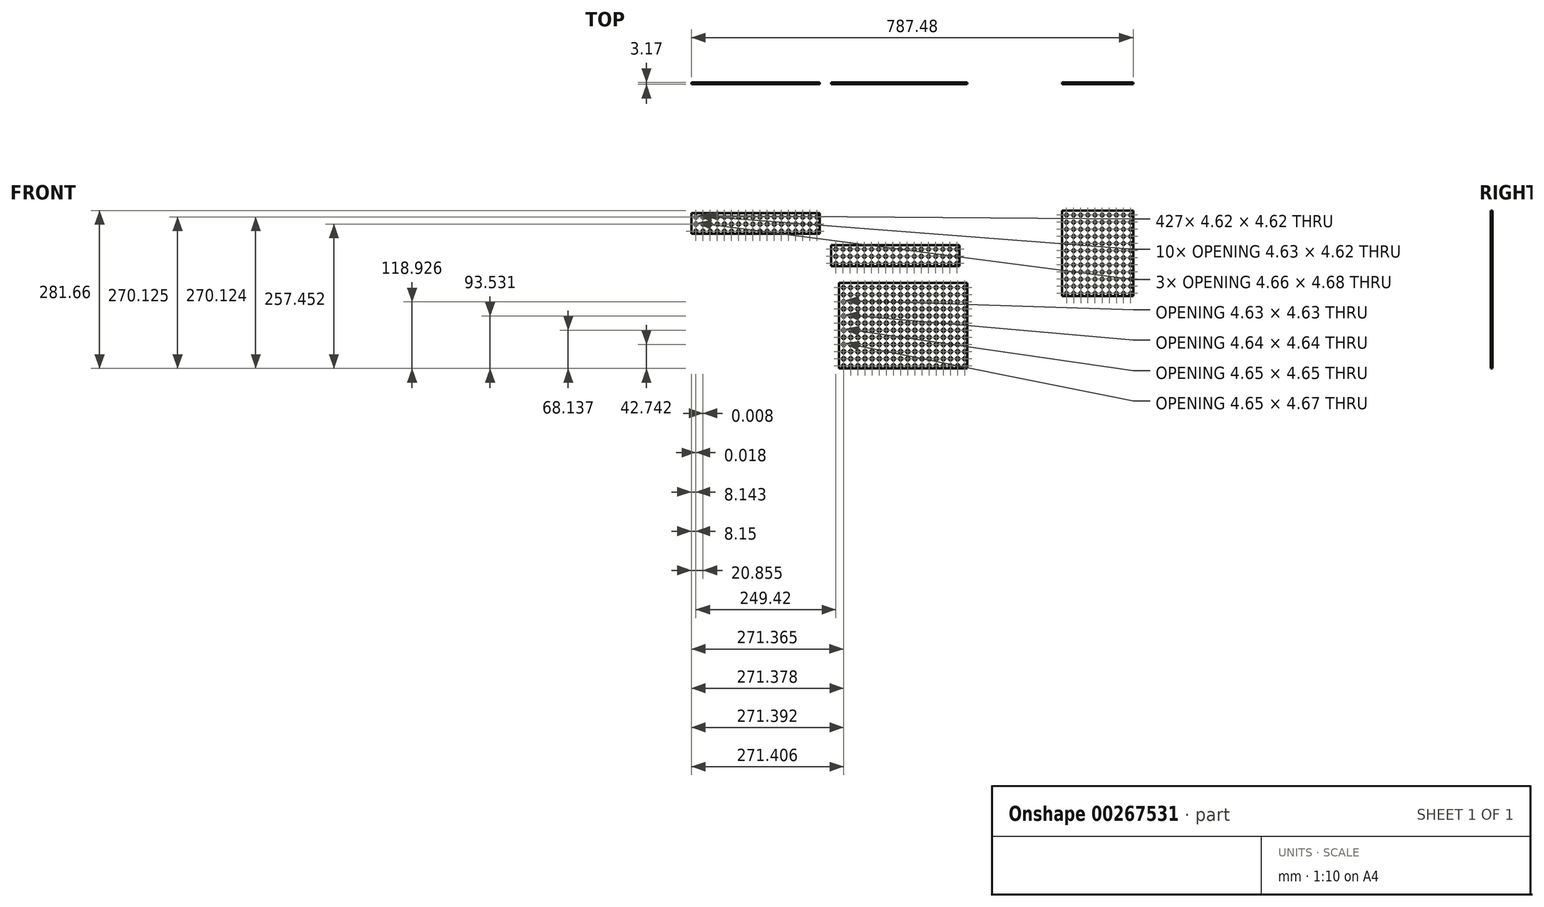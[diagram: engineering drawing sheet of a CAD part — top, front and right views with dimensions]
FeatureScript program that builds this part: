
annotation { "Feature Type Name" : "Feature", "Feature Type Description" : "" }
export const myFeature = defineFeature(function(context is Context, id is Id, definition is map)
    precondition{}
    {
        {
            var Q0;
            Q0=qCreatedBy(makeId("Front.planeOp"),FACE);
            var sketch = newSketch(context, id + "F0", { "sketchPlane" : qUnion([Q0])});
            skLineSegment(sketch, "E0", {"start": v(-0.59, 75.15) * mm, "end": v(113.71, 75.15) * mm});
            skLineSegment(sketch, "E1", {"start": v(-0.59, -77.25) * mm, "end": v(113.71, -77.25) * mm});
            skLineSegment(sketch, "E2", {"start": v(-0.59, -77.25) * mm, "end": v(-114.89, -77.25) * mm});
            skLineSegment(sketch, "E3", {"start": v(-114.89, 75.15) * mm, "end": v(-114.89, -77.25) * mm});
            skLineSegment(sketch, "E4", {"start": v(113.71, 75.15) * mm, "end": v(113.71, -77.25) * mm});
            skLineSegment(sketch, "E5", {"start": v(-114.89, -77.25) * mm, "end": v(-114.89, -73.21) * mm});
            skLineSegment(sketch, "E6", {"start": v(-114.89, -77.25) * mm, "end": v(-110.85, -77.25) * mm});
            skLineSegment(sketch, "E7", {"start": v(-114.89, 75.15) * mm, "end": v(-114.89, 71.1) * mm});
            skLineSegment(sketch, "E8", {"start": v(113.71, 75.15) * mm, "end": v(109.67, 75.15) * mm});
            skLineSegment(sketch, "E9", {"start": v(-97.56, 75.15) * mm, "end": v(113.71, 75.15) * mm});
            skLineSegment(sketch, "E10", {"start": v(-114.89, 75.15) * mm, "end": v(-97.56, 75.15) * mm});
            skLineSegment(sketch, "E11", {"start": v(-114.89, 75.15) * mm, "end": v(-106.8, 75.15) * mm});
            skLineSegment(sketch, "E12.bottom", {"start": v(-109.12, 69.38) * mm, "end": v(-104.5, 69.38) * mm});
            skLineSegment(sketch, "E12.top", {"start": v(-109.12, 64.76) * mm, "end": v(-104.5, 64.76) * mm});
            skLineSegment(sketch, "E12.left", {"start": v(-109.12, 69.38) * mm, "end": v(-109.12, 64.76) * mm});
            skLineSegment(sketch, "E12.right", {"start": v(-104.5, 69.38) * mm, "end": v(-104.5, 64.76) * mm});
            skPoint(sketch, "E12.middle", {"position": v(-106.8, 67.07) * mm});
            skLineSegment(sketch, "E13.bottom", {"start": v(-109.12, 56.68) * mm, "end": v(-104.5, 56.68) * mm});
            skLineSegment(sketch, "E13.top", {"start": v(-109.12, 52.06) * mm, "end": v(-104.5, 52.06) * mm});
            skLineSegment(sketch, "E13.left", {"start": v(-109.12, 56.68) * mm, "end": v(-109.12, 52.06) * mm});
            skLineSegment(sketch, "E13.right", {"start": v(-104.5, 56.68) * mm, "end": v(-104.5, 52.06) * mm});
            skPoint(sketch, "E13.middle", {"position": v(-106.8, 54.37) * mm});
            skLineSegment(sketch, "E14.bottom", {"start": v(-96.42, 69.38) * mm, "end": v(-91.8, 69.38) * mm});
            skLineSegment(sketch, "E14.top", {"start": v(-96.42, 64.76) * mm, "end": v(-91.8, 64.76) * mm});
            skLineSegment(sketch, "E14.left", {"start": v(-96.42, 69.38) * mm, "end": v(-96.42, 64.76) * mm});
            skLineSegment(sketch, "E14.right", {"start": v(-91.8, 69.38) * mm, "end": v(-91.8, 64.76) * mm});
            skPoint(sketch, "E14.middle", {"position": v(-94.1, 67.07) * mm});
            skLineSegment(sketch, "E15.1.0.0", {"start": v(-83.72, 69.38) * mm, "end": v(-79.1, 69.38) * mm});
            skLineSegment(sketch, "E15.1.0.1", {"start": v(-79.1, 69.38) * mm, "end": v(-79.1, 64.76) * mm});
            skLineSegment(sketch, "E15.1.0.2", {"start": v(-83.72, 64.76) * mm, "end": v(-79.1, 64.76) * mm});
            skLineSegment(sketch, "E15.1.0.3", {"start": v(-83.72, 69.38) * mm, "end": v(-83.72, 64.76) * mm});
            skLineSegment(sketch, "E15.1.0.4", {"start": v(-71.02, 69.38) * mm, "end": v(-66.4, 69.38) * mm});
            skLineSegment(sketch, "E15.1.0.5", {"start": v(-66.4, 69.38) * mm, "end": v(-66.4, 64.76) * mm});
            skLineSegment(sketch, "E15.1.0.6", {"start": v(-71.02, 64.76) * mm, "end": v(-66.4, 64.76) * mm});
            skLineSegment(sketch, "E15.1.0.7", {"start": v(-71.02, 69.38) * mm, "end": v(-71.02, 64.76) * mm});
            skLineSegment(sketch, "E15.2.0.0", {"start": v(-58.32, 69.38) * mm, "end": v(-53.7, 69.38) * mm});
            skLineSegment(sketch, "E15.2.0.1", {"start": v(-53.7, 69.38) * mm, "end": v(-53.7, 64.76) * mm});
            skLineSegment(sketch, "E15.2.0.2", {"start": v(-58.32, 64.76) * mm, "end": v(-53.7, 64.76) * mm});
            skLineSegment(sketch, "E15.2.0.3", {"start": v(-58.32, 69.38) * mm, "end": v(-58.32, 64.76) * mm});
            skLineSegment(sketch, "E15.2.0.4", {"start": v(-45.62, 69.38) * mm, "end": v(-41, 69.38) * mm});
            skLineSegment(sketch, "E15.2.0.5", {"start": v(-41, 69.38) * mm, "end": v(-41, 64.76) * mm});
            skLineSegment(sketch, "E15.2.0.6", {"start": v(-45.62, 64.76) * mm, "end": v(-41, 64.76) * mm});
            skLineSegment(sketch, "E15.2.0.7", {"start": v(-45.62, 69.38) * mm, "end": v(-45.62, 64.76) * mm});
            skLineSegment(sketch, "E15.3.0.0", {"start": v(-32.92, 69.38) * mm, "end": v(-28.3, 69.38) * mm});
            skLineSegment(sketch, "E15.3.0.1", {"start": v(-28.3, 69.38) * mm, "end": v(-28.3, 64.76) * mm});
            skLineSegment(sketch, "E15.3.0.2", {"start": v(-32.92, 64.76) * mm, "end": v(-28.3, 64.76) * mm});
            skLineSegment(sketch, "E15.3.0.3", {"start": v(-32.92, 69.38) * mm, "end": v(-32.92, 64.76) * mm});
            skLineSegment(sketch, "E15.3.0.4", {"start": v(-20.22, 69.38) * mm, "end": v(-15.6, 69.38) * mm});
            skLineSegment(sketch, "E15.3.0.5", {"start": v(-15.6, 69.38) * mm, "end": v(-15.6, 64.76) * mm});
            skLineSegment(sketch, "E15.3.0.6", {"start": v(-20.22, 64.76) * mm, "end": v(-15.6, 64.76) * mm});
            skLineSegment(sketch, "E15.3.0.7", {"start": v(-20.22, 69.38) * mm, "end": v(-20.22, 64.76) * mm});
            skLineSegment(sketch, "E15.4.0.0", {"start": v(-7.52, 69.38) * mm, "end": v(-2.9, 69.38) * mm});
            skLineSegment(sketch, "E15.4.0.1", {"start": v(-2.9, 69.38) * mm, "end": v(-2.9, 64.76) * mm});
            skLineSegment(sketch, "E15.4.0.2", {"start": v(-7.52, 64.76) * mm, "end": v(-2.9, 64.76) * mm});
            skLineSegment(sketch, "E15.4.0.3", {"start": v(-7.52, 69.38) * mm, "end": v(-7.52, 64.76) * mm});
            skLineSegment(sketch, "E15.4.0.4", {"start": v(5.18, 69.38) * mm, "end": v(9.8, 69.38) * mm});
            skLineSegment(sketch, "E15.4.0.5", {"start": v(9.8, 69.38) * mm, "end": v(9.8, 64.76) * mm});
            skLineSegment(sketch, "E15.4.0.6", {"start": v(5.18, 64.76) * mm, "end": v(9.8, 64.76) * mm});
            skLineSegment(sketch, "E15.4.0.7", {"start": v(5.18, 69.38) * mm, "end": v(5.18, 64.76) * mm});
            skLineSegment(sketch, "E15.5.0.0", {"start": v(17.88, 69.38) * mm, "end": v(22.5, 69.38) * mm});
            skLineSegment(sketch, "E15.5.0.1", {"start": v(22.5, 69.38) * mm, "end": v(22.5, 64.76) * mm});
            skLineSegment(sketch, "E15.5.0.2", {"start": v(17.88, 64.76) * mm, "end": v(22.5, 64.76) * mm});
            skLineSegment(sketch, "E15.5.0.3", {"start": v(17.88, 69.38) * mm, "end": v(17.88, 64.76) * mm});
            skLineSegment(sketch, "E15.5.0.4", {"start": v(30.58, 69.38) * mm, "end": v(35.2, 69.38) * mm});
            skLineSegment(sketch, "E15.5.0.5", {"start": v(35.2, 69.38) * mm, "end": v(35.2, 64.76) * mm});
            skLineSegment(sketch, "E15.5.0.6", {"start": v(30.58, 64.76) * mm, "end": v(35.2, 64.76) * mm});
            skLineSegment(sketch, "E15.5.0.7", {"start": v(30.58, 69.38) * mm, "end": v(30.58, 64.76) * mm});
            skLineSegment(sketch, "E15.6.0.0", {"start": v(43.28, 69.38) * mm, "end": v(47.9, 69.38) * mm});
            skLineSegment(sketch, "E15.6.0.1", {"start": v(47.9, 69.38) * mm, "end": v(47.9, 64.76) * mm});
            skLineSegment(sketch, "E15.6.0.2", {"start": v(43.28, 64.76) * mm, "end": v(47.9, 64.76) * mm});
            skLineSegment(sketch, "E15.6.0.3", {"start": v(43.28, 69.38) * mm, "end": v(43.28, 64.76) * mm});
            skLineSegment(sketch, "E15.6.0.4", {"start": v(55.98, 69.38) * mm, "end": v(60.6, 69.38) * mm});
            skLineSegment(sketch, "E15.6.0.5", {"start": v(60.6, 69.38) * mm, "end": v(60.6, 64.76) * mm});
            skLineSegment(sketch, "E15.6.0.6", {"start": v(55.98, 64.76) * mm, "end": v(60.6, 64.76) * mm});
            skLineSegment(sketch, "E15.6.0.7", {"start": v(55.98, 69.38) * mm, "end": v(55.98, 64.76) * mm});
            skLineSegment(sketch, "E15.7.0.0", {"start": v(68.68, 69.38) * mm, "end": v(73.3, 69.38) * mm});
            skLineSegment(sketch, "E15.7.0.1", {"start": v(73.3, 69.38) * mm, "end": v(73.3, 64.76) * mm});
            skLineSegment(sketch, "E15.7.0.2", {"start": v(68.68, 64.76) * mm, "end": v(73.3, 64.76) * mm});
            skLineSegment(sketch, "E15.7.0.3", {"start": v(68.68, 69.38) * mm, "end": v(68.68, 64.76) * mm});
            skLineSegment(sketch, "E15.7.0.4", {"start": v(81.38, 69.38) * mm, "end": v(86, 69.38) * mm});
            skLineSegment(sketch, "E15.7.0.5", {"start": v(86, 69.38) * mm, "end": v(86, 64.76) * mm});
            skLineSegment(sketch, "E15.7.0.6", {"start": v(81.38, 64.76) * mm, "end": v(86, 64.76) * mm});
            skLineSegment(sketch, "E15.7.0.7", {"start": v(81.38, 69.38) * mm, "end": v(81.38, 64.76) * mm});
            skLineSegment(sketch, "E15.8.0.0", {"start": v(94.08, 69.38) * mm, "end": v(98.7, 69.38) * mm});
            skLineSegment(sketch, "E15.8.0.1", {"start": v(98.7, 69.38) * mm, "end": v(98.7, 64.76) * mm});
            skLineSegment(sketch, "E15.8.0.2", {"start": v(94.08, 64.76) * mm, "end": v(98.7, 64.76) * mm});
            skLineSegment(sketch, "E15.8.0.3", {"start": v(94.08, 69.38) * mm, "end": v(94.08, 64.76) * mm});
            skLineSegment(sketch, "E15.8.0.4", {"start": v(106.78, 69.38) * mm, "end": v(111.4, 69.38) * mm});
            skLineSegment(sketch, "E15.8.0.5", {"start": v(111.4, 69.38) * mm, "end": v(111.4, 64.76) * mm});
            skLineSegment(sketch, "E15.8.0.6", {"start": v(106.78, 64.76) * mm, "end": v(111.4, 64.76) * mm});
            skLineSegment(sketch, "E15.8.0.7", {"start": v(106.78, 69.38) * mm, "end": v(106.78, 64.76) * mm});
            skPoint(sketch, "E16.0.1.0", {"position": v(-94.1, 54.37) * mm});
            skLineSegment(sketch, "E16.0.1.2", {"start": v(-71.01, 52.06) * mm, "end": v(-66.39, 52.06) * mm});
            skLineSegment(sketch, "E16.0.1.3", {"start": v(-109.11, 52.06) * mm, "end": v(-104.49, 52.06) * mm});
            skLineSegment(sketch, "E16.0.1.4", {"start": v(68.69, 56.68) * mm, "end": v(73.31, 56.68) * mm});
            skLineSegment(sketch, "E16.0.1.5", {"start": v(-96.41, 56.68) * mm, "end": v(-91.79, 56.68) * mm});
            skLineSegment(sketch, "E16.0.1.6", {"start": v(17.89, 56.68) * mm, "end": v(22.51, 56.68) * mm});
            skLineSegment(sketch, "E16.0.1.7", {"start": v(-32.91, 56.68) * mm, "end": v(-28.29, 56.68) * mm});
            skLineSegment(sketch, "E16.0.1.8", {"start": v(-83.71, 56.68) * mm, "end": v(-79.09, 56.68) * mm});
            skLineSegment(sketch, "E16.0.1.9", {"start": v(-7.51, 56.68) * mm, "end": v(-2.89, 56.68) * mm});
            skLineSegment(sketch, "E16.0.1.10", {"start": v(-58.31, 52.06) * mm, "end": v(-53.69, 52.06) * mm});
            skLineSegment(sketch, "E16.0.1.11", {"start": v(17.89, 56.68) * mm, "end": v(17.89, 52.06) * mm});
            skLineSegment(sketch, "E16.0.1.12", {"start": v(35.21, 56.68) * mm, "end": v(35.21, 52.06) * mm});
            skLineSegment(sketch, "E16.0.1.13", {"start": v(-15.59, 56.68) * mm, "end": v(-15.59, 52.06) * mm});
            skLineSegment(sketch, "E16.0.1.14", {"start": v(-66.39, 56.68) * mm, "end": v(-66.39, 52.06) * mm});
            skLineSegment(sketch, "E16.0.1.15", {"start": v(106.79, 56.68) * mm, "end": v(111.41, 56.68) * mm});
            skLineSegment(sketch, "E16.0.1.16", {"start": v(73.31, 56.68) * mm, "end": v(73.31, 52.06) * mm});
            skLineSegment(sketch, "E16.0.1.17", {"start": v(22.51, 56.68) * mm, "end": v(22.51, 52.06) * mm});
            skLineSegment(sketch, "E16.0.1.18", {"start": v(30.59, 56.68) * mm, "end": v(30.59, 52.06) * mm});
            skLineSegment(sketch, "E16.0.1.19", {"start": v(-28.29, 56.68) * mm, "end": v(-28.29, 52.06) * mm});
            skLineSegment(sketch, "E16.0.1.20", {"start": v(-2.89, 56.68) * mm, "end": v(-2.89, 52.06) * mm});
            skLineSegment(sketch, "E16.0.1.21", {"start": v(-53.69, 56.68) * mm, "end": v(-53.69, 52.06) * mm});
            skLineSegment(sketch, "E16.0.1.22", {"start": v(-7.51, 52.06) * mm, "end": v(-2.89, 52.06) * mm});
            skLineSegment(sketch, "E16.0.1.23", {"start": v(68.69, 56.68) * mm, "end": v(68.69, 52.06) * mm});
            skLineSegment(sketch, "E16.0.1.24", {"start": v(-79.09, 56.68) * mm, "end": v(-79.09, 52.06) * mm});
            skLineSegment(sketch, "E16.0.1.25", {"start": v(-20.21, 56.68) * mm, "end": v(-20.21, 52.06) * mm});
            skLineSegment(sketch, "E16.0.1.26", {"start": v(-32.91, 56.68) * mm, "end": v(-32.91, 52.06) * mm});
            skLineSegment(sketch, "E16.0.1.27", {"start": v(-83.71, 56.68) * mm, "end": v(-83.71, 52.06) * mm});
            skLineSegment(sketch, "E16.0.1.28", {"start": v(81.39, 56.68) * mm, "end": v(81.39, 52.06) * mm});
            skLineSegment(sketch, "E16.0.1.29", {"start": v(-104.49, 56.68) * mm, "end": v(-104.49, 52.06) * mm});
            skLineSegment(sketch, "E16.0.1.30", {"start": v(86.01, 56.68) * mm, "end": v(86.01, 52.06) * mm});
            skLineSegment(sketch, "E16.0.1.31", {"start": v(-71.01, 56.68) * mm, "end": v(-71.01, 52.06) * mm});
            skLineSegment(sketch, "E16.0.1.32", {"start": v(-7.51, 56.68) * mm, "end": v(-7.51, 52.06) * mm});
            skLineSegment(sketch, "E16.0.1.33", {"start": v(94.09, 52.06) * mm, "end": v(98.71, 52.06) * mm});
            skLineSegment(sketch, "E16.0.1.34", {"start": v(43.29, 52.06) * mm, "end": v(47.91, 52.06) * mm});
            skLineSegment(sketch, "E16.0.1.35", {"start": v(-109.11, 56.68) * mm, "end": v(-104.49, 56.68) * mm});
            skLineSegment(sketch, "E16.0.1.36", {"start": v(81.39, 52.06) * mm, "end": v(86.01, 52.06) * mm});
            skLineSegment(sketch, "E16.0.1.37", {"start": v(68.69, 52.06) * mm, "end": v(73.31, 52.06) * mm});
            skLineSegment(sketch, "E16.0.1.38", {"start": v(-58.31, 56.68) * mm, "end": v(-58.31, 52.06) * mm});
            skLineSegment(sketch, "E16.0.1.39", {"start": v(30.59, 52.06) * mm, "end": v(35.21, 52.06) * mm});
            skLineSegment(sketch, "E16.0.1.40", {"start": v(17.89, 52.06) * mm, "end": v(22.51, 52.06) * mm});
            skLineSegment(sketch, "E16.0.1.41", {"start": v(-20.21, 52.06) * mm, "end": v(-15.59, 52.06) * mm});
            skLineSegment(sketch, "E16.0.1.42", {"start": v(-32.91, 52.06) * mm, "end": v(-28.29, 52.06) * mm});
            skLineSegment(sketch, "E16.0.1.43", {"start": v(-83.71, 52.06) * mm, "end": v(-79.09, 52.06) * mm});
            skLineSegment(sketch, "E16.0.1.44", {"start": v(94.09, 56.68) * mm, "end": v(94.09, 52.06) * mm});
            skLineSegment(sketch, "E16.0.1.45", {"start": v(43.29, 56.68) * mm, "end": v(43.29, 52.06) * mm});
            skLineSegment(sketch, "E16.0.1.46", {"start": v(-58.31, 56.68) * mm, "end": v(-53.69, 56.68) * mm});
            skLineSegment(sketch, "E16.0.1.47", {"start": v(5.19, 56.68) * mm, "end": v(9.81, 56.68) * mm});
            skLineSegment(sketch, "E16.0.1.48", {"start": v(-45.61, 56.68) * mm, "end": v(-40.99, 56.68) * mm});
            skLineSegment(sketch, "E16.0.1.49", {"start": v(94.09, 56.68) * mm, "end": v(98.71, 56.68) * mm});
            skLineSegment(sketch, "E16.0.1.50", {"start": v(43.29, 56.68) * mm, "end": v(47.91, 56.68) * mm});
            skLineSegment(sketch, "E16.0.1.51", {"start": v(55.99, 56.68) * mm, "end": v(60.61, 56.68) * mm});
            skLineSegment(sketch, "E16.0.1.52", {"start": v(5.19, 52.06) * mm, "end": v(9.81, 52.06) * mm});
            skLineSegment(sketch, "E16.0.1.53", {"start": v(55.99, 52.06) * mm, "end": v(60.61, 52.06) * mm});
            skLineSegment(sketch, "E16.0.1.54", {"start": v(-45.61, 52.06) * mm, "end": v(-40.99, 52.06) * mm});
            skLineSegment(sketch, "E16.0.1.55", {"start": v(-96.41, 56.68) * mm, "end": v(-96.41, 52.06) * mm});
            skLineSegment(sketch, "E16.0.1.56", {"start": v(98.71, 56.68) * mm, "end": v(98.71, 52.06) * mm});
            skLineSegment(sketch, "E16.0.1.57", {"start": v(47.91, 56.68) * mm, "end": v(47.91, 52.06) * mm});
            skLineSegment(sketch, "E16.0.1.58", {"start": v(106.79, 52.06) * mm, "end": v(111.41, 52.06) * mm});
            skLineSegment(sketch, "E16.0.1.59", {"start": v(-71.01, 56.68) * mm, "end": v(-66.39, 56.68) * mm});
            skLineSegment(sketch, "E16.0.1.60", {"start": v(106.79, 56.68) * mm, "end": v(106.79, 52.06) * mm});
            skLineSegment(sketch, "E16.0.1.61", {"start": v(-20.21, 56.68) * mm, "end": v(-15.59, 56.68) * mm});
            skLineSegment(sketch, "E16.0.1.62", {"start": v(-91.79, 56.68) * mm, "end": v(-91.79, 52.06) * mm});
            skLineSegment(sketch, "E16.0.1.63", {"start": v(30.59, 56.68) * mm, "end": v(35.21, 56.68) * mm});
            skLineSegment(sketch, "E16.0.1.64", {"start": v(81.39, 56.68) * mm, "end": v(86.01, 56.68) * mm});
            skLineSegment(sketch, "E16.0.1.65", {"start": v(-45.61, 56.68) * mm, "end": v(-45.61, 52.06) * mm});
            skLineSegment(sketch, "E16.0.1.66", {"start": v(5.19, 56.68) * mm, "end": v(5.19, 52.06) * mm});
            skLineSegment(sketch, "E16.0.1.67", {"start": v(55.99, 56.68) * mm, "end": v(55.99, 52.06) * mm});
            skLineSegment(sketch, "E16.0.1.68", {"start": v(60.61, 56.68) * mm, "end": v(60.61, 52.06) * mm});
            skLineSegment(sketch, "E16.0.1.69", {"start": v(111.41, 56.68) * mm, "end": v(111.41, 52.06) * mm});
            skLineSegment(sketch, "E16.0.1.70", {"start": v(-96.41, 52.06) * mm, "end": v(-91.79, 52.06) * mm});
            skLineSegment(sketch, "E16.0.1.71", {"start": v(-40.99, 56.68) * mm, "end": v(-40.99, 52.06) * mm});
            skLineSegment(sketch, "E16.0.1.72", {"start": v(-109.11, 56.68) * mm, "end": v(-109.11, 52.06) * mm});
            skLineSegment(sketch, "E16.0.1.73", {"start": v(9.81, 56.68) * mm, "end": v(9.81, 52.06) * mm});
            skLineSegment(sketch, "E17.1.0.0", {"start": v(-109.11, 44) * mm, "end": v(-104.49, 44) * mm});
            skLineSegment(sketch, "E17.1.0.1", {"start": v(-109.11, 44) * mm, "end": v(-109.11, 39.37) * mm});
            skLineSegment(sketch, "E17.1.0.2", {"start": v(-109.11, 39.37) * mm, "end": v(-104.49, 39.37) * mm});
            skLineSegment(sketch, "E17.1.0.3", {"start": v(-104.49, 44) * mm, "end": v(-104.49, 39.37) * mm});
            skLineSegment(sketch, "E17.1.0.4", {"start": v(-109.1, 31.3) * mm, "end": v(-104.48, 31.3) * mm});
            skLineSegment(sketch, "E17.1.0.5", {"start": v(-104.49, 31.3) * mm, "end": v(-104.49, 26.67) * mm});
            skLineSegment(sketch, "E17.1.0.6", {"start": v(-109.1, 26.67) * mm, "end": v(-104.48, 26.67) * mm});
            skLineSegment(sketch, "E17.1.0.7", {"start": v(-109.11, 31.3) * mm, "end": v(-109.11, 26.67) * mm});
            skLineSegment(sketch, "E17.2.0.0", {"start": v(-109.1, 18.6) * mm, "end": v(-104.48, 18.6) * mm});
            skLineSegment(sketch, "E17.2.0.1", {"start": v(-109.1, 18.6) * mm, "end": v(-109.1, 13.98) * mm});
            skLineSegment(sketch, "E17.2.0.2", {"start": v(-109.1, 13.98) * mm, "end": v(-104.48, 13.98) * mm});
            skLineSegment(sketch, "E17.2.0.3", {"start": v(-104.48, 18.6) * mm, "end": v(-104.48, 13.98) * mm});
            skLineSegment(sketch, "E17.2.0.4", {"start": v(-109.1, 5.9) * mm, "end": v(-104.47, 5.9) * mm});
            skLineSegment(sketch, "E17.2.0.5", {"start": v(-104.48, 5.9) * mm, "end": v(-104.48, 1.28) * mm});
            skLineSegment(sketch, "E17.2.0.6", {"start": v(-109.1, 1.28) * mm, "end": v(-104.47, 1.28) * mm});
            skLineSegment(sketch, "E17.2.0.7", {"start": v(-109.1, 5.9) * mm, "end": v(-109.1, 1.28) * mm});
            skLineSegment(sketch, "E17.3.0.0", {"start": v(-109.1, -6.79) * mm, "end": v(-104.47, -6.79) * mm});
            skLineSegment(sketch, "E17.3.0.1", {"start": v(-109.1, -6.79) * mm, "end": v(-109.1, -11.4) * mm});
            skLineSegment(sketch, "E17.3.0.2", {"start": v(-109.1, -11.4) * mm, "end": v(-104.47, -11.4) * mm});
            skLineSegment(sketch, "E17.3.0.3", {"start": v(-104.47, -6.79) * mm, "end": v(-104.47, -11.4) * mm});
            skLineSegment(sketch, "E17.3.0.4", {"start": v(-109.08, -19.49) * mm, "end": v(-104.46, -19.49) * mm});
            skLineSegment(sketch, "E17.3.0.5", {"start": v(-104.47, -19.49) * mm, "end": v(-104.47, -24.1) * mm});
            skLineSegment(sketch, "E17.3.0.6", {"start": v(-109.08, -24.11) * mm, "end": v(-104.46, -24.11) * mm});
            skLineSegment(sketch, "E17.3.0.7", {"start": v(-109.1, -19.49) * mm, "end": v(-109.1, -24.1) * mm});
            skLineSegment(sketch, "E17.4.0.0", {"start": v(-109.08, -32.18) * mm, "end": v(-104.46, -32.18) * mm});
            skLineSegment(sketch, "E17.4.0.1", {"start": v(-109.08, -32.18) * mm, "end": v(-109.08, -36.8) * mm});
            skLineSegment(sketch, "E17.4.0.2", {"start": v(-109.08, -36.8) * mm, "end": v(-104.46, -36.8) * mm});
            skLineSegment(sketch, "E17.4.0.3", {"start": v(-104.46, -32.18) * mm, "end": v(-104.46, -36.8) * mm});
            skLineSegment(sketch, "E17.4.0.4", {"start": v(-109.07, -44.88) * mm, "end": v(-104.45, -44.88) * mm});
            skLineSegment(sketch, "E17.4.0.5", {"start": v(-104.46, -44.88) * mm, "end": v(-104.46, -49.5) * mm});
            skLineSegment(sketch, "E17.4.0.6", {"start": v(-109.07, -49.5) * mm, "end": v(-104.45, -49.5) * mm});
            skLineSegment(sketch, "E17.4.0.7", {"start": v(-109.08, -44.88) * mm, "end": v(-109.08, -49.5) * mm});
            skLineSegment(sketch, "E17.5.0.0", {"start": v(-109.07, -57.56) * mm, "end": v(-104.45, -57.56) * mm});
            skLineSegment(sketch, "E17.5.0.1", {"start": v(-109.07, -57.56) * mm, "end": v(-109.07, -62.19) * mm});
            skLineSegment(sketch, "E17.5.0.2", {"start": v(-109.07, -62.19) * mm, "end": v(-104.45, -62.19) * mm});
            skLineSegment(sketch, "E17.5.0.3", {"start": v(-104.45, -57.56) * mm, "end": v(-104.45, -62.19) * mm});
            skLineSegment(sketch, "E17.5.0.4", {"start": v(-109.06, -70.27) * mm, "end": v(-104.44, -70.27) * mm});
            skLineSegment(sketch, "E17.5.0.5", {"start": v(-104.45, -70.26) * mm, "end": v(-104.45, -74.89) * mm});
            skLineSegment(sketch, "E17.5.0.6", {"start": v(-109.06, -74.89) * mm, "end": v(-104.44, -74.89) * mm});
            skLineSegment(sketch, "E17.5.0.7", {"start": v(-109.07, -70.26) * mm, "end": v(-109.07, -74.89) * mm});
            skPoint(sketch, "E18.1.0.0", {"position": v(-106.8, 41.67) * mm});
            skPoint(sketch, "E18.1.0.1", {"position": v(-106.78, 28.97) * mm});
            skPoint(sketch, "E18.1.0.2", {"position": v(-94.08, 28.97) * mm});
            skPoint(sketch, "E18.1.0.3", {"position": v(-94.1, 41.67) * mm});
            skPoint(sketch, "E18.1.0.6", {"position": v(-106.8, 28.97) * mm});
            skLineSegment(sketch, "E18.1.0.8", {"start": v(68.7, 31.28) * mm, "end": v(73.33, 31.28) * mm});
            skLineSegment(sketch, "E18.1.0.9", {"start": v(-2.87, 31.28) * mm, "end": v(-2.87, 26.66) * mm});
            skLineSegment(sketch, "E18.1.0.14", {"start": v(-58.3, 43.98) * mm, "end": v(-58.3, 39.36) * mm});
            skLineSegment(sketch, "E18.1.0.15", {"start": v(-7.5, 43.98) * mm, "end": v(-7.5, 39.36) * mm});
            skLineSegment(sketch, "E18.1.0.16", {"start": v(47.93, 31.28) * mm, "end": v(47.93, 26.66) * mm});
            skLineSegment(sketch, "E18.1.0.17", {"start": v(9.83, 31.28) * mm, "end": v(9.83, 26.66) * mm});
            skLineSegment(sketch, "E18.1.0.18", {"start": v(-7.5, 31.28) * mm, "end": v(-2.87, 31.28) * mm});
            skLineSegment(sketch, "E18.1.0.19", {"start": v(-20.2, 31.28) * mm, "end": v(-20.2, 26.66) * mm});
            skLineSegment(sketch, "E18.1.0.20", {"start": v(-20.2, 26.66) * mm, "end": v(-15.57, 26.66) * mm});
            skLineSegment(sketch, "E18.1.0.21", {"start": v(-83.7, 43.98) * mm, "end": v(-79.08, 43.98) * mm});
            skLineSegment(sketch, "E18.1.0.22", {"start": v(-32.9, 43.98) * mm, "end": v(-28.28, 43.98) * mm});
            skLineSegment(sketch, "E18.1.0.23", {"start": v(17.9, 43.98) * mm, "end": v(22.52, 43.98) * mm});
            skLineSegment(sketch, "E18.1.0.24", {"start": v(68.7, 43.98) * mm, "end": v(73.32, 43.98) * mm});
            skLineSegment(sketch, "E18.1.0.25", {"start": v(35.23, 31.28) * mm, "end": v(35.23, 26.66) * mm});
            skLineSegment(sketch, "E18.1.0.26", {"start": v(56, 31.28) * mm, "end": v(60.63, 31.28) * mm});
            skLineSegment(sketch, "E18.1.0.27", {"start": v(56, 31.28) * mm, "end": v(56, 26.66) * mm});
            skLineSegment(sketch, "E18.1.0.28", {"start": v(43.3, 39.36) * mm, "end": v(47.92, 39.36) * mm});
            skLineSegment(sketch, "E18.1.0.29", {"start": v(94.1, 39.36) * mm, "end": v(98.72, 39.36) * mm});
            skLineSegment(sketch, "E18.1.0.30", {"start": v(-28.27, 31.28) * mm, "end": v(-28.27, 26.66) * mm});
            skLineSegment(sketch, "E18.1.0.31", {"start": v(-58.3, 39.36) * mm, "end": v(-53.68, 39.36) * mm});
            skLineSegment(sketch, "E18.1.0.32", {"start": v(-7.5, 39.36) * mm, "end": v(-2.88, 39.36) * mm});
            skLineSegment(sketch, "E18.1.0.33", {"start": v(81.4, 31.28) * mm, "end": v(81.4, 26.66) * mm});
            skLineSegment(sketch, "E18.1.0.34", {"start": v(43.3, 31.28) * mm, "end": v(47.93, 31.28) * mm});
            skLineSegment(sketch, "E18.1.0.35", {"start": v(43.3, 26.66) * mm, "end": v(47.93, 26.66) * mm});
            skLineSegment(sketch, "E18.1.0.36", {"start": v(5.2, 31.28) * mm, "end": v(5.2, 26.66) * mm});
            skLineSegment(sketch, "E18.1.0.37", {"start": v(94.1, 31.28) * mm, "end": v(94.1, 26.66) * mm});
            skLineSegment(sketch, "E18.1.0.38", {"start": v(47.92, 43.98) * mm, "end": v(47.92, 39.36) * mm});
            skLineSegment(sketch, "E18.1.0.39", {"start": v(98.72, 43.98) * mm, "end": v(98.72, 39.36) * mm});
            skLineSegment(sketch, "E18.1.0.40", {"start": v(30.6, 31.28) * mm, "end": v(30.6, 26.66) * mm});
            skLineSegment(sketch, "E18.1.0.41", {"start": v(-71, 26.66) * mm, "end": v(-66.37, 26.66) * mm});
            skLineSegment(sketch, "E18.1.0.42", {"start": v(98.73, 31.28) * mm, "end": v(98.73, 26.66) * mm});
            skLineSegment(sketch, "E18.1.0.43", {"start": v(-53.68, 43.98) * mm, "end": v(-53.68, 39.36) * mm});
            skLineSegment(sketch, "E18.1.0.44", {"start": v(-2.88, 43.98) * mm, "end": v(-2.88, 39.36) * mm});
            skLineSegment(sketch, "E18.1.0.45", {"start": v(106.8, 43.98) * mm, "end": v(106.8, 39.36) * mm});
            skLineSegment(sketch, "E18.1.0.46", {"start": v(94.1, 26.66) * mm, "end": v(98.73, 26.66) * mm});
            skLineSegment(sketch, "E18.1.0.47", {"start": v(94.1, 31.28) * mm, "end": v(98.73, 31.28) * mm});
            skLineSegment(sketch, "E18.1.0.48", {"start": v(-83.7, 31.28) * mm, "end": v(-79.07, 31.28) * mm});
            skLineSegment(sketch, "E18.1.0.49", {"start": v(-45.6, 31.28) * mm, "end": v(-45.6, 26.66) * mm});
            skLineSegment(sketch, "E18.1.0.50", {"start": v(-79.07, 31.28) * mm, "end": v(-79.07, 26.66) * mm});
            skLineSegment(sketch, "E18.1.0.51", {"start": v(17.9, 26.66) * mm, "end": v(22.53, 26.66) * mm});
            skLineSegment(sketch, "E18.1.0.52", {"start": v(-45.6, 43.98) * mm, "end": v(-45.6, 39.36) * mm});
            skLineSegment(sketch, "E18.1.0.53", {"start": v(5.2, 43.98) * mm, "end": v(5.2, 39.36) * mm});
            skLineSegment(sketch, "E18.1.0.54", {"start": v(43.3, 43.98) * mm, "end": v(47.92, 43.98) * mm});
            skLineSegment(sketch, "E18.1.0.55", {"start": v(94.1, 43.98) * mm, "end": v(98.72, 43.98) * mm});
            skLineSegment(sketch, "E18.1.0.56", {"start": v(56, 43.98) * mm, "end": v(56, 39.36) * mm});
            skLineSegment(sketch, "E18.1.0.57", {"start": v(22.53, 31.28) * mm, "end": v(22.53, 26.66) * mm});
            skLineSegment(sketch, "E18.1.0.58", {"start": v(-58.3, 43.98) * mm, "end": v(-53.68, 43.98) * mm});
            skLineSegment(sketch, "E18.1.0.59", {"start": v(-7.5, 43.98) * mm, "end": v(-2.88, 43.98) * mm});
            skLineSegment(sketch, "E18.1.0.60", {"start": v(-83.7, 43.98) * mm, "end": v(-83.7, 39.36) * mm});
            skLineSegment(sketch, "E18.1.0.61", {"start": v(-58.3, 31.28) * mm, "end": v(-58.3, 26.66) * mm});
            skLineSegment(sketch, "E18.1.0.62", {"start": v(-45.6, 26.66) * mm, "end": v(-40.97, 26.66) * mm});
            skLineSegment(sketch, "E18.1.0.63", {"start": v(-96.4, 26.66) * mm, "end": v(-91.77, 26.66) * mm});
            skLineSegment(sketch, "E18.1.0.64", {"start": v(60.62, 43.98) * mm, "end": v(60.62, 39.36) * mm});
            skLineSegment(sketch, "E18.1.0.65", {"start": v(111.42, 43.98) * mm, "end": v(111.42, 39.36) * mm});
            skLineSegment(sketch, "E18.1.0.66", {"start": v(-7.5, 26.66) * mm, "end": v(-2.87, 26.66) * mm});
            skLineSegment(sketch, "E18.1.0.67", {"start": v(17.9, 31.28) * mm, "end": v(22.53, 31.28) * mm});
            skLineSegment(sketch, "E18.1.0.68", {"start": v(81.4, 31.28) * mm, "end": v(86.03, 31.28) * mm});
            skLineSegment(sketch, "E18.1.0.69", {"start": v(-7.5, 31.28) * mm, "end": v(-7.5, 26.66) * mm});
            skLineSegment(sketch, "E18.1.0.70", {"start": v(73.33, 31.28) * mm, "end": v(73.33, 26.66) * mm});
            skLineSegment(sketch, "E18.1.0.71", {"start": v(-45.6, 31.28) * mm, "end": v(-40.97, 31.28) * mm});
            skLineSegment(sketch, "E18.1.0.72", {"start": v(-71, 43.98) * mm, "end": v(-71, 39.36) * mm});
            skLineSegment(sketch, "E18.1.0.73", {"start": v(-20.2, 43.98) * mm, "end": v(-20.2, 39.36) * mm});
            skLineSegment(sketch, "E18.1.0.74", {"start": v(30.6, 43.98) * mm, "end": v(30.6, 39.36) * mm});
            skLineSegment(sketch, "E18.1.0.75", {"start": v(81.4, 43.98) * mm, "end": v(81.4, 39.36) * mm});
            skLineSegment(sketch, "E18.1.0.76", {"start": v(-40.98, 43.98) * mm, "end": v(-40.98, 39.36) * mm});
            skLineSegment(sketch, "E18.1.0.77", {"start": v(9.82, 43.98) * mm, "end": v(9.82, 39.36) * mm});
            skLineSegment(sketch, "E18.1.0.78", {"start": v(-32.9, 43.98) * mm, "end": v(-32.9, 39.36) * mm});
            skLineSegment(sketch, "E18.1.0.79", {"start": v(30.6, 31.28) * mm, "end": v(35.23, 31.28) * mm});
            skLineSegment(sketch, "E18.1.0.80", {"start": v(106.8, 31.28) * mm, "end": v(111.43, 31.28) * mm});
            skLineSegment(sketch, "E18.1.0.81", {"start": v(-71, 31.28) * mm, "end": v(-71, 26.66) * mm});
            skLineSegment(sketch, "E18.1.0.82", {"start": v(5.2, 31.28) * mm, "end": v(9.83, 31.28) * mm});
            skLineSegment(sketch, "E18.1.0.83", {"start": v(-71, 39.36) * mm, "end": v(-66.38, 39.36) * mm});
            skLineSegment(sketch, "E18.1.0.84", {"start": v(-20.2, 39.36) * mm, "end": v(-15.58, 39.36) * mm});
            skLineSegment(sketch, "E18.1.0.85", {"start": v(30.6, 39.36) * mm, "end": v(35.22, 39.36) * mm});
            skLineSegment(sketch, "E18.1.0.86", {"start": v(81.4, 39.36) * mm, "end": v(86.02, 39.36) * mm});
            skLineSegment(sketch, "E18.1.0.87", {"start": v(17.9, 43.98) * mm, "end": v(17.9, 39.36) * mm});
            skLineSegment(sketch, "E18.1.0.88", {"start": v(-96.4, 31.28) * mm, "end": v(-96.4, 26.66) * mm});
            skLineSegment(sketch, "E18.1.0.89", {"start": v(-66.37, 31.28) * mm, "end": v(-66.37, 26.66) * mm});
            skLineSegment(sketch, "E18.1.0.90", {"start": v(-40.97, 31.28) * mm, "end": v(-40.97, 26.66) * mm});
            skLineSegment(sketch, "E18.1.0.91", {"start": v(86.03, 31.28) * mm, "end": v(86.03, 26.66) * mm});
            skLineSegment(sketch, "E18.1.0.92", {"start": v(-58.3, 31.28) * mm, "end": v(-53.67, 31.28) * mm});
            skLineSegment(sketch, "E18.1.0.93", {"start": v(106.8, 31.28) * mm, "end": v(106.8, 26.66) * mm});
            skLineSegment(sketch, "E18.1.0.94", {"start": v(-66.38, 43.98) * mm, "end": v(-66.38, 39.36) * mm});
            skLineSegment(sketch, "E18.1.0.95", {"start": v(106.8, 39.36) * mm, "end": v(111.42, 39.36) * mm});
            skLineSegment(sketch, "E18.1.0.96", {"start": v(-15.58, 43.98) * mm, "end": v(-15.58, 39.36) * mm});
            skLineSegment(sketch, "E18.1.0.97", {"start": v(-32.9, 31.28) * mm, "end": v(-28.27, 31.28) * mm});
            skLineSegment(sketch, "E18.1.0.98", {"start": v(35.22, 43.98) * mm, "end": v(35.22, 39.36) * mm});
            skLineSegment(sketch, "E18.1.0.99", {"start": v(86.02, 43.98) * mm, "end": v(86.02, 39.36) * mm});
            skLineSegment(sketch, "E18.1.0.100", {"start": v(68.7, 31.28) * mm, "end": v(68.7, 26.66) * mm});
            skLineSegment(sketch, "E18.1.0.101", {"start": v(30.6, 26.66) * mm, "end": v(35.23, 26.66) * mm});
            skLineSegment(sketch, "E18.1.0.102", {"start": v(68.7, 43.98) * mm, "end": v(68.7, 39.36) * mm});
            skLineSegment(sketch, "E18.1.0.103", {"start": v(-45.6, 39.36) * mm, "end": v(-40.98, 39.36) * mm});
            skLineSegment(sketch, "E18.1.0.104", {"start": v(5.2, 39.36) * mm, "end": v(9.82, 39.36) * mm});
            skLineSegment(sketch, "E18.1.0.105", {"start": v(56, 39.36) * mm, "end": v(60.62, 39.36) * mm});
            skLineSegment(sketch, "E18.1.0.106", {"start": v(-20.2, 31.28) * mm, "end": v(-15.57, 31.28) * mm});
            skLineSegment(sketch, "E18.1.0.107", {"start": v(68.7, 26.66) * mm, "end": v(73.33, 26.66) * mm});
            skLineSegment(sketch, "E18.1.0.108", {"start": v(56, 26.66) * mm, "end": v(60.63, 26.66) * mm});
            skLineSegment(sketch, "E18.1.0.109", {"start": v(111.43, 31.28) * mm, "end": v(111.43, 26.66) * mm});
            skLineSegment(sketch, "E18.1.0.110", {"start": v(56, 43.98) * mm, "end": v(60.62, 43.98) * mm});
            skLineSegment(sketch, "E18.1.0.111", {"start": v(106.8, 43.98) * mm, "end": v(111.42, 43.98) * mm});
            skLineSegment(sketch, "E18.1.0.112", {"start": v(-53.67, 31.28) * mm, "end": v(-53.67, 26.66) * mm});
            skLineSegment(sketch, "E18.1.0.113", {"start": v(-45.6, 43.98) * mm, "end": v(-40.98, 43.98) * mm});
            skLineSegment(sketch, "E18.1.0.114", {"start": v(5.2, 43.98) * mm, "end": v(9.82, 43.98) * mm});
            skLineSegment(sketch, "E18.1.0.115", {"start": v(-15.57, 31.28) * mm, "end": v(-15.57, 26.66) * mm});
            skLineSegment(sketch, "E18.1.0.116", {"start": v(43.3, 31.28) * mm, "end": v(43.3, 26.66) * mm});
            skLineSegment(sketch, "E18.1.0.117", {"start": v(-71, 43.98) * mm, "end": v(-66.38, 43.98) * mm});
            skLineSegment(sketch, "E18.1.0.118", {"start": v(-20.2, 43.98) * mm, "end": v(-15.58, 43.98) * mm});
            skLineSegment(sketch, "E18.1.0.119", {"start": v(30.6, 43.98) * mm, "end": v(35.22, 43.98) * mm});
            skLineSegment(sketch, "E18.1.0.120", {"start": v(81.4, 43.98) * mm, "end": v(86.02, 43.98) * mm});
            skLineSegment(sketch, "E18.1.0.121", {"start": v(81.4, 26.66) * mm, "end": v(86.03, 26.66) * mm});
            skLineSegment(sketch, "E18.1.0.122", {"start": v(5.2, 26.66) * mm, "end": v(9.83, 26.66) * mm});
            skLineSegment(sketch, "E18.1.0.123", {"start": v(60.63, 31.28) * mm, "end": v(60.63, 26.66) * mm});
            skLineSegment(sketch, "E18.1.0.124", {"start": v(43.3, 43.98) * mm, "end": v(43.3, 39.36) * mm});
            skLineSegment(sketch, "E18.1.0.125", {"start": v(94.1, 43.98) * mm, "end": v(94.1, 39.36) * mm});
            skLineSegment(sketch, "E18.1.0.126", {"start": v(-32.9, 26.66) * mm, "end": v(-28.27, 26.66) * mm});
            skLineSegment(sketch, "E18.1.0.127", {"start": v(-32.9, 31.28) * mm, "end": v(-32.9, 26.66) * mm});
            skLineSegment(sketch, "E18.1.0.128", {"start": v(-58.3, 26.66) * mm, "end": v(-53.67, 26.66) * mm});
            skLineSegment(sketch, "E18.1.0.129", {"start": v(-109.1, 18.6) * mm, "end": v(-104.47, 18.6) * mm});
            skLineSegment(sketch, "E18.1.0.130", {"start": v(106.8, 26.66) * mm, "end": v(111.43, 26.66) * mm});
            skLineSegment(sketch, "E18.1.0.132", {"start": v(73.32, 43.98) * mm, "end": v(73.32, 39.36) * mm});
            skLineSegment(sketch, "E18.1.0.133", {"start": v(22.52, 43.98) * mm, "end": v(22.52, 39.36) * mm});
            skLineSegment(sketch, "E18.1.0.134", {"start": v(-28.28, 43.98) * mm, "end": v(-28.28, 39.36) * mm});
            skLineSegment(sketch, "E18.1.0.135", {"start": v(-79.08, 43.98) * mm, "end": v(-79.08, 39.36) * mm});
            skLineSegment(sketch, "E18.1.0.136", {"start": v(-71, 31.28) * mm, "end": v(-66.37, 31.28) * mm});
            skLineSegment(sketch, "E18.1.0.137", {"start": v(68.7, 39.36) * mm, "end": v(73.32, 39.36) * mm});
            skLineSegment(sketch, "E18.1.0.138", {"start": v(17.9, 39.36) * mm, "end": v(22.52, 39.36) * mm});
            skLineSegment(sketch, "E18.1.0.139", {"start": v(-32.9, 39.36) * mm, "end": v(-28.28, 39.36) * mm});
            skLineSegment(sketch, "E18.1.0.140", {"start": v(-83.7, 39.36) * mm, "end": v(-79.08, 39.36) * mm});
            skLineSegment(sketch, "E18.1.0.141", {"start": v(-83.7, 26.66) * mm, "end": v(-79.07, 26.66) * mm});
            skLineSegment(sketch, "E18.1.0.142", {"start": v(-83.7, 31.28) * mm, "end": v(-83.7, 26.66) * mm});
            skLineSegment(sketch, "E18.1.0.143", {"start": v(17.9, 31.28) * mm, "end": v(17.9, 26.66) * mm});
            skLineSegment(sketch, "E18.1.0.144", {"start": v(-91.78, 43.98) * mm, "end": v(-91.78, 39.36) * mm});
            skLineSegment(sketch, "E18.1.0.145", {"start": v(-96.4, 39.36) * mm, "end": v(-91.78, 39.36) * mm});
            skLineSegment(sketch, "E18.1.0.147", {"start": v(-91.77, 31.28) * mm, "end": v(-91.77, 26.66) * mm});
            skLineSegment(sketch, "E18.1.0.148", {"start": v(-96.4, 43.98) * mm, "end": v(-96.4, 39.36) * mm});
            skLineSegment(sketch, "E18.1.0.149", {"start": v(-96.4, 31.28) * mm, "end": v(-91.77, 31.28) * mm});
            skLineSegment(sketch, "E18.1.0.150", {"start": v(-96.4, 43.98) * mm, "end": v(-91.78, 43.98) * mm});
            skLineSegment(sketch, "E18.1.0.151", {"start": v(-109.1, 31.28) * mm, "end": v(-104.47, 31.28) * mm});
            skLineSegment(sketch, "E18.1.0.153", {"start": v(-109.1, 31.28) * mm, "end": v(-109.1, 26.66) * mm});
            skLineSegment(sketch, "E18.1.0.154", {"start": v(-109.1, 31.28) * mm, "end": v(-104.48, 31.28) * mm});
            skLineSegment(sketch, "E18.1.0.155", {"start": v(-104.48, 43.98) * mm, "end": v(-104.48, 39.36) * mm});
            skLineSegment(sketch, "E18.1.0.156", {"start": v(-109.1, 43.98) * mm, "end": v(-109.1, 39.36) * mm});
            skLineSegment(sketch, "E18.1.0.157", {"start": v(-109.1, 43.98) * mm, "end": v(-104.48, 43.98) * mm});
            skLineSegment(sketch, "E18.1.0.158", {"start": v(-109.1, 39.36) * mm, "end": v(-104.48, 39.36) * mm});
            skLineSegment(sketch, "E18.1.0.159", {"start": v(-109.1, 26.66) * mm, "end": v(-104.47, 26.66) * mm});
            skLineSegment(sketch, "E18.1.0.160", {"start": v(-104.48, 31.28) * mm, "end": v(-104.48, 26.66) * mm});
            skLineSegment(sketch, "E18.1.0.161", {"start": v(-109.1, 31.28) * mm, "end": v(-109.1, 26.66) * mm});
            skLineSegment(sketch, "E18.1.0.162", {"start": v(-109.1, 26.66) * mm, "end": v(-104.48, 26.66) * mm});
            skLineSegment(sketch, "E18.1.0.163", {"start": v(-104.47, 31.28) * mm, "end": v(-104.47, 26.66) * mm});
            skPoint(sketch, "E18.2.0.0", {"position": v(-106.77, 16.27) * mm});
            skPoint(sketch, "E18.2.0.1", {"position": v(-106.76, 3.57) * mm});
            skPoint(sketch, "E18.2.0.2", {"position": v(-94.06, 3.57) * mm});
            skPoint(sketch, "E18.2.0.3", {"position": v(-94.07, 16.27) * mm});
            skPoint(sketch, "E18.2.0.6", {"position": v(-106.77, 3.57) * mm});
            skLineSegment(sketch, "E18.2.0.7", {"start": v(-114.85, 24.35) * mm, "end": v(-114.85, 20.3) * mm});
            skLineSegment(sketch, "E18.2.0.8", {"start": v(68.72, 5.88) * mm, "end": v(73.35, 5.88) * mm});
            skLineSegment(sketch, "E18.2.0.9", {"start": v(-2.85, 5.88) * mm, "end": v(-2.85, 1.26) * mm});
            skLineSegment(sketch, "E18.2.0.14", {"start": v(-58.29, 18.58) * mm, "end": v(-58.29, 13.96) * mm});
            skLineSegment(sketch, "E18.2.0.15", {"start": v(-7.49, 18.58) * mm, "end": v(-7.49, 13.96) * mm});
            skLineSegment(sketch, "E18.2.0.16", {"start": v(47.95, 5.88) * mm, "end": v(47.95, 1.26) * mm});
            skLineSegment(sketch, "E18.2.0.17", {"start": v(9.85, 5.88) * mm, "end": v(9.85, 1.26) * mm});
            skLineSegment(sketch, "E18.2.0.18", {"start": v(-7.48, 5.88) * mm, "end": v(-2.85, 5.88) * mm});
            skLineSegment(sketch, "E18.2.0.19", {"start": v(-20.18, 5.88) * mm, "end": v(-20.18, 1.26) * mm});
            skLineSegment(sketch, "E18.2.0.20", {"start": v(-20.18, 1.26) * mm, "end": v(-15.55, 1.26) * mm});
            skLineSegment(sketch, "E18.2.0.21", {"start": v(-83.69, 18.58) * mm, "end": v(-79.06, 18.58) * mm});
            skLineSegment(sketch, "E18.2.0.22", {"start": v(-32.89, 18.58) * mm, "end": v(-28.26, 18.58) * mm});
            skLineSegment(sketch, "E18.2.0.23", {"start": v(17.91, 18.58) * mm, "end": v(22.54, 18.58) * mm});
            skLineSegment(sketch, "E18.2.0.24", {"start": v(68.71, 18.58) * mm, "end": v(73.34, 18.58) * mm});
            skLineSegment(sketch, "E18.2.0.25", {"start": v(35.25, 5.88) * mm, "end": v(35.25, 1.26) * mm});
            skLineSegment(sketch, "E18.2.0.26", {"start": v(56.02, 5.88) * mm, "end": v(60.65, 5.88) * mm});
            skLineSegment(sketch, "E18.2.0.27", {"start": v(56.02, 5.88) * mm, "end": v(56.02, 1.26) * mm});
            skLineSegment(sketch, "E18.2.0.28", {"start": v(43.31, 13.96) * mm, "end": v(47.94, 13.96) * mm});
            skLineSegment(sketch, "E18.2.0.29", {"start": v(94.11, 13.96) * mm, "end": v(98.74, 13.96) * mm});
            skLineSegment(sketch, "E18.2.0.30", {"start": v(-28.25, 5.88) * mm, "end": v(-28.25, 1.26) * mm});
            skLineSegment(sketch, "E18.2.0.31", {"start": v(-58.29, 13.96) * mm, "end": v(-53.66, 13.96) * mm});
            skLineSegment(sketch, "E18.2.0.32", {"start": v(-7.49, 13.96) * mm, "end": v(-2.86, 13.96) * mm});
            skLineSegment(sketch, "E18.2.0.33", {"start": v(81.42, 5.88) * mm, "end": v(81.42, 1.26) * mm});
            skLineSegment(sketch, "E18.2.0.34", {"start": v(43.32, 5.88) * mm, "end": v(47.95, 5.88) * mm});
            skLineSegment(sketch, "E18.2.0.35", {"start": v(43.32, 1.26) * mm, "end": v(47.95, 1.26) * mm});
            skLineSegment(sketch, "E18.2.0.36", {"start": v(5.22, 5.88) * mm, "end": v(5.22, 1.26) * mm});
            skLineSegment(sketch, "E18.2.0.37", {"start": v(94.12, 5.88) * mm, "end": v(94.12, 1.26) * mm});
            skLineSegment(sketch, "E18.2.0.38", {"start": v(47.94, 18.58) * mm, "end": v(47.94, 13.96) * mm});
            skLineSegment(sketch, "E18.2.0.39", {"start": v(98.74, 18.58) * mm, "end": v(98.74, 13.96) * mm});
            skLineSegment(sketch, "E18.2.0.40", {"start": v(30.62, 5.88) * mm, "end": v(30.62, 1.26) * mm});
            skLineSegment(sketch, "E18.2.0.41", {"start": v(-70.98, 1.26) * mm, "end": v(-66.35, 1.26) * mm});
            skLineSegment(sketch, "E18.2.0.42", {"start": v(98.75, 5.88) * mm, "end": v(98.75, 1.26) * mm});
            skLineSegment(sketch, "E18.2.0.43", {"start": v(-53.66, 18.58) * mm, "end": v(-53.66, 13.96) * mm});
            skLineSegment(sketch, "E18.2.0.44", {"start": v(-2.86, 18.58) * mm, "end": v(-2.86, 13.96) * mm});
            skLineSegment(sketch, "E18.2.0.45", {"start": v(106.81, 18.58) * mm, "end": v(106.81, 13.96) * mm});
            skLineSegment(sketch, "E18.2.0.46", {"start": v(94.12, 1.26) * mm, "end": v(98.75, 1.26) * mm});
            skLineSegment(sketch, "E18.2.0.47", {"start": v(94.12, 5.88) * mm, "end": v(98.75, 5.88) * mm});
            skLineSegment(sketch, "E18.2.0.48", {"start": v(-83.68, 5.88) * mm, "end": v(-79.05, 5.88) * mm});
            skLineSegment(sketch, "E18.2.0.49", {"start": v(-45.58, 5.88) * mm, "end": v(-45.58, 1.26) * mm});
            skLineSegment(sketch, "E18.2.0.50", {"start": v(-79.05, 5.88) * mm, "end": v(-79.05, 1.26) * mm});
            skLineSegment(sketch, "E18.2.0.51", {"start": v(17.92, 1.26) * mm, "end": v(22.55, 1.26) * mm});
            skLineSegment(sketch, "E18.2.0.52", {"start": v(-45.59, 18.58) * mm, "end": v(-45.59, 13.96) * mm});
            skLineSegment(sketch, "E18.2.0.53", {"start": v(5.21, 18.58) * mm, "end": v(5.21, 13.96) * mm});
            skLineSegment(sketch, "E18.2.0.54", {"start": v(43.31, 18.58) * mm, "end": v(47.94, 18.58) * mm});
            skLineSegment(sketch, "E18.2.0.55", {"start": v(94.11, 18.58) * mm, "end": v(98.74, 18.58) * mm});
            skLineSegment(sketch, "E18.2.0.56", {"start": v(56.01, 18.58) * mm, "end": v(56.01, 13.96) * mm});
            skLineSegment(sketch, "E18.2.0.57", {"start": v(22.55, 5.88) * mm, "end": v(22.55, 1.26) * mm});
            skLineSegment(sketch, "E18.2.0.58", {"start": v(-58.29, 18.58) * mm, "end": v(-53.66, 18.58) * mm});
            skLineSegment(sketch, "E18.2.0.59", {"start": v(-7.49, 18.58) * mm, "end": v(-2.86, 18.58) * mm});
            skLineSegment(sketch, "E18.2.0.60", {"start": v(-83.69, 18.58) * mm, "end": v(-83.69, 13.96) * mm});
            skLineSegment(sketch, "E18.2.0.61", {"start": v(-58.28, 5.88) * mm, "end": v(-58.28, 1.26) * mm});
            skLineSegment(sketch, "E18.2.0.62", {"start": v(-45.58, 1.26) * mm, "end": v(-40.95, 1.26) * mm});
            skLineSegment(sketch, "E18.2.0.63", {"start": v(-96.38, 1.26) * mm, "end": v(-91.75, 1.26) * mm});
            skLineSegment(sketch, "E18.2.0.64", {"start": v(60.64, 18.58) * mm, "end": v(60.64, 13.96) * mm});
            skLineSegment(sketch, "E18.2.0.65", {"start": v(111.44, 18.58) * mm, "end": v(111.44, 13.96) * mm});
            skLineSegment(sketch, "E18.2.0.66", {"start": v(-7.48, 1.26) * mm, "end": v(-2.85, 1.26) * mm});
            skLineSegment(sketch, "E18.2.0.67", {"start": v(17.92, 5.88) * mm, "end": v(22.55, 5.88) * mm});
            skLineSegment(sketch, "E18.2.0.68", {"start": v(81.42, 5.88) * mm, "end": v(86.05, 5.88) * mm});
            skLineSegment(sketch, "E18.2.0.69", {"start": v(-7.48, 5.88) * mm, "end": v(-7.48, 1.26) * mm});
            skLineSegment(sketch, "E18.2.0.70", {"start": v(73.35, 5.88) * mm, "end": v(73.35, 1.26) * mm});
            skLineSegment(sketch, "E18.2.0.71", {"start": v(-45.58, 5.88) * mm, "end": v(-40.95, 5.88) * mm});
            skLineSegment(sketch, "E18.2.0.72", {"start": v(-70.99, 18.58) * mm, "end": v(-70.99, 13.96) * mm});
            skLineSegment(sketch, "E18.2.0.73", {"start": v(-20.19, 18.58) * mm, "end": v(-20.19, 13.96) * mm});
            skLineSegment(sketch, "E18.2.0.74", {"start": v(30.61, 18.58) * mm, "end": v(30.61, 13.96) * mm});
            skLineSegment(sketch, "E18.2.0.75", {"start": v(81.41, 18.58) * mm, "end": v(81.41, 13.96) * mm});
            skLineSegment(sketch, "E18.2.0.76", {"start": v(-40.96, 18.58) * mm, "end": v(-40.96, 13.96) * mm});
            skLineSegment(sketch, "E18.2.0.77", {"start": v(9.84, 18.58) * mm, "end": v(9.84, 13.96) * mm});
            skLineSegment(sketch, "E18.2.0.78", {"start": v(-32.89, 18.58) * mm, "end": v(-32.89, 13.96) * mm});
            skLineSegment(sketch, "E18.2.0.79", {"start": v(30.62, 5.88) * mm, "end": v(35.25, 5.88) * mm});
            skLineSegment(sketch, "E18.2.0.80", {"start": v(106.82, 5.88) * mm, "end": v(111.45, 5.88) * mm});
            skLineSegment(sketch, "E18.2.0.81", {"start": v(-70.98, 5.88) * mm, "end": v(-70.98, 1.26) * mm});
            skLineSegment(sketch, "E18.2.0.82", {"start": v(5.22, 5.88) * mm, "end": v(9.85, 5.88) * mm});
            skLineSegment(sketch, "E18.2.0.83", {"start": v(-70.99, 13.96) * mm, "end": v(-66.36, 13.96) * mm});
            skLineSegment(sketch, "E18.2.0.84", {"start": v(-20.19, 13.96) * mm, "end": v(-15.56, 13.96) * mm});
            skLineSegment(sketch, "E18.2.0.85", {"start": v(30.61, 13.96) * mm, "end": v(35.24, 13.96) * mm});
            skLineSegment(sketch, "E18.2.0.86", {"start": v(81.41, 13.96) * mm, "end": v(86.04, 13.96) * mm});
            skLineSegment(sketch, "E18.2.0.87", {"start": v(17.91, 18.58) * mm, "end": v(17.91, 13.96) * mm});
            skLineSegment(sketch, "E18.2.0.88", {"start": v(-96.38, 5.88) * mm, "end": v(-96.38, 1.26) * mm});
            skLineSegment(sketch, "E18.2.0.89", {"start": v(-66.35, 5.88) * mm, "end": v(-66.35, 1.26) * mm});
            skLineSegment(sketch, "E18.2.0.90", {"start": v(-40.95, 5.88) * mm, "end": v(-40.95, 1.26) * mm});
            skLineSegment(sketch, "E18.2.0.91", {"start": v(86.05, 5.88) * mm, "end": v(86.05, 1.26) * mm});
            skLineSegment(sketch, "E18.2.0.92", {"start": v(-58.28, 5.88) * mm, "end": v(-53.65, 5.88) * mm});
            skLineSegment(sketch, "E18.2.0.93", {"start": v(106.82, 5.88) * mm, "end": v(106.82, 1.26) * mm});
            skLineSegment(sketch, "E18.2.0.94", {"start": v(-66.36, 18.58) * mm, "end": v(-66.36, 13.96) * mm});
            skLineSegment(sketch, "E18.2.0.95", {"start": v(106.81, 13.96) * mm, "end": v(111.44, 13.96) * mm});
            skLineSegment(sketch, "E18.2.0.96", {"start": v(-15.56, 18.58) * mm, "end": v(-15.56, 13.96) * mm});
            skLineSegment(sketch, "E18.2.0.97", {"start": v(-32.88, 5.88) * mm, "end": v(-28.25, 5.88) * mm});
            skLineSegment(sketch, "E18.2.0.98", {"start": v(35.24, 18.58) * mm, "end": v(35.24, 13.96) * mm});
            skLineSegment(sketch, "E18.2.0.99", {"start": v(86.04, 18.58) * mm, "end": v(86.04, 13.96) * mm});
            skLineSegment(sketch, "E18.2.0.100", {"start": v(68.72, 5.88) * mm, "end": v(68.72, 1.26) * mm});
            skLineSegment(sketch, "E18.2.0.101", {"start": v(30.62, 1.26) * mm, "end": v(35.25, 1.26) * mm});
            skLineSegment(sketch, "E18.2.0.102", {"start": v(68.71, 18.58) * mm, "end": v(68.71, 13.96) * mm});
            skLineSegment(sketch, "E18.2.0.103", {"start": v(-45.59, 13.96) * mm, "end": v(-40.96, 13.96) * mm});
            skLineSegment(sketch, "E18.2.0.104", {"start": v(5.21, 13.96) * mm, "end": v(9.84, 13.96) * mm});
            skLineSegment(sketch, "E18.2.0.105", {"start": v(56.01, 13.96) * mm, "end": v(60.64, 13.96) * mm});
            skLineSegment(sketch, "E18.2.0.106", {"start": v(-20.18, 5.88) * mm, "end": v(-15.55, 5.88) * mm});
            skLineSegment(sketch, "E18.2.0.107", {"start": v(68.72, 1.26) * mm, "end": v(73.35, 1.26) * mm});
            skLineSegment(sketch, "E18.2.0.108", {"start": v(56.02, 1.26) * mm, "end": v(60.65, 1.26) * mm});
            skLineSegment(sketch, "E18.2.0.109", {"start": v(111.45, 5.88) * mm, "end": v(111.45, 1.26) * mm});
            skLineSegment(sketch, "E18.2.0.110", {"start": v(56.01, 18.58) * mm, "end": v(60.64, 18.58) * mm});
            skLineSegment(sketch, "E18.2.0.111", {"start": v(106.81, 18.58) * mm, "end": v(111.44, 18.58) * mm});
            skLineSegment(sketch, "E18.2.0.112", {"start": v(-53.65, 5.88) * mm, "end": v(-53.65, 1.26) * mm});
            skLineSegment(sketch, "E18.2.0.113", {"start": v(-45.59, 18.58) * mm, "end": v(-40.96, 18.58) * mm});
            skLineSegment(sketch, "E18.2.0.114", {"start": v(5.21, 18.58) * mm, "end": v(9.84, 18.58) * mm});
            skLineSegment(sketch, "E18.2.0.115", {"start": v(-15.55, 5.88) * mm, "end": v(-15.55, 1.26) * mm});
            skLineSegment(sketch, "E18.2.0.116", {"start": v(43.32, 5.88) * mm, "end": v(43.32, 1.26) * mm});
            skLineSegment(sketch, "E18.2.0.117", {"start": v(-70.99, 18.58) * mm, "end": v(-66.36, 18.58) * mm});
            skLineSegment(sketch, "E18.2.0.118", {"start": v(-20.19, 18.58) * mm, "end": v(-15.56, 18.58) * mm});
            skLineSegment(sketch, "E18.2.0.119", {"start": v(30.61, 18.58) * mm, "end": v(35.24, 18.58) * mm});
            skLineSegment(sketch, "E18.2.0.120", {"start": v(81.41, 18.58) * mm, "end": v(86.04, 18.58) * mm});
            skLineSegment(sketch, "E18.2.0.121", {"start": v(81.42, 1.26) * mm, "end": v(86.05, 1.26) * mm});
            skLineSegment(sketch, "E18.2.0.122", {"start": v(5.22, 1.26) * mm, "end": v(9.85, 1.26) * mm});
            skLineSegment(sketch, "E18.2.0.123", {"start": v(60.65, 5.88) * mm, "end": v(60.65, 1.26) * mm});
            skLineSegment(sketch, "E18.2.0.124", {"start": v(43.31, 18.58) * mm, "end": v(43.31, 13.96) * mm});
            skLineSegment(sketch, "E18.2.0.125", {"start": v(94.11, 18.58) * mm, "end": v(94.11, 13.96) * mm});
            skLineSegment(sketch, "E18.2.0.126", {"start": v(-32.88, 1.26) * mm, "end": v(-28.25, 1.26) * mm});
            skLineSegment(sketch, "E18.2.0.127", {"start": v(-32.88, 5.88) * mm, "end": v(-32.88, 1.26) * mm});
            skLineSegment(sketch, "E18.2.0.128", {"start": v(-58.28, 1.26) * mm, "end": v(-53.65, 1.26) * mm});
            skLineSegment(sketch, "E18.2.0.129", {"start": v(-109.08, -6.8) * mm, "end": v(-104.45, -6.8) * mm});
            skLineSegment(sketch, "E18.2.0.130", {"start": v(106.82, 1.26) * mm, "end": v(111.45, 1.26) * mm});
            skLineSegment(sketch, "E18.2.0.132", {"start": v(73.34, 18.58) * mm, "end": v(73.34, 13.96) * mm});
            skLineSegment(sketch, "E18.2.0.133", {"start": v(22.54, 18.58) * mm, "end": v(22.54, 13.96) * mm});
            skLineSegment(sketch, "E18.2.0.134", {"start": v(-28.26, 18.58) * mm, "end": v(-28.26, 13.96) * mm});
            skLineSegment(sketch, "E18.2.0.135", {"start": v(-79.06, 18.58) * mm, "end": v(-79.06, 13.96) * mm});
            skLineSegment(sketch, "E18.2.0.136", {"start": v(-70.98, 5.88) * mm, "end": v(-66.35, 5.88) * mm});
            skLineSegment(sketch, "E18.2.0.137", {"start": v(68.71, 13.96) * mm, "end": v(73.34, 13.96) * mm});
            skLineSegment(sketch, "E18.2.0.138", {"start": v(17.91, 13.96) * mm, "end": v(22.54, 13.96) * mm});
            skLineSegment(sketch, "E18.2.0.139", {"start": v(-32.89, 13.96) * mm, "end": v(-28.26, 13.96) * mm});
            skLineSegment(sketch, "E18.2.0.140", {"start": v(-83.69, 13.96) * mm, "end": v(-79.06, 13.96) * mm});
            skLineSegment(sketch, "E18.2.0.141", {"start": v(-83.68, 1.26) * mm, "end": v(-79.05, 1.26) * mm});
            skLineSegment(sketch, "E18.2.0.142", {"start": v(-83.68, 5.88) * mm, "end": v(-83.68, 1.26) * mm});
            skLineSegment(sketch, "E18.2.0.143", {"start": v(17.92, 5.88) * mm, "end": v(17.92, 1.26) * mm});
            skLineSegment(sketch, "E18.2.0.144", {"start": v(-91.76, 18.58) * mm, "end": v(-91.76, 13.96) * mm});
            skLineSegment(sketch, "E18.2.0.145", {"start": v(-96.39, 13.96) * mm, "end": v(-91.76, 13.96) * mm});
            skLineSegment(sketch, "E18.2.0.147", {"start": v(-91.75, 5.88) * mm, "end": v(-91.75, 1.26) * mm});
            skLineSegment(sketch, "E18.2.0.148", {"start": v(-96.39, 18.58) * mm, "end": v(-96.39, 13.96) * mm});
            skLineSegment(sketch, "E18.2.0.149", {"start": v(-96.38, 5.88) * mm, "end": v(-91.75, 5.88) * mm});
            skLineSegment(sketch, "E18.2.0.150", {"start": v(-96.39, 18.58) * mm, "end": v(-91.76, 18.58) * mm});
            skLineSegment(sketch, "E18.2.0.151", {"start": v(-109.08, 5.88) * mm, "end": v(-104.45, 5.88) * mm});
            skLineSegment(sketch, "E18.2.0.153", {"start": v(-109.08, 5.88) * mm, "end": v(-109.08, 1.26) * mm});
            skLineSegment(sketch, "E18.2.0.154", {"start": v(-109.09, 5.88) * mm, "end": v(-104.46, 5.88) * mm});
            skLineSegment(sketch, "E18.2.0.155", {"start": v(-104.46, 18.58) * mm, "end": v(-104.46, 13.96) * mm});
            skLineSegment(sketch, "E18.2.0.156", {"start": v(-109.09, 18.58) * mm, "end": v(-109.09, 13.96) * mm});
            skLineSegment(sketch, "E18.2.0.157", {"start": v(-109.09, 18.58) * mm, "end": v(-104.46, 18.58) * mm});
            skLineSegment(sketch, "E18.2.0.158", {"start": v(-109.09, 13.96) * mm, "end": v(-104.46, 13.96) * mm});
            skLineSegment(sketch, "E18.2.0.159", {"start": v(-109.08, 1.26) * mm, "end": v(-104.45, 1.26) * mm});
            skLineSegment(sketch, "E18.2.0.160", {"start": v(-104.46, 5.88) * mm, "end": v(-104.46, 1.26) * mm});
            skLineSegment(sketch, "E18.2.0.161", {"start": v(-109.09, 5.88) * mm, "end": v(-109.09, 1.26) * mm});
            skLineSegment(sketch, "E18.2.0.162", {"start": v(-109.09, 1.26) * mm, "end": v(-104.46, 1.26) * mm});
            skLineSegment(sketch, "E18.2.0.163", {"start": v(-104.45, 5.88) * mm, "end": v(-104.45, 1.26) * mm});
            skPoint(sketch, "E18.3.0.0", {"position": v(-106.76, -9.13) * mm});
            skPoint(sketch, "E18.3.0.1", {"position": v(-106.75, -21.83) * mm});
            skPoint(sketch, "E18.3.0.2", {"position": v(-94.05, -21.83) * mm});
            skPoint(sketch, "E18.3.0.3", {"position": v(-94.06, -9.13) * mm});
            skPoint(sketch, "E18.3.0.6", {"position": v(-106.76, -21.83) * mm});
            skLineSegment(sketch, "E18.3.0.8", {"start": v(68.74, -19.52) * mm, "end": v(73.37, -19.52) * mm});
            skLineSegment(sketch, "E18.3.0.9", {"start": v(-2.83, -19.52) * mm, "end": v(-2.83, -24.14) * mm});
            skLineSegment(sketch, "E18.3.0.14", {"start": v(-58.27, -6.82) * mm, "end": v(-58.27, -11.44) * mm});
            skLineSegment(sketch, "E18.3.0.15", {"start": v(-7.47, -6.82) * mm, "end": v(-7.47, -11.44) * mm});
            skLineSegment(sketch, "E18.3.0.16", {"start": v(47.97, -19.52) * mm, "end": v(47.97, -24.14) * mm});
            skLineSegment(sketch, "E18.3.0.17", {"start": v(9.87, -19.52) * mm, "end": v(9.87, -24.14) * mm});
            skLineSegment(sketch, "E18.3.0.18", {"start": v(-7.46, -19.52) * mm, "end": v(-2.83, -19.52) * mm});
            skLineSegment(sketch, "E18.3.0.19", {"start": v(-20.16, -19.52) * mm, "end": v(-20.16, -24.14) * mm});
            skLineSegment(sketch, "E18.3.0.20", {"start": v(-20.16, -24.14) * mm, "end": v(-15.53, -24.14) * mm});
            skLineSegment(sketch, "E18.3.0.21", {"start": v(-83.67, -6.82) * mm, "end": v(-79.04, -6.82) * mm});
            skLineSegment(sketch, "E18.3.0.22", {"start": v(-32.87, -6.82) * mm, "end": v(-28.24, -6.82) * mm});
            skLineSegment(sketch, "E18.3.0.23", {"start": v(17.93, -6.82) * mm, "end": v(22.56, -6.82) * mm});
            skLineSegment(sketch, "E18.3.0.24", {"start": v(68.73, -6.82) * mm, "end": v(73.36, -6.82) * mm});
            skLineSegment(sketch, "E18.3.0.25", {"start": v(35.27, -19.52) * mm, "end": v(35.27, -24.14) * mm});
            skLineSegment(sketch, "E18.3.0.26", {"start": v(56.04, -19.52) * mm, "end": v(60.67, -19.52) * mm});
            skLineSegment(sketch, "E18.3.0.27", {"start": v(56.04, -19.52) * mm, "end": v(56.04, -24.14) * mm});
            skLineSegment(sketch, "E18.3.0.28", {"start": v(43.33, -11.44) * mm, "end": v(47.96, -11.44) * mm});
            skLineSegment(sketch, "E18.3.0.29", {"start": v(94.13, -11.44) * mm, "end": v(98.76, -11.44) * mm});
            skLineSegment(sketch, "E18.3.0.30", {"start": v(-28.23, -19.52) * mm, "end": v(-28.23, -24.14) * mm});
            skLineSegment(sketch, "E18.3.0.31", {"start": v(-58.27, -11.44) * mm, "end": v(-53.64, -11.44) * mm});
            skLineSegment(sketch, "E18.3.0.32", {"start": v(-7.47, -11.44) * mm, "end": v(-2.84, -11.44) * mm});
            skLineSegment(sketch, "E18.3.0.33", {"start": v(81.44, -19.52) * mm, "end": v(81.44, -24.14) * mm});
            skLineSegment(sketch, "E18.3.0.34", {"start": v(43.34, -19.52) * mm, "end": v(47.97, -19.52) * mm});
            skLineSegment(sketch, "E18.3.0.35", {"start": v(43.34, -24.14) * mm, "end": v(47.97, -24.14) * mm});
            skLineSegment(sketch, "E18.3.0.36", {"start": v(5.24, -19.52) * mm, "end": v(5.24, -24.14) * mm});
            skLineSegment(sketch, "E18.3.0.37", {"start": v(94.14, -19.52) * mm, "end": v(94.14, -24.14) * mm});
            skLineSegment(sketch, "E18.3.0.38", {"start": v(47.96, -6.82) * mm, "end": v(47.96, -11.44) * mm});
            skLineSegment(sketch, "E18.3.0.39", {"start": v(98.76, -6.82) * mm, "end": v(98.76, -11.44) * mm});
            skLineSegment(sketch, "E18.3.0.40", {"start": v(30.64, -19.52) * mm, "end": v(30.64, -24.14) * mm});
            skLineSegment(sketch, "E18.3.0.41", {"start": v(-70.96, -24.14) * mm, "end": v(-66.33, -24.14) * mm});
            skLineSegment(sketch, "E18.3.0.42", {"start": v(98.77, -19.52) * mm, "end": v(98.77, -24.14) * mm});
            skLineSegment(sketch, "E18.3.0.43", {"start": v(-53.64, -6.82) * mm, "end": v(-53.64, -11.44) * mm});
            skLineSegment(sketch, "E18.3.0.44", {"start": v(-2.84, -6.82) * mm, "end": v(-2.84, -11.44) * mm});
            skLineSegment(sketch, "E18.3.0.45", {"start": v(106.83, -6.82) * mm, "end": v(106.83, -11.44) * mm});
            skLineSegment(sketch, "E18.3.0.46", {"start": v(94.14, -24.14) * mm, "end": v(98.77, -24.14) * mm});
            skLineSegment(sketch, "E18.3.0.47", {"start": v(94.14, -19.52) * mm, "end": v(98.77, -19.52) * mm});
            skLineSegment(sketch, "E18.3.0.48", {"start": v(-83.66, -19.52) * mm, "end": v(-79.03, -19.52) * mm});
            skLineSegment(sketch, "E18.3.0.49", {"start": v(-45.56, -19.52) * mm, "end": v(-45.56, -24.14) * mm});
            skLineSegment(sketch, "E18.3.0.50", {"start": v(-79.03, -19.52) * mm, "end": v(-79.03, -24.14) * mm});
            skLineSegment(sketch, "E18.3.0.51", {"start": v(17.94, -24.14) * mm, "end": v(22.57, -24.14) * mm});
            skLineSegment(sketch, "E18.3.0.52", {"start": v(-45.57, -6.82) * mm, "end": v(-45.57, -11.44) * mm});
            skLineSegment(sketch, "E18.3.0.53", {"start": v(5.23, -6.82) * mm, "end": v(5.23, -11.44) * mm});
            skLineSegment(sketch, "E18.3.0.54", {"start": v(43.33, -6.82) * mm, "end": v(47.96, -6.82) * mm});
            skLineSegment(sketch, "E18.3.0.55", {"start": v(94.13, -6.82) * mm, "end": v(98.76, -6.82) * mm});
            skLineSegment(sketch, "E18.3.0.56", {"start": v(56.03, -6.82) * mm, "end": v(56.03, -11.44) * mm});
            skLineSegment(sketch, "E18.3.0.57", {"start": v(22.57, -19.52) * mm, "end": v(22.57, -24.14) * mm});
            skLineSegment(sketch, "E18.3.0.58", {"start": v(-58.27, -6.82) * mm, "end": v(-53.64, -6.82) * mm});
            skLineSegment(sketch, "E18.3.0.59", {"start": v(-7.47, -6.82) * mm, "end": v(-2.84, -6.82) * mm});
            skLineSegment(sketch, "E18.3.0.60", {"start": v(-83.67, -6.82) * mm, "end": v(-83.67, -11.44) * mm});
            skLineSegment(sketch, "E18.3.0.61", {"start": v(-58.26, -19.52) * mm, "end": v(-58.26, -24.14) * mm});
            skLineSegment(sketch, "E18.3.0.62", {"start": v(-45.56, -24.14) * mm, "end": v(-40.93, -24.14) * mm});
            skLineSegment(sketch, "E18.3.0.63", {"start": v(-96.36, -24.14) * mm, "end": v(-91.73, -24.14) * mm});
            skLineSegment(sketch, "E18.3.0.64", {"start": v(60.66, -6.82) * mm, "end": v(60.66, -11.44) * mm});
            skLineSegment(sketch, "E18.3.0.65", {"start": v(111.46, -6.82) * mm, "end": v(111.46, -11.44) * mm});
            skLineSegment(sketch, "E18.3.0.66", {"start": v(-7.46, -24.14) * mm, "end": v(-2.83, -24.14) * mm});
            skLineSegment(sketch, "E18.3.0.67", {"start": v(17.94, -19.52) * mm, "end": v(22.57, -19.52) * mm});
            skLineSegment(sketch, "E18.3.0.68", {"start": v(81.44, -19.52) * mm, "end": v(86.07, -19.52) * mm});
            skLineSegment(sketch, "E18.3.0.69", {"start": v(-7.46, -19.52) * mm, "end": v(-7.46, -24.14) * mm});
            skLineSegment(sketch, "E18.3.0.70", {"start": v(73.37, -19.52) * mm, "end": v(73.37, -24.14) * mm});
            skLineSegment(sketch, "E18.3.0.71", {"start": v(-45.56, -19.52) * mm, "end": v(-40.93, -19.52) * mm});
            skLineSegment(sketch, "E18.3.0.72", {"start": v(-70.97, -6.82) * mm, "end": v(-70.97, -11.44) * mm});
            skLineSegment(sketch, "E18.3.0.73", {"start": v(-20.17, -6.82) * mm, "end": v(-20.17, -11.44) * mm});
            skLineSegment(sketch, "E18.3.0.74", {"start": v(30.63, -6.82) * mm, "end": v(30.63, -11.44) * mm});
            skLineSegment(sketch, "E18.3.0.75", {"start": v(81.43, -6.82) * mm, "end": v(81.43, -11.44) * mm});
            skLineSegment(sketch, "E18.3.0.76", {"start": v(-40.94, -6.82) * mm, "end": v(-40.94, -11.44) * mm});
            skLineSegment(sketch, "E18.3.0.77", {"start": v(9.86, -6.82) * mm, "end": v(9.86, -11.44) * mm});
            skLineSegment(sketch, "E18.3.0.78", {"start": v(-32.87, -6.82) * mm, "end": v(-32.87, -11.44) * mm});
            skLineSegment(sketch, "E18.3.0.79", {"start": v(30.64, -19.52) * mm, "end": v(35.27, -19.52) * mm});
            skLineSegment(sketch, "E18.3.0.80", {"start": v(106.84, -19.52) * mm, "end": v(111.47, -19.52) * mm});
            skLineSegment(sketch, "E18.3.0.81", {"start": v(-70.96, -19.52) * mm, "end": v(-70.96, -24.14) * mm});
            skLineSegment(sketch, "E18.3.0.82", {"start": v(5.24, -19.52) * mm, "end": v(9.87, -19.52) * mm});
            skLineSegment(sketch, "E18.3.0.83", {"start": v(-70.97, -11.44) * mm, "end": v(-66.34, -11.44) * mm});
            skLineSegment(sketch, "E18.3.0.84", {"start": v(-20.17, -11.44) * mm, "end": v(-15.54, -11.44) * mm});
            skLineSegment(sketch, "E18.3.0.85", {"start": v(30.63, -11.44) * mm, "end": v(35.26, -11.44) * mm});
            skLineSegment(sketch, "E18.3.0.86", {"start": v(81.43, -11.44) * mm, "end": v(86.06, -11.44) * mm});
            skLineSegment(sketch, "E18.3.0.87", {"start": v(17.93, -6.82) * mm, "end": v(17.93, -11.44) * mm});
            skLineSegment(sketch, "E18.3.0.88", {"start": v(-96.36, -19.52) * mm, "end": v(-96.36, -24.14) * mm});
            skLineSegment(sketch, "E18.3.0.89", {"start": v(-66.33, -19.52) * mm, "end": v(-66.33, -24.14) * mm});
            skLineSegment(sketch, "E18.3.0.90", {"start": v(-40.93, -19.52) * mm, "end": v(-40.93, -24.14) * mm});
            skLineSegment(sketch, "E18.3.0.91", {"start": v(86.07, -19.52) * mm, "end": v(86.07, -24.14) * mm});
            skLineSegment(sketch, "E18.3.0.92", {"start": v(-58.26, -19.52) * mm, "end": v(-53.63, -19.52) * mm});
            skLineSegment(sketch, "E18.3.0.93", {"start": v(106.84, -19.52) * mm, "end": v(106.84, -24.14) * mm});
            skLineSegment(sketch, "E18.3.0.94", {"start": v(-66.34, -6.82) * mm, "end": v(-66.34, -11.44) * mm});
            skLineSegment(sketch, "E18.3.0.95", {"start": v(106.83, -11.44) * mm, "end": v(111.46, -11.44) * mm});
            skLineSegment(sketch, "E18.3.0.96", {"start": v(-15.54, -6.82) * mm, "end": v(-15.54, -11.44) * mm});
            skLineSegment(sketch, "E18.3.0.97", {"start": v(-32.86, -19.52) * mm, "end": v(-28.23, -19.52) * mm});
            skLineSegment(sketch, "E18.3.0.98", {"start": v(35.26, -6.82) * mm, "end": v(35.26, -11.44) * mm});
            skLineSegment(sketch, "E18.3.0.99", {"start": v(86.06, -6.82) * mm, "end": v(86.06, -11.44) * mm});
            skLineSegment(sketch, "E18.3.0.100", {"start": v(68.74, -19.52) * mm, "end": v(68.74, -24.14) * mm});
            skLineSegment(sketch, "E18.3.0.101", {"start": v(30.64, -24.14) * mm, "end": v(35.27, -24.14) * mm});
            skLineSegment(sketch, "E18.3.0.102", {"start": v(68.73, -6.82) * mm, "end": v(68.73, -11.44) * mm});
            skLineSegment(sketch, "E18.3.0.103", {"start": v(-45.57, -11.44) * mm, "end": v(-40.94, -11.44) * mm});
            skLineSegment(sketch, "E18.3.0.104", {"start": v(5.23, -11.44) * mm, "end": v(9.86, -11.44) * mm});
            skLineSegment(sketch, "E18.3.0.105", {"start": v(56.03, -11.44) * mm, "end": v(60.66, -11.44) * mm});
            skLineSegment(sketch, "E18.3.0.106", {"start": v(-20.16, -19.52) * mm, "end": v(-15.53, -19.52) * mm});
            skLineSegment(sketch, "E18.3.0.107", {"start": v(68.74, -24.14) * mm, "end": v(73.37, -24.14) * mm});
            skLineSegment(sketch, "E18.3.0.108", {"start": v(56.04, -24.14) * mm, "end": v(60.67, -24.14) * mm});
            skLineSegment(sketch, "E18.3.0.109", {"start": v(111.47, -19.52) * mm, "end": v(111.47, -24.14) * mm});
            skLineSegment(sketch, "E18.3.0.110", {"start": v(56.03, -6.82) * mm, "end": v(60.66, -6.82) * mm});
            skLineSegment(sketch, "E18.3.0.111", {"start": v(106.83, -6.82) * mm, "end": v(111.46, -6.82) * mm});
            skLineSegment(sketch, "E18.3.0.112", {"start": v(-53.63, -19.52) * mm, "end": v(-53.63, -24.14) * mm});
            skLineSegment(sketch, "E18.3.0.113", {"start": v(-45.57, -6.82) * mm, "end": v(-40.94, -6.82) * mm});
            skLineSegment(sketch, "E18.3.0.114", {"start": v(5.23, -6.82) * mm, "end": v(9.86, -6.82) * mm});
            skLineSegment(sketch, "E18.3.0.115", {"start": v(-15.53, -19.52) * mm, "end": v(-15.53, -24.14) * mm});
            skLineSegment(sketch, "E18.3.0.116", {"start": v(43.34, -19.52) * mm, "end": v(43.34, -24.14) * mm});
            skLineSegment(sketch, "E18.3.0.117", {"start": v(-70.97, -6.82) * mm, "end": v(-66.34, -6.82) * mm});
            skLineSegment(sketch, "E18.3.0.118", {"start": v(-20.17, -6.82) * mm, "end": v(-15.54, -6.82) * mm});
            skLineSegment(sketch, "E18.3.0.119", {"start": v(30.63, -6.82) * mm, "end": v(35.26, -6.82) * mm});
            skLineSegment(sketch, "E18.3.0.120", {"start": v(81.43, -6.82) * mm, "end": v(86.06, -6.82) * mm});
            skLineSegment(sketch, "E18.3.0.121", {"start": v(81.44, -24.14) * mm, "end": v(86.07, -24.14) * mm});
            skLineSegment(sketch, "E18.3.0.122", {"start": v(5.24, -24.14) * mm, "end": v(9.87, -24.14) * mm});
            skLineSegment(sketch, "E18.3.0.123", {"start": v(60.67, -19.52) * mm, "end": v(60.67, -24.14) * mm});
            skLineSegment(sketch, "E18.3.0.124", {"start": v(43.33, -6.82) * mm, "end": v(43.33, -11.44) * mm});
            skLineSegment(sketch, "E18.3.0.125", {"start": v(94.13, -6.82) * mm, "end": v(94.13, -11.44) * mm});
            skLineSegment(sketch, "E18.3.0.126", {"start": v(-32.86, -24.14) * mm, "end": v(-28.23, -24.14) * mm});
            skLineSegment(sketch, "E18.3.0.127", {"start": v(-32.86, -19.52) * mm, "end": v(-32.86, -24.14) * mm});
            skLineSegment(sketch, "E18.3.0.128", {"start": v(-58.26, -24.14) * mm, "end": v(-53.63, -24.14) * mm});
            skLineSegment(sketch, "E18.3.0.129", {"start": v(-109.06, -32.2) * mm, "end": v(-104.43, -32.2) * mm});
            skLineSegment(sketch, "E18.3.0.130", {"start": v(106.84, -24.14) * mm, "end": v(111.47, -24.14) * mm});
            skLineSegment(sketch, "E18.3.0.132", {"start": v(73.36, -6.82) * mm, "end": v(73.36, -11.44) * mm});
            skLineSegment(sketch, "E18.3.0.133", {"start": v(22.56, -6.82) * mm, "end": v(22.56, -11.44) * mm});
            skLineSegment(sketch, "E18.3.0.134", {"start": v(-28.24, -6.82) * mm, "end": v(-28.24, -11.44) * mm});
            skLineSegment(sketch, "E18.3.0.135", {"start": v(-79.04, -6.82) * mm, "end": v(-79.04, -11.44) * mm});
            skLineSegment(sketch, "E18.3.0.136", {"start": v(-70.96, -19.52) * mm, "end": v(-66.33, -19.52) * mm});
            skLineSegment(sketch, "E18.3.0.137", {"start": v(68.73, -11.44) * mm, "end": v(73.36, -11.44) * mm});
            skLineSegment(sketch, "E18.3.0.138", {"start": v(17.93, -11.44) * mm, "end": v(22.56, -11.44) * mm});
            skLineSegment(sketch, "E18.3.0.139", {"start": v(-32.87, -11.44) * mm, "end": v(-28.24, -11.44) * mm});
            skLineSegment(sketch, "E18.3.0.140", {"start": v(-83.67, -11.44) * mm, "end": v(-79.04, -11.44) * mm});
            skLineSegment(sketch, "E18.3.0.141", {"start": v(-83.66, -24.14) * mm, "end": v(-79.03, -24.14) * mm});
            skLineSegment(sketch, "E18.3.0.142", {"start": v(-83.66, -19.52) * mm, "end": v(-83.66, -24.14) * mm});
            skLineSegment(sketch, "E18.3.0.143", {"start": v(17.94, -19.52) * mm, "end": v(17.94, -24.14) * mm});
            skLineSegment(sketch, "E18.3.0.144", {"start": v(-91.74, -6.82) * mm, "end": v(-91.74, -11.44) * mm});
            skLineSegment(sketch, "E18.3.0.145", {"start": v(-96.37, -11.44) * mm, "end": v(-91.74, -11.44) * mm});
            skLineSegment(sketch, "E18.3.0.147", {"start": v(-91.73, -19.52) * mm, "end": v(-91.73, -24.14) * mm});
            skLineSegment(sketch, "E18.3.0.148", {"start": v(-96.37, -6.82) * mm, "end": v(-96.37, -11.44) * mm});
            skLineSegment(sketch, "E18.3.0.149", {"start": v(-96.36, -19.52) * mm, "end": v(-91.73, -19.52) * mm});
            skLineSegment(sketch, "E18.3.0.150", {"start": v(-96.37, -6.82) * mm, "end": v(-91.74, -6.82) * mm});
            skLineSegment(sketch, "E18.3.0.151", {"start": v(-109.06, -19.52) * mm, "end": v(-104.43, -19.52) * mm});
            skLineSegment(sketch, "E18.3.0.153", {"start": v(-109.06, -19.52) * mm, "end": v(-109.06, -24.14) * mm});
            skLineSegment(sketch, "E18.3.0.154", {"start": v(-109.07, -19.52) * mm, "end": v(-104.44, -19.52) * mm});
            skLineSegment(sketch, "E18.3.0.155", {"start": v(-104.44, -6.82) * mm, "end": v(-104.44, -11.44) * mm});
            skLineSegment(sketch, "E18.3.0.156", {"start": v(-109.07, -6.82) * mm, "end": v(-109.07, -11.44) * mm});
            skLineSegment(sketch, "E18.3.0.157", {"start": v(-109.07, -6.82) * mm, "end": v(-104.44, -6.82) * mm});
            skLineSegment(sketch, "E18.3.0.158", {"start": v(-109.07, -11.44) * mm, "end": v(-104.44, -11.44) * mm});
            skLineSegment(sketch, "E18.3.0.159", {"start": v(-109.06, -24.14) * mm, "end": v(-104.43, -24.14) * mm});
            skLineSegment(sketch, "E18.3.0.160", {"start": v(-104.44, -19.52) * mm, "end": v(-104.44, -24.14) * mm});
            skLineSegment(sketch, "E18.3.0.161", {"start": v(-109.07, -19.52) * mm, "end": v(-109.07, -24.14) * mm});
            skLineSegment(sketch, "E18.3.0.162", {"start": v(-109.07, -24.14) * mm, "end": v(-104.44, -24.14) * mm});
            skLineSegment(sketch, "E18.3.0.163", {"start": v(-104.43, -19.52) * mm, "end": v(-104.43, -24.14) * mm});
            skPoint(sketch, "E18.4.0.0", {"position": v(-106.74, -34.53) * mm});
            skPoint(sketch, "E18.4.0.1", {"position": v(-106.73, -47.23) * mm});
            skPoint(sketch, "E18.4.0.2", {"position": v(-94.03, -47.23) * mm});
            skPoint(sketch, "E18.4.0.3", {"position": v(-94.04, -34.53) * mm});
            skPoint(sketch, "E18.4.0.6", {"position": v(-106.74, -47.23) * mm});
            skLineSegment(sketch, "E18.4.0.8", {"start": v(68.76, -44.92) * mm, "end": v(73.38, -44.92) * mm});
            skLineSegment(sketch, "E18.4.0.9", {"start": v(-2.82, -44.92) * mm, "end": v(-2.82, -49.54) * mm});
            skLineSegment(sketch, "E18.4.0.14", {"start": v(-58.25, -32.22) * mm, "end": v(-58.25, -36.84) * mm});
            skLineSegment(sketch, "E18.4.0.15", {"start": v(-7.45, -32.22) * mm, "end": v(-7.45, -36.84) * mm});
            skLineSegment(sketch, "E18.4.0.16", {"start": v(47.98, -44.92) * mm, "end": v(47.98, -49.54) * mm});
            skLineSegment(sketch, "E18.4.0.17", {"start": v(9.88, -44.92) * mm, "end": v(9.88, -49.54) * mm});
            skLineSegment(sketch, "E18.4.0.18", {"start": v(-7.44, -44.92) * mm, "end": v(-2.82, -44.92) * mm});
            skLineSegment(sketch, "E18.4.0.19", {"start": v(-20.14, -44.92) * mm, "end": v(-20.14, -49.54) * mm});
            skLineSegment(sketch, "E18.4.0.20", {"start": v(-20.14, -49.54) * mm, "end": v(-15.52, -49.54) * mm});
            skLineSegment(sketch, "E18.4.0.21", {"start": v(-83.65, -32.22) * mm, "end": v(-79.03, -32.22) * mm});
            skLineSegment(sketch, "E18.4.0.22", {"start": v(-32.85, -32.22) * mm, "end": v(-28.23, -32.22) * mm});
            skLineSegment(sketch, "E18.4.0.23", {"start": v(17.95, -32.22) * mm, "end": v(22.57, -32.22) * mm});
            skLineSegment(sketch, "E18.4.0.24", {"start": v(68.75, -32.22) * mm, "end": v(73.37, -32.22) * mm});
            skLineSegment(sketch, "E18.4.0.25", {"start": v(35.28, -44.92) * mm, "end": v(35.28, -49.54) * mm});
            skLineSegment(sketch, "E18.4.0.26", {"start": v(56.06, -44.92) * mm, "end": v(60.68, -44.92) * mm});
            skLineSegment(sketch, "E18.4.0.27", {"start": v(56.06, -44.92) * mm, "end": v(56.06, -49.54) * mm});
            skLineSegment(sketch, "E18.4.0.28", {"start": v(43.35, -36.84) * mm, "end": v(47.97, -36.84) * mm});
            skLineSegment(sketch, "E18.4.0.29", {"start": v(94.15, -36.84) * mm, "end": v(98.77, -36.84) * mm});
            skLineSegment(sketch, "E18.4.0.30", {"start": v(-28.22, -44.92) * mm, "end": v(-28.22, -49.54) * mm});
            skLineSegment(sketch, "E18.4.0.31", {"start": v(-58.25, -36.84) * mm, "end": v(-53.63, -36.84) * mm});
            skLineSegment(sketch, "E18.4.0.32", {"start": v(-7.45, -36.84) * mm, "end": v(-2.83, -36.84) * mm});
            skLineSegment(sketch, "E18.4.0.33", {"start": v(81.46, -44.92) * mm, "end": v(81.46, -49.54) * mm});
            skLineSegment(sketch, "E18.4.0.34", {"start": v(43.36, -44.92) * mm, "end": v(47.98, -44.92) * mm});
            skLineSegment(sketch, "E18.4.0.35", {"start": v(43.36, -49.54) * mm, "end": v(47.98, -49.54) * mm});
            skLineSegment(sketch, "E18.4.0.36", {"start": v(5.26, -44.92) * mm, "end": v(5.26, -49.54) * mm});
            skLineSegment(sketch, "E18.4.0.37", {"start": v(94.16, -44.92) * mm, "end": v(94.16, -49.54) * mm});
            skLineSegment(sketch, "E18.4.0.38", {"start": v(47.97, -32.22) * mm, "end": v(47.97, -36.84) * mm});
            skLineSegment(sketch, "E18.4.0.39", {"start": v(98.77, -32.22) * mm, "end": v(98.77, -36.84) * mm});
            skLineSegment(sketch, "E18.4.0.40", {"start": v(30.66, -44.92) * mm, "end": v(30.66, -49.54) * mm});
            skLineSegment(sketch, "E18.4.0.41", {"start": v(-70.94, -49.54) * mm, "end": v(-66.32, -49.54) * mm});
            skLineSegment(sketch, "E18.4.0.42", {"start": v(98.78, -44.92) * mm, "end": v(98.78, -49.54) * mm});
            skLineSegment(sketch, "E18.4.0.43", {"start": v(-53.63, -32.22) * mm, "end": v(-53.63, -36.84) * mm});
            skLineSegment(sketch, "E18.4.0.44", {"start": v(-2.83, -32.22) * mm, "end": v(-2.83, -36.84) * mm});
            skLineSegment(sketch, "E18.4.0.45", {"start": v(106.85, -32.22) * mm, "end": v(106.85, -36.84) * mm});
            skLineSegment(sketch, "E18.4.0.46", {"start": v(94.16, -49.54) * mm, "end": v(98.78, -49.54) * mm});
            skLineSegment(sketch, "E18.4.0.47", {"start": v(94.16, -44.92) * mm, "end": v(98.78, -44.92) * mm});
            skLineSegment(sketch, "E18.4.0.48", {"start": v(-83.64, -44.92) * mm, "end": v(-79.02, -44.92) * mm});
            skLineSegment(sketch, "E18.4.0.49", {"start": v(-45.54, -44.92) * mm, "end": v(-45.54, -49.54) * mm});
            skLineSegment(sketch, "E18.4.0.50", {"start": v(-79.02, -44.92) * mm, "end": v(-79.02, -49.54) * mm});
            skLineSegment(sketch, "E18.4.0.51", {"start": v(17.96, -49.54) * mm, "end": v(22.58, -49.54) * mm});
            skLineSegment(sketch, "E18.4.0.52", {"start": v(-45.55, -32.22) * mm, "end": v(-45.55, -36.84) * mm});
            skLineSegment(sketch, "E18.4.0.53", {"start": v(5.25, -32.22) * mm, "end": v(5.25, -36.84) * mm});
            skLineSegment(sketch, "E18.4.0.54", {"start": v(43.35, -32.22) * mm, "end": v(47.97, -32.22) * mm});
            skLineSegment(sketch, "E18.4.0.55", {"start": v(94.15, -32.22) * mm, "end": v(98.77, -32.22) * mm});
            skLineSegment(sketch, "E18.4.0.56", {"start": v(56.05, -32.22) * mm, "end": v(56.05, -36.84) * mm});
            skLineSegment(sketch, "E18.4.0.57", {"start": v(22.58, -44.92) * mm, "end": v(22.58, -49.54) * mm});
            skLineSegment(sketch, "E18.4.0.58", {"start": v(-58.25, -32.22) * mm, "end": v(-53.63, -32.22) * mm});
            skLineSegment(sketch, "E18.4.0.59", {"start": v(-7.45, -32.22) * mm, "end": v(-2.83, -32.22) * mm});
            skLineSegment(sketch, "E18.4.0.60", {"start": v(-83.65, -32.22) * mm, "end": v(-83.65, -36.84) * mm});
            skLineSegment(sketch, "E18.4.0.61", {"start": v(-58.24, -44.92) * mm, "end": v(-58.24, -49.54) * mm});
            skLineSegment(sketch, "E18.4.0.62", {"start": v(-45.54, -49.54) * mm, "end": v(-40.92, -49.54) * mm});
            skLineSegment(sketch, "E18.4.0.63", {"start": v(-96.34, -49.54) * mm, "end": v(-91.72, -49.54) * mm});
            skLineSegment(sketch, "E18.4.0.64", {"start": v(60.67, -32.22) * mm, "end": v(60.67, -36.84) * mm});
            skLineSegment(sketch, "E18.4.0.65", {"start": v(111.47, -32.22) * mm, "end": v(111.47, -36.84) * mm});
            skLineSegment(sketch, "E18.4.0.66", {"start": v(-7.44, -49.54) * mm, "end": v(-2.82, -49.54) * mm});
            skLineSegment(sketch, "E18.4.0.67", {"start": v(17.96, -44.92) * mm, "end": v(22.58, -44.92) * mm});
            skLineSegment(sketch, "E18.4.0.68", {"start": v(81.46, -44.92) * mm, "end": v(86.08, -44.92) * mm});
            skLineSegment(sketch, "E18.4.0.69", {"start": v(-7.44, -44.92) * mm, "end": v(-7.44, -49.54) * mm});
            skLineSegment(sketch, "E18.4.0.70", {"start": v(73.38, -44.92) * mm, "end": v(73.38, -49.54) * mm});
            skLineSegment(sketch, "E18.4.0.71", {"start": v(-45.54, -44.92) * mm, "end": v(-40.92, -44.92) * mm});
            skLineSegment(sketch, "E18.4.0.72", {"start": v(-70.95, -32.22) * mm, "end": v(-70.95, -36.84) * mm});
            skLineSegment(sketch, "E18.4.0.73", {"start": v(-20.15, -32.22) * mm, "end": v(-20.15, -36.84) * mm});
            skLineSegment(sketch, "E18.4.0.74", {"start": v(30.65, -32.22) * mm, "end": v(30.65, -36.84) * mm});
            skLineSegment(sketch, "E18.4.0.75", {"start": v(81.45, -32.22) * mm, "end": v(81.45, -36.84) * mm});
            skLineSegment(sketch, "E18.4.0.76", {"start": v(-40.93, -32.22) * mm, "end": v(-40.93, -36.84) * mm});
            skLineSegment(sketch, "E18.4.0.77", {"start": v(9.87, -32.22) * mm, "end": v(9.87, -36.84) * mm});
            skLineSegment(sketch, "E18.4.0.78", {"start": v(-32.85, -32.22) * mm, "end": v(-32.85, -36.84) * mm});
            skLineSegment(sketch, "E18.4.0.79", {"start": v(30.66, -44.92) * mm, "end": v(35.28, -44.92) * mm});
            skLineSegment(sketch, "E18.4.0.80", {"start": v(106.86, -44.92) * mm, "end": v(111.48, -44.92) * mm});
            skLineSegment(sketch, "E18.4.0.81", {"start": v(-70.94, -44.92) * mm, "end": v(-70.94, -49.54) * mm});
            skLineSegment(sketch, "E18.4.0.82", {"start": v(5.26, -44.92) * mm, "end": v(9.88, -44.92) * mm});
            skLineSegment(sketch, "E18.4.0.83", {"start": v(-70.95, -36.84) * mm, "end": v(-66.33, -36.84) * mm});
            skLineSegment(sketch, "E18.4.0.84", {"start": v(-20.15, -36.84) * mm, "end": v(-15.53, -36.84) * mm});
            skLineSegment(sketch, "E18.4.0.85", {"start": v(30.65, -36.84) * mm, "end": v(35.27, -36.84) * mm});
            skLineSegment(sketch, "E18.4.0.86", {"start": v(81.45, -36.84) * mm, "end": v(86.07, -36.84) * mm});
            skLineSegment(sketch, "E18.4.0.87", {"start": v(17.95, -32.22) * mm, "end": v(17.95, -36.84) * mm});
            skLineSegment(sketch, "E18.4.0.88", {"start": v(-96.34, -44.92) * mm, "end": v(-96.34, -49.54) * mm});
            skLineSegment(sketch, "E18.4.0.89", {"start": v(-66.32, -44.92) * mm, "end": v(-66.32, -49.54) * mm});
            skLineSegment(sketch, "E18.4.0.90", {"start": v(-40.92, -44.92) * mm, "end": v(-40.92, -49.54) * mm});
            skLineSegment(sketch, "E18.4.0.91", {"start": v(86.08, -44.92) * mm, "end": v(86.08, -49.54) * mm});
            skLineSegment(sketch, "E18.4.0.92", {"start": v(-58.24, -44.92) * mm, "end": v(-53.62, -44.92) * mm});
            skLineSegment(sketch, "E18.4.0.93", {"start": v(106.86, -44.92) * mm, "end": v(106.86, -49.54) * mm});
            skLineSegment(sketch, "E18.4.0.94", {"start": v(-66.33, -32.22) * mm, "end": v(-66.33, -36.84) * mm});
            skLineSegment(sketch, "E18.4.0.95", {"start": v(106.85, -36.84) * mm, "end": v(111.47, -36.84) * mm});
            skLineSegment(sketch, "E18.4.0.96", {"start": v(-15.53, -32.22) * mm, "end": v(-15.53, -36.84) * mm});
            skLineSegment(sketch, "E18.4.0.97", {"start": v(-32.84, -44.92) * mm, "end": v(-28.22, -44.92) * mm});
            skLineSegment(sketch, "E18.4.0.98", {"start": v(35.27, -32.22) * mm, "end": v(35.27, -36.84) * mm});
            skLineSegment(sketch, "E18.4.0.99", {"start": v(86.07, -32.22) * mm, "end": v(86.07, -36.84) * mm});
            skLineSegment(sketch, "E18.4.0.100", {"start": v(68.76, -44.92) * mm, "end": v(68.76, -49.54) * mm});
            skLineSegment(sketch, "E18.4.0.101", {"start": v(30.66, -49.54) * mm, "end": v(35.28, -49.54) * mm});
            skLineSegment(sketch, "E18.4.0.102", {"start": v(68.75, -32.22) * mm, "end": v(68.75, -36.84) * mm});
            skLineSegment(sketch, "E18.4.0.103", {"start": v(-45.55, -36.84) * mm, "end": v(-40.93, -36.84) * mm});
            skLineSegment(sketch, "E18.4.0.104", {"start": v(5.25, -36.84) * mm, "end": v(9.87, -36.84) * mm});
            skLineSegment(sketch, "E18.4.0.105", {"start": v(56.05, -36.84) * mm, "end": v(60.67, -36.84) * mm});
            skLineSegment(sketch, "E18.4.0.106", {"start": v(-20.14, -44.92) * mm, "end": v(-15.52, -44.92) * mm});
            skLineSegment(sketch, "E18.4.0.107", {"start": v(68.76, -49.54) * mm, "end": v(73.38, -49.54) * mm});
            skLineSegment(sketch, "E18.4.0.108", {"start": v(56.06, -49.54) * mm, "end": v(60.68, -49.54) * mm});
            skLineSegment(sketch, "E18.4.0.109", {"start": v(111.48, -44.92) * mm, "end": v(111.48, -49.54) * mm});
            skLineSegment(sketch, "E18.4.0.110", {"start": v(56.05, -32.22) * mm, "end": v(60.67, -32.22) * mm});
            skLineSegment(sketch, "E18.4.0.111", {"start": v(106.85, -32.22) * mm, "end": v(111.47, -32.22) * mm});
            skLineSegment(sketch, "E18.4.0.112", {"start": v(-53.62, -44.92) * mm, "end": v(-53.62, -49.54) * mm});
            skLineSegment(sketch, "E18.4.0.113", {"start": v(-45.55, -32.22) * mm, "end": v(-40.93, -32.22) * mm});
            skLineSegment(sketch, "E18.4.0.114", {"start": v(5.25, -32.22) * mm, "end": v(9.87, -32.22) * mm});
            skLineSegment(sketch, "E18.4.0.115", {"start": v(-15.52, -44.92) * mm, "end": v(-15.52, -49.54) * mm});
            skLineSegment(sketch, "E18.4.0.116", {"start": v(43.36, -44.92) * mm, "end": v(43.36, -49.54) * mm});
            skLineSegment(sketch, "E18.4.0.117", {"start": v(-70.95, -32.22) * mm, "end": v(-66.33, -32.22) * mm});
            skLineSegment(sketch, "E18.4.0.118", {"start": v(-20.15, -32.22) * mm, "end": v(-15.53, -32.22) * mm});
            skLineSegment(sketch, "E18.4.0.119", {"start": v(30.65, -32.22) * mm, "end": v(35.27, -32.22) * mm});
            skLineSegment(sketch, "E18.4.0.120", {"start": v(81.45, -32.22) * mm, "end": v(86.07, -32.22) * mm});
            skLineSegment(sketch, "E18.4.0.121", {"start": v(81.46, -49.54) * mm, "end": v(86.08, -49.54) * mm});
            skLineSegment(sketch, "E18.4.0.122", {"start": v(5.26, -49.54) * mm, "end": v(9.88, -49.54) * mm});
            skLineSegment(sketch, "E18.4.0.123", {"start": v(60.68, -44.92) * mm, "end": v(60.68, -49.54) * mm});
            skLineSegment(sketch, "E18.4.0.124", {"start": v(43.35, -32.22) * mm, "end": v(43.35, -36.84) * mm});
            skLineSegment(sketch, "E18.4.0.125", {"start": v(94.15, -32.22) * mm, "end": v(94.15, -36.84) * mm});
            skLineSegment(sketch, "E18.4.0.126", {"start": v(-32.84, -49.54) * mm, "end": v(-28.22, -49.54) * mm});
            skLineSegment(sketch, "E18.4.0.127", {"start": v(-32.84, -44.92) * mm, "end": v(-32.84, -49.54) * mm});
            skLineSegment(sketch, "E18.4.0.128", {"start": v(-58.24, -49.54) * mm, "end": v(-53.62, -49.54) * mm});
            skLineSegment(sketch, "E18.4.0.129", {"start": v(-109.04, -57.6) * mm, "end": v(-104.42, -57.6) * mm});
            skLineSegment(sketch, "E18.4.0.130", {"start": v(106.86, -49.54) * mm, "end": v(111.48, -49.54) * mm});
            skLineSegment(sketch, "E18.4.0.133", {"start": v(22.57, -32.22) * mm, "end": v(22.57, -36.84) * mm});
            skLineSegment(sketch, "E18.4.0.134", {"start": v(-28.23, -32.22) * mm, "end": v(-28.23, -36.84) * mm});
            skLineSegment(sketch, "E18.4.0.135", {"start": v(-79.03, -32.22) * mm, "end": v(-79.03, -36.84) * mm});
            skLineSegment(sketch, "E18.4.0.136", {"start": v(-70.94, -44.92) * mm, "end": v(-66.32, -44.92) * mm});
            skLineSegment(sketch, "E18.4.0.137", {"start": v(68.75, -36.84) * mm, "end": v(73.37, -36.84) * mm});
            skLineSegment(sketch, "E18.4.0.138", {"start": v(17.95, -36.84) * mm, "end": v(22.57, -36.84) * mm});
            skLineSegment(sketch, "E18.4.0.139", {"start": v(-32.85, -36.84) * mm, "end": v(-28.23, -36.84) * mm});
            skLineSegment(sketch, "E18.4.0.140", {"start": v(-83.65, -36.84) * mm, "end": v(-79.03, -36.84) * mm});
            skLineSegment(sketch, "E18.4.0.141", {"start": v(-83.64, -49.54) * mm, "end": v(-79.02, -49.54) * mm});
            skLineSegment(sketch, "E18.4.0.142", {"start": v(-83.64, -44.92) * mm, "end": v(-83.64, -49.54) * mm});
            skLineSegment(sketch, "E18.4.0.143", {"start": v(17.96, -44.92) * mm, "end": v(17.96, -49.54) * mm});
            skLineSegment(sketch, "E18.4.0.144", {"start": v(-91.73, -32.22) * mm, "end": v(-91.73, -36.84) * mm});
            skLineSegment(sketch, "E18.4.0.145", {"start": v(-96.35, -36.84) * mm, "end": v(-91.73, -36.84) * mm});
            skLineSegment(sketch, "E18.4.0.147", {"start": v(-91.72, -44.92) * mm, "end": v(-91.72, -49.54) * mm});
            skLineSegment(sketch, "E18.4.0.148", {"start": v(-96.35, -32.22) * mm, "end": v(-96.35, -36.84) * mm});
            skLineSegment(sketch, "E18.4.0.149", {"start": v(-96.34, -44.92) * mm, "end": v(-91.72, -44.92) * mm});
            skLineSegment(sketch, "E18.4.0.150", {"start": v(-96.35, -32.22) * mm, "end": v(-91.73, -32.22) * mm});
            skLineSegment(sketch, "E18.4.0.151", {"start": v(-109.04, -44.92) * mm, "end": v(-104.42, -44.92) * mm});
            skLineSegment(sketch, "E18.4.0.153", {"start": v(-109.04, -44.92) * mm, "end": v(-109.04, -49.54) * mm});
            skLineSegment(sketch, "E18.4.0.154", {"start": v(-109.05, -44.92) * mm, "end": v(-104.43, -44.92) * mm});
            skLineSegment(sketch, "E18.4.0.155", {"start": v(-104.43, -32.22) * mm, "end": v(-104.43, -36.84) * mm});
            skLineSegment(sketch, "E18.4.0.156", {"start": v(-109.05, -32.22) * mm, "end": v(-109.05, -36.84) * mm});
            skLineSegment(sketch, "E18.4.0.157", {"start": v(-109.05, -32.22) * mm, "end": v(-104.43, -32.22) * mm});
            skLineSegment(sketch, "E18.4.0.158", {"start": v(-109.05, -36.84) * mm, "end": v(-104.43, -36.84) * mm});
            skLineSegment(sketch, "E18.4.0.159", {"start": v(-109.04, -49.54) * mm, "end": v(-104.42, -49.54) * mm});
            skLineSegment(sketch, "E18.4.0.160", {"start": v(-104.43, -44.92) * mm, "end": v(-104.43, -49.54) * mm});
            skLineSegment(sketch, "E18.4.0.161", {"start": v(-109.05, -44.92) * mm, "end": v(-109.05, -49.54) * mm});
            skLineSegment(sketch, "E18.4.0.162", {"start": v(-109.05, -49.54) * mm, "end": v(-104.43, -49.54) * mm});
            skLineSegment(sketch, "E18.4.0.163", {"start": v(-104.42, -44.92) * mm, "end": v(-104.42, -49.54) * mm});
            skPoint(sketch, "E18.5.0.0", {"position": v(-106.72, -59.93) * mm});
            skPoint(sketch, "E18.5.0.1", {"position": v(-106.71, -72.63) * mm});
            skPoint(sketch, "E18.5.0.2", {"position": v(-94.01, -72.63) * mm});
            skPoint(sketch, "E18.5.0.3", {"position": v(-94.02, -59.93) * mm});
            skPoint(sketch, "E18.5.0.6", {"position": v(-106.72, -72.63) * mm});
            skLineSegment(sketch, "E18.5.0.7", {"start": v(-114.8, -51.85) * mm, "end": v(-114.8, -55.9) * mm});
            skLineSegment(sketch, "E18.5.0.8", {"start": v(68.78, -70.32) * mm, "end": v(73.4, -70.32) * mm});
            skLineSegment(sketch, "E18.5.0.9", {"start": v(-2.8, -70.32) * mm, "end": v(-2.8, -74.94) * mm});
            skLineSegment(sketch, "E18.5.0.14", {"start": v(-58.23, -57.62) * mm, "end": v(-58.23, -62.24) * mm});
            skLineSegment(sketch, "E18.5.0.15", {"start": v(-7.43, -57.62) * mm, "end": v(-7.43, -62.24) * mm});
            skLineSegment(sketch, "E18.5.0.16", {"start": v(48, -70.32) * mm, "end": v(48, -74.94) * mm});
            skLineSegment(sketch, "E18.5.0.17", {"start": v(9.9, -70.32) * mm, "end": v(9.9, -74.94) * mm});
            skLineSegment(sketch, "E18.5.0.18", {"start": v(-7.42, -70.32) * mm, "end": v(-2.8, -70.32) * mm});
            skLineSegment(sketch, "E18.5.0.19", {"start": v(-20.12, -70.32) * mm, "end": v(-20.12, -74.94) * mm});
            skLineSegment(sketch, "E18.5.0.20", {"start": v(-20.12, -74.94) * mm, "end": v(-15.5, -74.94) * mm});
            skLineSegment(sketch, "E18.5.0.21", {"start": v(-83.63, -57.62) * mm, "end": v(-79, -57.62) * mm});
            skLineSegment(sketch, "E18.5.0.22", {"start": v(-32.83, -57.62) * mm, "end": v(-28.2, -57.62) * mm});
            skLineSegment(sketch, "E18.5.0.23", {"start": v(17.97, -57.62) * mm, "end": v(22.6, -57.62) * mm});
            skLineSegment(sketch, "E18.5.0.24", {"start": v(68.77, -57.62) * mm, "end": v(73.4, -57.62) * mm});
            skLineSegment(sketch, "E18.5.0.25", {"start": v(35.3, -70.32) * mm, "end": v(35.3, -74.94) * mm});
            skLineSegment(sketch, "E18.5.0.26", {"start": v(56.08, -70.32) * mm, "end": v(60.7, -70.32) * mm});
            skLineSegment(sketch, "E18.5.0.27", {"start": v(56.08, -70.32) * mm, "end": v(56.08, -74.94) * mm});
            skLineSegment(sketch, "E18.5.0.28", {"start": v(43.37, -62.24) * mm, "end": v(48, -62.24) * mm});
            skLineSegment(sketch, "E18.5.0.29", {"start": v(94.17, -62.24) * mm, "end": v(98.8, -62.24) * mm});
            skLineSegment(sketch, "E18.5.0.30", {"start": v(-28.2, -70.32) * mm, "end": v(-28.2, -74.94) * mm});
            skLineSegment(sketch, "E18.5.0.31", {"start": v(-58.23, -62.24) * mm, "end": v(-53.6, -62.24) * mm});
            skLineSegment(sketch, "E18.5.0.32", {"start": v(-7.43, -62.24) * mm, "end": v(-2.8, -62.24) * mm});
            skLineSegment(sketch, "E18.5.0.33", {"start": v(81.48, -70.32) * mm, "end": v(81.48, -74.94) * mm});
            skLineSegment(sketch, "E18.5.0.34", {"start": v(43.38, -70.32) * mm, "end": v(48, -70.32) * mm});
            skLineSegment(sketch, "E18.5.0.35", {"start": v(43.38, -74.94) * mm, "end": v(48, -74.94) * mm});
            skLineSegment(sketch, "E18.5.0.36", {"start": v(5.28, -70.32) * mm, "end": v(5.28, -74.94) * mm});
            skLineSegment(sketch, "E18.5.0.37", {"start": v(94.18, -70.32) * mm, "end": v(94.18, -74.94) * mm});
            skLineSegment(sketch, "E18.5.0.38", {"start": v(48, -57.62) * mm, "end": v(48, -62.24) * mm});
            skLineSegment(sketch, "E18.5.0.39", {"start": v(98.8, -57.62) * mm, "end": v(98.8, -62.24) * mm});
            skLineSegment(sketch, "E18.5.0.40", {"start": v(30.68, -70.32) * mm, "end": v(30.68, -74.94) * mm});
            skLineSegment(sketch, "E18.5.0.41", {"start": v(-70.92, -74.94) * mm, "end": v(-66.3, -74.94) * mm});
            skLineSegment(sketch, "E18.5.0.42", {"start": v(98.8, -70.32) * mm, "end": v(98.8, -74.94) * mm});
            skLineSegment(sketch, "E18.5.0.43", {"start": v(-53.6, -57.62) * mm, "end": v(-53.6, -62.24) * mm});
            skLineSegment(sketch, "E18.5.0.44", {"start": v(-2.8, -57.62) * mm, "end": v(-2.8, -62.24) * mm});
            skLineSegment(sketch, "E18.5.0.45", {"start": v(106.87, -57.62) * mm, "end": v(106.87, -62.24) * mm});
            skLineSegment(sketch, "E18.5.0.46", {"start": v(94.18, -74.94) * mm, "end": v(98.8, -74.94) * mm});
            skLineSegment(sketch, "E18.5.0.47", {"start": v(94.18, -70.32) * mm, "end": v(98.8, -70.32) * mm});
            skLineSegment(sketch, "E18.5.0.48", {"start": v(-83.62, -70.32) * mm, "end": v(-79, -70.32) * mm});
            skLineSegment(sketch, "E18.5.0.49", {"start": v(-45.52, -70.32) * mm, "end": v(-45.52, -74.94) * mm});
            skLineSegment(sketch, "E18.5.0.50", {"start": v(-79, -70.32) * mm, "end": v(-79, -74.94) * mm});
            skLineSegment(sketch, "E18.5.0.51", {"start": v(17.98, -74.94) * mm, "end": v(22.6, -74.94) * mm});
            skLineSegment(sketch, "E18.5.0.52", {"start": v(-45.53, -57.62) * mm, "end": v(-45.53, -62.24) * mm});
            skLineSegment(sketch, "E18.5.0.53", {"start": v(5.27, -57.62) * mm, "end": v(5.27, -62.24) * mm});
            skLineSegment(sketch, "E18.5.0.54", {"start": v(43.37, -57.62) * mm, "end": v(48, -57.62) * mm});
            skLineSegment(sketch, "E18.5.0.55", {"start": v(94.17, -57.62) * mm, "end": v(98.8, -57.62) * mm});
            skLineSegment(sketch, "E18.5.0.56", {"start": v(56.07, -57.62) * mm, "end": v(56.07, -62.24) * mm});
            skLineSegment(sketch, "E18.5.0.57", {"start": v(22.6, -70.32) * mm, "end": v(22.6, -74.94) * mm});
            skLineSegment(sketch, "E18.5.0.58", {"start": v(-58.23, -57.62) * mm, "end": v(-53.6, -57.62) * mm});
            skLineSegment(sketch, "E18.5.0.59", {"start": v(-7.43, -57.62) * mm, "end": v(-2.8, -57.62) * mm});
            skLineSegment(sketch, "E18.5.0.60", {"start": v(-83.63, -57.62) * mm, "end": v(-83.63, -62.24) * mm});
            skLineSegment(sketch, "E18.5.0.61", {"start": v(-58.22, -70.32) * mm, "end": v(-58.22, -74.94) * mm});
            skLineSegment(sketch, "E18.5.0.62", {"start": v(-45.52, -74.94) * mm, "end": v(-40.9, -74.94) * mm});
            skLineSegment(sketch, "E18.5.0.63", {"start": v(-96.32, -74.94) * mm, "end": v(-91.7, -74.94) * mm});
            skLineSegment(sketch, "E18.5.0.64", {"start": v(60.7, -57.62) * mm, "end": v(60.7, -62.24) * mm});
            skLineSegment(sketch, "E18.5.0.65", {"start": v(111.5, -57.62) * mm, "end": v(111.5, -62.24) * mm});
            skLineSegment(sketch, "E18.5.0.66", {"start": v(-7.42, -74.94) * mm, "end": v(-2.8, -74.94) * mm});
            skLineSegment(sketch, "E18.5.0.67", {"start": v(17.98, -70.32) * mm, "end": v(22.6, -70.32) * mm});
            skLineSegment(sketch, "E18.5.0.68", {"start": v(81.48, -70.32) * mm, "end": v(86.1, -70.32) * mm});
            skLineSegment(sketch, "E18.5.0.69", {"start": v(-7.42, -70.32) * mm, "end": v(-7.42, -74.94) * mm});
            skLineSegment(sketch, "E18.5.0.70", {"start": v(73.4, -70.32) * mm, "end": v(73.4, -74.94) * mm});
            skLineSegment(sketch, "E18.5.0.71", {"start": v(-45.52, -70.32) * mm, "end": v(-40.9, -70.32) * mm});
            skLineSegment(sketch, "E18.5.0.72", {"start": v(-70.93, -57.62) * mm, "end": v(-70.93, -62.24) * mm});
            skLineSegment(sketch, "E18.5.0.73", {"start": v(-20.13, -57.62) * mm, "end": v(-20.13, -62.24) * mm});
            skLineSegment(sketch, "E18.5.0.74", {"start": v(30.67, -57.62) * mm, "end": v(30.67, -62.24) * mm});
            skLineSegment(sketch, "E18.5.0.75", {"start": v(81.47, -57.62) * mm, "end": v(81.47, -62.24) * mm});
            skLineSegment(sketch, "E18.5.0.76", {"start": v(-40.9, -57.62) * mm, "end": v(-40.9, -62.24) * mm});
            skLineSegment(sketch, "E18.5.0.77", {"start": v(9.9, -57.62) * mm, "end": v(9.9, -62.24) * mm});
            skLineSegment(sketch, "E18.5.0.78", {"start": v(-32.83, -57.62) * mm, "end": v(-32.83, -62.24) * mm});
            skLineSegment(sketch, "E18.5.0.79", {"start": v(30.68, -70.32) * mm, "end": v(35.3, -70.32) * mm});
            skLineSegment(sketch, "E18.5.0.80", {"start": v(106.88, -70.32) * mm, "end": v(111.5, -70.32) * mm});
            skLineSegment(sketch, "E18.5.0.81", {"start": v(-70.92, -70.32) * mm, "end": v(-70.92, -74.94) * mm});
            skLineSegment(sketch, "E18.5.0.82", {"start": v(5.28, -70.32) * mm, "end": v(9.9, -70.32) * mm});
            skLineSegment(sketch, "E18.5.0.83", {"start": v(-70.93, -62.24) * mm, "end": v(-66.3, -62.24) * mm});
            skLineSegment(sketch, "E18.5.0.84", {"start": v(-20.13, -62.24) * mm, "end": v(-15.5, -62.24) * mm});
            skLineSegment(sketch, "E18.5.0.85", {"start": v(30.67, -62.24) * mm, "end": v(35.3, -62.24) * mm});
            skLineSegment(sketch, "E18.5.0.86", {"start": v(81.47, -62.24) * mm, "end": v(86.1, -62.24) * mm});
            skLineSegment(sketch, "E18.5.0.87", {"start": v(17.97, -57.62) * mm, "end": v(17.97, -62.24) * mm});
            skLineSegment(sketch, "E18.5.0.88", {"start": v(-96.32, -70.32) * mm, "end": v(-96.32, -74.94) * mm});
            skLineSegment(sketch, "E18.5.0.89", {"start": v(-66.3, -70.32) * mm, "end": v(-66.3, -74.94) * mm});
            skLineSegment(sketch, "E18.5.0.90", {"start": v(-40.9, -70.32) * mm, "end": v(-40.9, -74.94) * mm});
            skLineSegment(sketch, "E18.5.0.91", {"start": v(86.1, -70.32) * mm, "end": v(86.1, -74.94) * mm});
            skLineSegment(sketch, "E18.5.0.92", {"start": v(-58.22, -70.32) * mm, "end": v(-53.6, -70.32) * mm});
            skLineSegment(sketch, "E18.5.0.93", {"start": v(106.88, -70.32) * mm, "end": v(106.88, -74.94) * mm});
            skLineSegment(sketch, "E18.5.0.94", {"start": v(-66.3, -57.62) * mm, "end": v(-66.3, -62.24) * mm});
            skLineSegment(sketch, "E18.5.0.95", {"start": v(106.87, -62.24) * mm, "end": v(111.5, -62.24) * mm});
            skLineSegment(sketch, "E18.5.0.96", {"start": v(-15.5, -57.62) * mm, "end": v(-15.5, -62.24) * mm});
            skLineSegment(sketch, "E18.5.0.97", {"start": v(-32.82, -70.32) * mm, "end": v(-28.2, -70.32) * mm});
            skLineSegment(sketch, "E18.5.0.98", {"start": v(35.3, -57.62) * mm, "end": v(35.3, -62.24) * mm});
            skLineSegment(sketch, "E18.5.0.99", {"start": v(86.1, -57.62) * mm, "end": v(86.1, -62.24) * mm});
            skLineSegment(sketch, "E18.5.0.100", {"start": v(68.78, -70.32) * mm, "end": v(68.78, -74.94) * mm});
            skLineSegment(sketch, "E18.5.0.101", {"start": v(30.68, -74.94) * mm, "end": v(35.3, -74.94) * mm});
            skLineSegment(sketch, "E18.5.0.102", {"start": v(68.77, -57.62) * mm, "end": v(68.77, -62.24) * mm});
            skLineSegment(sketch, "E18.5.0.103", {"start": v(-45.53, -62.24) * mm, "end": v(-40.9, -62.24) * mm});
            skLineSegment(sketch, "E18.5.0.104", {"start": v(5.27, -62.24) * mm, "end": v(9.9, -62.24) * mm});
            skLineSegment(sketch, "E18.5.0.105", {"start": v(56.07, -62.24) * mm, "end": v(60.7, -62.24) * mm});
            skLineSegment(sketch, "E18.5.0.106", {"start": v(-20.12, -70.32) * mm, "end": v(-15.5, -70.32) * mm});
            skLineSegment(sketch, "E18.5.0.107", {"start": v(68.78, -74.94) * mm, "end": v(73.4, -74.94) * mm});
            skLineSegment(sketch, "E18.5.0.108", {"start": v(56.08, -74.94) * mm, "end": v(60.7, -74.94) * mm});
            skLineSegment(sketch, "E18.5.0.109", {"start": v(111.5, -70.32) * mm, "end": v(111.5, -74.94) * mm});
            skLineSegment(sketch, "E18.5.0.110", {"start": v(56.07, -57.62) * mm, "end": v(60.7, -57.62) * mm});
            skLineSegment(sketch, "E18.5.0.111", {"start": v(106.87, -57.62) * mm, "end": v(111.5, -57.62) * mm});
            skLineSegment(sketch, "E18.5.0.112", {"start": v(-53.6, -70.32) * mm, "end": v(-53.6, -74.94) * mm});
            skLineSegment(sketch, "E18.5.0.113", {"start": v(-45.53, -57.62) * mm, "end": v(-40.9, -57.62) * mm});
            skLineSegment(sketch, "E18.5.0.114", {"start": v(5.27, -57.62) * mm, "end": v(9.9, -57.62) * mm});
            skLineSegment(sketch, "E18.5.0.115", {"start": v(-15.5, -70.32) * mm, "end": v(-15.5, -74.94) * mm});
            skLineSegment(sketch, "E18.5.0.116", {"start": v(43.38, -70.32) * mm, "end": v(43.38, -74.94) * mm});
            skLineSegment(sketch, "E18.5.0.117", {"start": v(-70.93, -57.62) * mm, "end": v(-66.3, -57.62) * mm});
            skLineSegment(sketch, "E18.5.0.118", {"start": v(-20.13, -57.62) * mm, "end": v(-15.5, -57.62) * mm});
            skLineSegment(sketch, "E18.5.0.119", {"start": v(30.67, -57.62) * mm, "end": v(35.3, -57.62) * mm});
            skLineSegment(sketch, "E18.5.0.120", {"start": v(81.47, -57.62) * mm, "end": v(86.1, -57.62) * mm});
            skLineSegment(sketch, "E18.5.0.121", {"start": v(81.48, -74.94) * mm, "end": v(86.1, -74.94) * mm});
            skLineSegment(sketch, "E18.5.0.122", {"start": v(5.28, -74.94) * mm, "end": v(9.9, -74.94) * mm});
            skLineSegment(sketch, "E18.5.0.123", {"start": v(60.7, -70.32) * mm, "end": v(60.7, -74.94) * mm});
            skLineSegment(sketch, "E18.5.0.124", {"start": v(43.37, -57.62) * mm, "end": v(43.37, -62.24) * mm});
            skLineSegment(sketch, "E18.5.0.125", {"start": v(94.17, -57.62) * mm, "end": v(94.17, -62.24) * mm});
            skLineSegment(sketch, "E18.5.0.126", {"start": v(-32.82, -74.94) * mm, "end": v(-28.2, -74.94) * mm});
            skLineSegment(sketch, "E18.5.0.127", {"start": v(-32.82, -70.32) * mm, "end": v(-32.82, -74.94) * mm});
            skLineSegment(sketch, "E18.5.0.128", {"start": v(-58.22, -74.94) * mm, "end": v(-53.6, -74.94) * mm});
            skLineSegment(sketch, "E18.5.0.130", {"start": v(106.88, -74.94) * mm, "end": v(111.5, -74.94) * mm});
            skLineSegment(sketch, "E18.5.0.132", {"start": v(73.4, -57.62) * mm, "end": v(73.4, -62.24) * mm});
            skLineSegment(sketch, "E18.5.0.133", {"start": v(22.6, -57.62) * mm, "end": v(22.6, -62.24) * mm});
            skLineSegment(sketch, "E18.5.0.134", {"start": v(-28.2, -57.62) * mm, "end": v(-28.2, -62.24) * mm});
            skLineSegment(sketch, "E18.5.0.135", {"start": v(-79, -57.62) * mm, "end": v(-79, -62.24) * mm});
            skLineSegment(sketch, "E18.5.0.136", {"start": v(-70.92, -70.32) * mm, "end": v(-66.3, -70.32) * mm});
            skLineSegment(sketch, "E18.5.0.137", {"start": v(68.77, -62.24) * mm, "end": v(73.4, -62.24) * mm});
            skLineSegment(sketch, "E18.5.0.138", {"start": v(17.97, -62.24) * mm, "end": v(22.6, -62.24) * mm});
            skLineSegment(sketch, "E18.5.0.139", {"start": v(-32.83, -62.24) * mm, "end": v(-28.2, -62.24) * mm});
            skLineSegment(sketch, "E18.5.0.140", {"start": v(-83.63, -62.24) * mm, "end": v(-79, -62.24) * mm});
            skLineSegment(sketch, "E18.5.0.141", {"start": v(-83.62, -74.94) * mm, "end": v(-79, -74.94) * mm});
            skLineSegment(sketch, "E18.5.0.142", {"start": v(-83.62, -70.32) * mm, "end": v(-83.62, -74.94) * mm});
            skLineSegment(sketch, "E18.5.0.143", {"start": v(17.98, -70.32) * mm, "end": v(17.98, -74.94) * mm});
            skLineSegment(sketch, "E18.5.0.144", {"start": v(-91.7, -57.62) * mm, "end": v(-91.7, -62.24) * mm});
            skLineSegment(sketch, "E18.5.0.145", {"start": v(-96.33, -62.24) * mm, "end": v(-91.7, -62.24) * mm});
            skLineSegment(sketch, "E18.5.0.149", {"start": v(-96.32, -70.32) * mm, "end": v(-91.7, -70.32) * mm});
            skLineSegment(sketch, "E18.5.0.150", {"start": v(-96.33, -57.62) * mm, "end": v(-91.7, -57.62) * mm});
            skLineSegment(sketch, "E18.5.0.151", {"start": v(-109.02, -70.32) * mm, "end": v(-104.4, -70.32) * mm});
            skLineSegment(sketch, "E18.5.0.153", {"start": v(-109.02, -70.32) * mm, "end": v(-109.02, -74.94) * mm});
            skLineSegment(sketch, "E18.5.0.154", {"start": v(-109.03, -70.32) * mm, "end": v(-104.4, -70.32) * mm});
            skLineSegment(sketch, "E18.5.0.155", {"start": v(-104.4, -57.62) * mm, "end": v(-104.4, -62.24) * mm});
            skLineSegment(sketch, "E18.5.0.156", {"start": v(-109.03, -57.62) * mm, "end": v(-109.03, -62.24) * mm});
            skLineSegment(sketch, "E18.5.0.157", {"start": v(-109.03, -57.62) * mm, "end": v(-104.4, -57.62) * mm});
            skLineSegment(sketch, "E18.5.0.158", {"start": v(-109.03, -62.24) * mm, "end": v(-104.4, -62.24) * mm});
            skLineSegment(sketch, "E18.5.0.159", {"start": v(-109.02, -74.94) * mm, "end": v(-104.4, -74.94) * mm});
            skLineSegment(sketch, "E18.5.0.160", {"start": v(-104.4, -70.32) * mm, "end": v(-104.4, -74.94) * mm});
            skLineSegment(sketch, "E18.5.0.161", {"start": v(-109.03, -70.32) * mm, "end": v(-109.03, -74.94) * mm});
            skLineSegment(sketch, "E18.5.0.162", {"start": v(-109.03, -74.94) * mm, "end": v(-104.4, -74.94) * mm});
            skLineSegment(sketch, "E18.5.0.163", {"start": v(-104.4, -70.32) * mm, "end": v(-104.4, -74.94) * mm});
            skLineSegment(sketch, "E19", {"start": v(-91.7, -70.32) * mm, "end": v(-91.7, -74.94) * mm});
            skLineSegment(sketch, "E20", {"start": v(73.37, -32.22) * mm, "end": v(73.37, -36.84) * mm});
            skLineSegment(sketch, "E21", {"start": v(-96.33, -62.24) * mm, "end": v(-96.33, -57.62) * mm});
            skSolve(sketch);
        }
        {
            var Q0;
            Q0=qCreatedBy(makeId("Front.planeOp"),FACE);
            var sketch = newSketch(context, id + "F1", { "sketchPlane" : qUnion([Q0])});
            skLineSegment(sketch, "E22", {"start": v(295.02, 204.4) * mm, "end": v(409.32, 204.4) * mm});
            skLineSegment(sketch, "E23", {"start": v(295.02, 52) * mm, "end": v(409.32, 52) * mm});
            skLineSegment(sketch, "E24", {"start": v(295.02, 52) * mm, "end": v(282.32, 52) * mm});
            skLineSegment(sketch, "E25", {"start": v(409.32, 204.4) * mm, "end": v(409.32, 52) * mm});
            skLineSegment(sketch, "E26", {"start": v(409.32, 204.4) * mm, "end": v(405.28, 204.4) * mm});
            skLineSegment(sketch, "E27", {"start": v(282.32, 204.4) * mm, "end": v(409.32, 204.4) * mm});
            skLineSegment(sketch, "E28.4.0.0", {"start": v(288.09, 198.64) * mm, "end": v(292.7, 198.64) * mm});
            skLineSegment(sketch, "E28.4.0.1", {"start": v(292.7, 198.64) * mm, "end": v(292.7, 194.02) * mm});
            skLineSegment(sketch, "E28.4.0.2", {"start": v(288.09, 194.02) * mm, "end": v(292.7, 194.02) * mm});
            skLineSegment(sketch, "E28.4.0.3", {"start": v(288.09, 198.64) * mm, "end": v(288.09, 194.02) * mm});
            skLineSegment(sketch, "E28.4.0.4", {"start": v(300.79, 198.64) * mm, "end": v(305.4, 198.64) * mm});
            skLineSegment(sketch, "E28.4.0.5", {"start": v(305.4, 198.64) * mm, "end": v(305.4, 194.02) * mm});
            skLineSegment(sketch, "E28.4.0.6", {"start": v(300.79, 194.02) * mm, "end": v(305.4, 194.02) * mm});
            skLineSegment(sketch, "E28.4.0.7", {"start": v(300.79, 198.64) * mm, "end": v(300.79, 194.02) * mm});
            skLineSegment(sketch, "E28.5.0.0", {"start": v(313.49, 198.64) * mm, "end": v(318.1, 198.64) * mm});
            skLineSegment(sketch, "E28.5.0.1", {"start": v(318.1, 198.64) * mm, "end": v(318.1, 194.02) * mm});
            skLineSegment(sketch, "E28.5.0.2", {"start": v(313.49, 194.02) * mm, "end": v(318.1, 194.02) * mm});
            skLineSegment(sketch, "E28.5.0.3", {"start": v(313.49, 198.64) * mm, "end": v(313.49, 194.02) * mm});
            skLineSegment(sketch, "E28.5.0.4", {"start": v(326.19, 198.64) * mm, "end": v(330.8, 198.64) * mm});
            skLineSegment(sketch, "E28.5.0.5", {"start": v(330.8, 198.64) * mm, "end": v(330.8, 194.02) * mm});
            skLineSegment(sketch, "E28.5.0.6", {"start": v(326.19, 194.02) * mm, "end": v(330.8, 194.02) * mm});
            skLineSegment(sketch, "E28.5.0.7", {"start": v(326.19, 198.64) * mm, "end": v(326.19, 194.02) * mm});
            skLineSegment(sketch, "E28.6.0.0", {"start": v(338.89, 198.64) * mm, "end": v(343.5, 198.64) * mm});
            skLineSegment(sketch, "E28.6.0.1", {"start": v(343.5, 198.64) * mm, "end": v(343.5, 194.02) * mm});
            skLineSegment(sketch, "E28.6.0.2", {"start": v(338.89, 194.02) * mm, "end": v(343.5, 194.02) * mm});
            skLineSegment(sketch, "E28.6.0.3", {"start": v(338.89, 198.64) * mm, "end": v(338.89, 194.02) * mm});
            skLineSegment(sketch, "E28.6.0.4", {"start": v(351.59, 198.64) * mm, "end": v(356.2, 198.64) * mm});
            skLineSegment(sketch, "E28.6.0.5", {"start": v(356.2, 198.64) * mm, "end": v(356.2, 194.02) * mm});
            skLineSegment(sketch, "E28.6.0.6", {"start": v(351.59, 194.02) * mm, "end": v(356.2, 194.02) * mm});
            skLineSegment(sketch, "E28.6.0.7", {"start": v(351.59, 198.64) * mm, "end": v(351.59, 194.02) * mm});
            skLineSegment(sketch, "E28.7.0.0", {"start": v(364.29, 198.64) * mm, "end": v(368.9, 198.64) * mm});
            skLineSegment(sketch, "E28.7.0.1", {"start": v(368.9, 198.64) * mm, "end": v(368.9, 194.02) * mm});
            skLineSegment(sketch, "E28.7.0.2", {"start": v(364.29, 194.02) * mm, "end": v(368.9, 194.02) * mm});
            skLineSegment(sketch, "E28.7.0.3", {"start": v(364.29, 198.64) * mm, "end": v(364.29, 194.02) * mm});
            skLineSegment(sketch, "E28.7.0.4", {"start": v(376.99, 198.64) * mm, "end": v(381.6, 198.64) * mm});
            skLineSegment(sketch, "E28.7.0.5", {"start": v(381.6, 198.64) * mm, "end": v(381.6, 194.02) * mm});
            skLineSegment(sketch, "E28.7.0.6", {"start": v(376.99, 194.02) * mm, "end": v(381.6, 194.02) * mm});
            skLineSegment(sketch, "E28.7.0.7", {"start": v(376.99, 198.64) * mm, "end": v(376.99, 194.02) * mm});
            skLineSegment(sketch, "E28.8.0.0", {"start": v(389.69, 198.64) * mm, "end": v(394.3, 198.64) * mm});
            skLineSegment(sketch, "E28.8.0.1", {"start": v(394.3, 198.64) * mm, "end": v(394.3, 194.02) * mm});
            skLineSegment(sketch, "E28.8.0.2", {"start": v(389.69, 194.02) * mm, "end": v(394.3, 194.02) * mm});
            skLineSegment(sketch, "E28.8.0.3", {"start": v(389.69, 198.64) * mm, "end": v(389.69, 194.02) * mm});
            skLineSegment(sketch, "E28.8.0.4", {"start": v(402.39, 198.64) * mm, "end": v(407, 198.64) * mm});
            skLineSegment(sketch, "E28.8.0.5", {"start": v(407, 198.64) * mm, "end": v(407, 194.02) * mm});
            skLineSegment(sketch, "E28.8.0.6", {"start": v(402.39, 194.02) * mm, "end": v(407, 194.02) * mm});
            skLineSegment(sketch, "E28.8.0.7", {"start": v(402.39, 198.64) * mm, "end": v(402.39, 194.02) * mm});
            skLineSegment(sketch, "E29.0.1.4", {"start": v(364.3, 185.94) * mm, "end": v(368.92, 185.94) * mm});
            skLineSegment(sketch, "E29.0.1.6", {"start": v(313.5, 185.94) * mm, "end": v(318.12, 185.94) * mm});
            skLineSegment(sketch, "E29.0.1.9", {"start": v(288.1, 185.94) * mm, "end": v(292.72, 185.94) * mm});
            skLineSegment(sketch, "E29.0.1.11", {"start": v(313.5, 185.94) * mm, "end": v(313.5, 181.32) * mm});
            skLineSegment(sketch, "E29.0.1.12", {"start": v(330.82, 185.94) * mm, "end": v(330.82, 181.32) * mm});
            skLineSegment(sketch, "E29.0.1.15", {"start": v(402.4, 185.94) * mm, "end": v(407.02, 185.94) * mm});
            skLineSegment(sketch, "E29.0.1.16", {"start": v(368.92, 185.94) * mm, "end": v(368.92, 181.32) * mm});
            skLineSegment(sketch, "E29.0.1.17", {"start": v(318.12, 185.94) * mm, "end": v(318.12, 181.32) * mm});
            skLineSegment(sketch, "E29.0.1.18", {"start": v(326.2, 185.94) * mm, "end": v(326.2, 181.32) * mm});
            skLineSegment(sketch, "E29.0.1.20", {"start": v(292.72, 185.94) * mm, "end": v(292.72, 181.32) * mm});
            skLineSegment(sketch, "E29.0.1.22", {"start": v(288.1, 181.32) * mm, "end": v(292.72, 181.32) * mm});
            skLineSegment(sketch, "E29.0.1.23", {"start": v(364.3, 185.94) * mm, "end": v(364.3, 181.32) * mm});
            skLineSegment(sketch, "E29.0.1.28", {"start": v(377, 185.94) * mm, "end": v(377, 181.32) * mm});
            skLineSegment(sketch, "E29.0.1.30", {"start": v(381.62, 185.94) * mm, "end": v(381.62, 181.32) * mm});
            skLineSegment(sketch, "E29.0.1.32", {"start": v(288.1, 185.94) * mm, "end": v(288.1, 181.32) * mm});
            skLineSegment(sketch, "E29.0.1.33", {"start": v(389.7, 181.32) * mm, "end": v(394.32, 181.32) * mm});
            skLineSegment(sketch, "E29.0.1.34", {"start": v(338.9, 181.32) * mm, "end": v(343.52, 181.32) * mm});
            skLineSegment(sketch, "E29.0.1.36", {"start": v(377, 181.32) * mm, "end": v(381.62, 181.32) * mm});
            skLineSegment(sketch, "E29.0.1.37", {"start": v(364.3, 181.32) * mm, "end": v(368.92, 181.32) * mm});
            skLineSegment(sketch, "E29.0.1.39", {"start": v(326.2, 181.32) * mm, "end": v(330.82, 181.32) * mm});
            skLineSegment(sketch, "E29.0.1.40", {"start": v(313.5, 181.32) * mm, "end": v(318.12, 181.32) * mm});
            skLineSegment(sketch, "E29.0.1.44", {"start": v(389.7, 185.94) * mm, "end": v(389.7, 181.32) * mm});
            skLineSegment(sketch, "E29.0.1.45", {"start": v(338.9, 185.94) * mm, "end": v(338.9, 181.32) * mm});
            skLineSegment(sketch, "E29.0.1.47", {"start": v(300.8, 185.94) * mm, "end": v(305.42, 185.94) * mm});
            skLineSegment(sketch, "E29.0.1.49", {"start": v(389.7, 185.94) * mm, "end": v(394.32, 185.94) * mm});
            skLineSegment(sketch, "E29.0.1.50", {"start": v(338.9, 185.94) * mm, "end": v(343.52, 185.94) * mm});
            skLineSegment(sketch, "E29.0.1.51", {"start": v(351.6, 185.94) * mm, "end": v(356.22, 185.94) * mm});
            skLineSegment(sketch, "E29.0.1.52", {"start": v(300.8, 181.32) * mm, "end": v(305.42, 181.32) * mm});
            skLineSegment(sketch, "E29.0.1.53", {"start": v(351.6, 181.32) * mm, "end": v(356.22, 181.32) * mm});
            skLineSegment(sketch, "E29.0.1.56", {"start": v(394.32, 185.94) * mm, "end": v(394.32, 181.32) * mm});
            skLineSegment(sketch, "E29.0.1.57", {"start": v(343.52, 185.94) * mm, "end": v(343.52, 181.32) * mm});
            skLineSegment(sketch, "E29.0.1.58", {"start": v(402.4, 181.32) * mm, "end": v(407.02, 181.32) * mm});
            skLineSegment(sketch, "E29.0.1.60", {"start": v(402.4, 185.94) * mm, "end": v(402.4, 181.32) * mm});
            skLineSegment(sketch, "E29.0.1.63", {"start": v(326.2, 185.94) * mm, "end": v(330.82, 185.94) * mm});
            skLineSegment(sketch, "E29.0.1.64", {"start": v(377, 185.94) * mm, "end": v(381.62, 185.94) * mm});
            skLineSegment(sketch, "E29.0.1.66", {"start": v(300.8, 185.94) * mm, "end": v(300.8, 181.32) * mm});
            skLineSegment(sketch, "E29.0.1.67", {"start": v(351.6, 185.94) * mm, "end": v(351.6, 181.32) * mm});
            skLineSegment(sketch, "E29.0.1.68", {"start": v(356.22, 185.94) * mm, "end": v(356.22, 181.32) * mm});
            skLineSegment(sketch, "E29.0.1.69", {"start": v(407.02, 185.94) * mm, "end": v(407.02, 181.32) * mm});
            skLineSegment(sketch, "E29.0.1.73", {"start": v(305.42, 185.94) * mm, "end": v(305.42, 181.32) * mm});
            skLineSegment(sketch, "E30.1.0.8", {"start": v(364.31, 160.54) * mm, "end": v(368.94, 160.54) * mm});
            skLineSegment(sketch, "E30.1.0.9", {"start": v(292.74, 160.54) * mm, "end": v(292.74, 155.92) * mm});
            skLineSegment(sketch, "E30.1.0.15", {"start": v(288.1, 173.24) * mm, "end": v(288.1, 168.62) * mm});
            skLineSegment(sketch, "E30.1.0.16", {"start": v(343.54, 160.54) * mm, "end": v(343.54, 155.92) * mm});
            skLineSegment(sketch, "E30.1.0.17", {"start": v(305.44, 160.54) * mm, "end": v(305.44, 155.92) * mm});
            skLineSegment(sketch, "E30.1.0.18", {"start": v(288.11, 160.54) * mm, "end": v(292.74, 160.54) * mm});
            skLineSegment(sketch, "E30.1.0.23", {"start": v(313.5, 173.24) * mm, "end": v(318.13, 173.24) * mm});
            skLineSegment(sketch, "E30.1.0.24", {"start": v(364.3, 173.24) * mm, "end": v(368.93, 173.24) * mm});
            skLineSegment(sketch, "E30.1.0.25", {"start": v(330.84, 160.54) * mm, "end": v(330.84, 155.92) * mm});
            skLineSegment(sketch, "E30.1.0.26", {"start": v(351.61, 160.54) * mm, "end": v(356.24, 160.54) * mm});
            skLineSegment(sketch, "E30.1.0.27", {"start": v(351.61, 160.54) * mm, "end": v(351.61, 155.92) * mm});
            skLineSegment(sketch, "E30.1.0.28", {"start": v(338.9, 168.62) * mm, "end": v(343.53, 168.62) * mm});
            skLineSegment(sketch, "E30.1.0.29", {"start": v(389.7, 168.62) * mm, "end": v(394.33, 168.62) * mm});
            skLineSegment(sketch, "E30.1.0.32", {"start": v(288.1, 168.62) * mm, "end": v(292.73, 168.62) * mm});
            skLineSegment(sketch, "E30.1.0.33", {"start": v(377.01, 160.54) * mm, "end": v(377.01, 155.92) * mm});
            skLineSegment(sketch, "E30.1.0.34", {"start": v(338.91, 160.54) * mm, "end": v(343.54, 160.54) * mm});
            skLineSegment(sketch, "E30.1.0.35", {"start": v(338.91, 155.92) * mm, "end": v(343.54, 155.92) * mm});
            skLineSegment(sketch, "E30.1.0.36", {"start": v(300.81, 160.54) * mm, "end": v(300.81, 155.92) * mm});
            skLineSegment(sketch, "E30.1.0.37", {"start": v(389.71, 160.54) * mm, "end": v(389.71, 155.92) * mm});
            skLineSegment(sketch, "E30.1.0.38", {"start": v(343.53, 173.24) * mm, "end": v(343.53, 168.62) * mm});
            skLineSegment(sketch, "E30.1.0.39", {"start": v(394.33, 173.24) * mm, "end": v(394.33, 168.62) * mm});
            skLineSegment(sketch, "E30.1.0.40", {"start": v(326.21, 160.54) * mm, "end": v(326.21, 155.92) * mm});
            skLineSegment(sketch, "E30.1.0.42", {"start": v(394.34, 160.54) * mm, "end": v(394.34, 155.92) * mm});
            skLineSegment(sketch, "E30.1.0.44", {"start": v(292.73, 173.24) * mm, "end": v(292.73, 168.62) * mm});
            skLineSegment(sketch, "E30.1.0.45", {"start": v(402.4, 173.24) * mm, "end": v(402.4, 168.62) * mm});
            skLineSegment(sketch, "E30.1.0.46", {"start": v(389.71, 155.92) * mm, "end": v(394.34, 155.92) * mm});
            skLineSegment(sketch, "E30.1.0.47", {"start": v(389.71, 160.54) * mm, "end": v(394.34, 160.54) * mm});
            skLineSegment(sketch, "E30.1.0.51", {"start": v(313.51, 155.92) * mm, "end": v(318.14, 155.92) * mm});
            skLineSegment(sketch, "E30.1.0.53", {"start": v(300.8, 173.24) * mm, "end": v(300.8, 168.62) * mm});
            skLineSegment(sketch, "E30.1.0.54", {"start": v(338.9, 173.24) * mm, "end": v(343.53, 173.24) * mm});
            skLineSegment(sketch, "E30.1.0.55", {"start": v(389.7, 173.24) * mm, "end": v(394.33, 173.24) * mm});
            skLineSegment(sketch, "E30.1.0.56", {"start": v(351.6, 173.24) * mm, "end": v(351.6, 168.62) * mm});
            skLineSegment(sketch, "E30.1.0.57", {"start": v(318.14, 160.54) * mm, "end": v(318.14, 155.92) * mm});
            skLineSegment(sketch, "E30.1.0.59", {"start": v(288.1, 173.24) * mm, "end": v(292.73, 173.24) * mm});
            skLineSegment(sketch, "E30.1.0.64", {"start": v(356.23, 173.24) * mm, "end": v(356.23, 168.62) * mm});
            skLineSegment(sketch, "E30.1.0.65", {"start": v(407.03, 173.24) * mm, "end": v(407.03, 168.62) * mm});
            skLineSegment(sketch, "E30.1.0.66", {"start": v(288.11, 155.92) * mm, "end": v(292.74, 155.92) * mm});
            skLineSegment(sketch, "E30.1.0.67", {"start": v(313.51, 160.54) * mm, "end": v(318.14, 160.54) * mm});
            skLineSegment(sketch, "E30.1.0.68", {"start": v(377.01, 160.54) * mm, "end": v(381.64, 160.54) * mm});
            skLineSegment(sketch, "E30.1.0.69", {"start": v(288.11, 160.54) * mm, "end": v(288.11, 155.92) * mm});
            skLineSegment(sketch, "E30.1.0.70", {"start": v(368.94, 160.54) * mm, "end": v(368.94, 155.92) * mm});
            skLineSegment(sketch, "E30.1.0.74", {"start": v(326.2, 173.24) * mm, "end": v(326.2, 168.62) * mm});
            skLineSegment(sketch, "E30.1.0.75", {"start": v(377, 173.24) * mm, "end": v(377, 168.62) * mm});
            skLineSegment(sketch, "E30.1.0.77", {"start": v(305.43, 173.24) * mm, "end": v(305.43, 168.62) * mm});
            skLineSegment(sketch, "E30.1.0.79", {"start": v(326.21, 160.54) * mm, "end": v(330.84, 160.54) * mm});
            skLineSegment(sketch, "E30.1.0.80", {"start": v(402.41, 160.54) * mm, "end": v(407.04, 160.54) * mm});
            skLineSegment(sketch, "E30.1.0.82", {"start": v(300.81, 160.54) * mm, "end": v(305.44, 160.54) * mm});
            skLineSegment(sketch, "E30.1.0.85", {"start": v(326.2, 168.62) * mm, "end": v(330.83, 168.62) * mm});
            skLineSegment(sketch, "E30.1.0.86", {"start": v(377, 168.62) * mm, "end": v(381.63, 168.62) * mm});
            skLineSegment(sketch, "E30.1.0.87", {"start": v(313.5, 173.24) * mm, "end": v(313.5, 168.62) * mm});
            skLineSegment(sketch, "E30.1.0.91", {"start": v(381.64, 160.54) * mm, "end": v(381.64, 155.92) * mm});
            skLineSegment(sketch, "E30.1.0.93", {"start": v(402.41, 160.54) * mm, "end": v(402.41, 155.92) * mm});
            skLineSegment(sketch, "E30.1.0.95", {"start": v(402.4, 168.62) * mm, "end": v(407.03, 168.62) * mm});
            skLineSegment(sketch, "E30.1.0.98", {"start": v(330.83, 173.24) * mm, "end": v(330.83, 168.62) * mm});
            skLineSegment(sketch, "E30.1.0.99", {"start": v(381.63, 173.24) * mm, "end": v(381.63, 168.62) * mm});
            skLineSegment(sketch, "E30.1.0.100", {"start": v(364.31, 160.54) * mm, "end": v(364.31, 155.92) * mm});
            skLineSegment(sketch, "E30.1.0.101", {"start": v(326.21, 155.92) * mm, "end": v(330.84, 155.92) * mm});
            skLineSegment(sketch, "E30.1.0.102", {"start": v(364.3, 173.24) * mm, "end": v(364.3, 168.62) * mm});
            skLineSegment(sketch, "E30.1.0.104", {"start": v(300.8, 168.62) * mm, "end": v(305.43, 168.62) * mm});
            skLineSegment(sketch, "E30.1.0.105", {"start": v(351.6, 168.62) * mm, "end": v(356.23, 168.62) * mm});
            skLineSegment(sketch, "E30.1.0.107", {"start": v(364.31, 155.92) * mm, "end": v(368.94, 155.92) * mm});
            skLineSegment(sketch, "E30.1.0.108", {"start": v(351.61, 155.92) * mm, "end": v(356.24, 155.92) * mm});
            skLineSegment(sketch, "E30.1.0.109", {"start": v(407.04, 160.54) * mm, "end": v(407.04, 155.92) * mm});
            skLineSegment(sketch, "E30.1.0.110", {"start": v(351.6, 173.24) * mm, "end": v(356.23, 173.24) * mm});
            skLineSegment(sketch, "E30.1.0.111", {"start": v(402.4, 173.24) * mm, "end": v(407.03, 173.24) * mm});
            skLineSegment(sketch, "E30.1.0.114", {"start": v(300.8, 173.24) * mm, "end": v(305.43, 173.24) * mm});
            skLineSegment(sketch, "E30.1.0.116", {"start": v(338.91, 160.54) * mm, "end": v(338.91, 155.92) * mm});
            skLineSegment(sketch, "E30.1.0.119", {"start": v(326.2, 173.24) * mm, "end": v(330.83, 173.24) * mm});
            skLineSegment(sketch, "E30.1.0.120", {"start": v(377, 173.24) * mm, "end": v(381.63, 173.24) * mm});
            skLineSegment(sketch, "E30.1.0.121", {"start": v(377.01, 155.92) * mm, "end": v(381.64, 155.92) * mm});
            skLineSegment(sketch, "E30.1.0.122", {"start": v(300.81, 155.92) * mm, "end": v(305.44, 155.92) * mm});
            skLineSegment(sketch, "E30.1.0.123", {"start": v(356.24, 160.54) * mm, "end": v(356.24, 155.92) * mm});
            skLineSegment(sketch, "E30.1.0.124", {"start": v(338.9, 173.24) * mm, "end": v(338.9, 168.62) * mm});
            skLineSegment(sketch, "E30.1.0.125", {"start": v(389.7, 173.24) * mm, "end": v(389.7, 168.62) * mm});
            skLineSegment(sketch, "E30.1.0.130", {"start": v(402.41, 155.92) * mm, "end": v(407.04, 155.92) * mm});
            skLineSegment(sketch, "E30.1.0.132", {"start": v(368.93, 173.24) * mm, "end": v(368.93, 168.62) * mm});
            skLineSegment(sketch, "E30.1.0.133", {"start": v(318.13, 173.24) * mm, "end": v(318.13, 168.62) * mm});
            skLineSegment(sketch, "E30.1.0.137", {"start": v(364.3, 168.62) * mm, "end": v(368.93, 168.62) * mm});
            skLineSegment(sketch, "E30.1.0.138", {"start": v(313.5, 168.62) * mm, "end": v(318.13, 168.62) * mm});
            skLineSegment(sketch, "E30.1.0.143", {"start": v(313.51, 160.54) * mm, "end": v(313.51, 155.92) * mm});
            skLineSegment(sketch, "E30.2.0.8", {"start": v(364.33, 135.14) * mm, "end": v(368.95, 135.14) * mm});
            skLineSegment(sketch, "E30.2.0.9", {"start": v(292.75, 135.14) * mm, "end": v(292.75, 130.52) * mm});
            skLineSegment(sketch, "E30.2.0.15", {"start": v(288.12, 147.84) * mm, "end": v(288.12, 143.22) * mm});
            skLineSegment(sketch, "E30.2.0.16", {"start": v(343.55, 135.14) * mm, "end": v(343.55, 130.52) * mm});
            skLineSegment(sketch, "E30.2.0.17", {"start": v(305.45, 135.14) * mm, "end": v(305.45, 130.52) * mm});
            skLineSegment(sketch, "E30.2.0.18", {"start": v(288.13, 135.14) * mm, "end": v(292.75, 135.14) * mm});
            skLineSegment(sketch, "E30.2.0.23", {"start": v(313.52, 147.84) * mm, "end": v(318.14, 147.84) * mm});
            skLineSegment(sketch, "E30.2.0.24", {"start": v(364.32, 147.84) * mm, "end": v(368.94, 147.84) * mm});
            skLineSegment(sketch, "E30.2.0.25", {"start": v(330.85, 135.14) * mm, "end": v(330.85, 130.52) * mm});
            skLineSegment(sketch, "E30.2.0.26", {"start": v(351.63, 135.14) * mm, "end": v(356.25, 135.14) * mm});
            skLineSegment(sketch, "E30.2.0.27", {"start": v(351.63, 135.14) * mm, "end": v(351.63, 130.52) * mm});
            skLineSegment(sketch, "E30.2.0.28", {"start": v(338.92, 143.22) * mm, "end": v(343.54, 143.22) * mm});
            skLineSegment(sketch, "E30.2.0.29", {"start": v(389.72, 143.22) * mm, "end": v(394.34, 143.22) * mm});
            skLineSegment(sketch, "E30.2.0.32", {"start": v(288.12, 143.22) * mm, "end": v(292.74, 143.22) * mm});
            skLineSegment(sketch, "E30.2.0.33", {"start": v(377.03, 135.14) * mm, "end": v(377.03, 130.52) * mm});
            skLineSegment(sketch, "E30.2.0.34", {"start": v(338.93, 135.14) * mm, "end": v(343.55, 135.14) * mm});
            skLineSegment(sketch, "E30.2.0.35", {"start": v(338.93, 130.52) * mm, "end": v(343.55, 130.52) * mm});
            skLineSegment(sketch, "E30.2.0.36", {"start": v(300.83, 135.14) * mm, "end": v(300.83, 130.52) * mm});
            skLineSegment(sketch, "E30.2.0.37", {"start": v(389.73, 135.14) * mm, "end": v(389.73, 130.52) * mm});
            skLineSegment(sketch, "E30.2.0.38", {"start": v(343.54, 147.84) * mm, "end": v(343.54, 143.22) * mm});
            skLineSegment(sketch, "E30.2.0.39", {"start": v(394.34, 147.84) * mm, "end": v(394.34, 143.22) * mm});
            skLineSegment(sketch, "E30.2.0.40", {"start": v(326.23, 135.14) * mm, "end": v(326.23, 130.52) * mm});
            skLineSegment(sketch, "E30.2.0.42", {"start": v(394.35, 135.14) * mm, "end": v(394.35, 130.52) * mm});
            skLineSegment(sketch, "E30.2.0.44", {"start": v(292.74, 147.84) * mm, "end": v(292.74, 143.22) * mm});
            skLineSegment(sketch, "E30.2.0.45", {"start": v(402.42, 147.84) * mm, "end": v(402.42, 143.22) * mm});
            skLineSegment(sketch, "E30.2.0.46", {"start": v(389.73, 130.52) * mm, "end": v(394.35, 130.52) * mm});
            skLineSegment(sketch, "E30.2.0.47", {"start": v(389.73, 135.14) * mm, "end": v(394.35, 135.14) * mm});
            skLineSegment(sketch, "E30.2.0.51", {"start": v(313.53, 130.52) * mm, "end": v(318.15, 130.52) * mm});
            skLineSegment(sketch, "E30.2.0.53", {"start": v(300.82, 147.84) * mm, "end": v(300.82, 143.22) * mm});
            skLineSegment(sketch, "E30.2.0.54", {"start": v(338.92, 147.84) * mm, "end": v(343.54, 147.84) * mm});
            skLineSegment(sketch, "E30.2.0.55", {"start": v(389.72, 147.84) * mm, "end": v(394.34, 147.84) * mm});
            skLineSegment(sketch, "E30.2.0.56", {"start": v(351.62, 147.84) * mm, "end": v(351.62, 143.22) * mm});
            skLineSegment(sketch, "E30.2.0.57", {"start": v(318.15, 135.14) * mm, "end": v(318.15, 130.52) * mm});
            skLineSegment(sketch, "E30.2.0.59", {"start": v(288.12, 147.84) * mm, "end": v(292.74, 147.84) * mm});
            skLineSegment(sketch, "E30.2.0.64", {"start": v(356.24, 147.84) * mm, "end": v(356.24, 143.22) * mm});
            skLineSegment(sketch, "E30.2.0.65", {"start": v(407.04, 147.84) * mm, "end": v(407.04, 143.22) * mm});
            skLineSegment(sketch, "E30.2.0.66", {"start": v(288.13, 130.52) * mm, "end": v(292.75, 130.52) * mm});
            skLineSegment(sketch, "E30.2.0.67", {"start": v(313.53, 135.14) * mm, "end": v(318.15, 135.14) * mm});
            skLineSegment(sketch, "E30.2.0.68", {"start": v(377.03, 135.14) * mm, "end": v(381.65, 135.14) * mm});
            skLineSegment(sketch, "E30.2.0.69", {"start": v(288.13, 135.14) * mm, "end": v(288.13, 130.52) * mm});
            skLineSegment(sketch, "E30.2.0.70", {"start": v(368.95, 135.14) * mm, "end": v(368.95, 130.52) * mm});
            skLineSegment(sketch, "E30.2.0.74", {"start": v(326.22, 147.84) * mm, "end": v(326.22, 143.22) * mm});
            skLineSegment(sketch, "E30.2.0.75", {"start": v(377.02, 147.84) * mm, "end": v(377.02, 143.22) * mm});
            skLineSegment(sketch, "E30.2.0.77", {"start": v(305.44, 147.84) * mm, "end": v(305.44, 143.22) * mm});
            skLineSegment(sketch, "E30.2.0.79", {"start": v(326.23, 135.14) * mm, "end": v(330.85, 135.14) * mm});
            skLineSegment(sketch, "E30.2.0.80", {"start": v(402.43, 135.14) * mm, "end": v(407.05, 135.14) * mm});
            skLineSegment(sketch, "E30.2.0.82", {"start": v(300.83, 135.14) * mm, "end": v(305.45, 135.14) * mm});
            skLineSegment(sketch, "E30.2.0.85", {"start": v(326.22, 143.22) * mm, "end": v(330.84, 143.22) * mm});
            skLineSegment(sketch, "E30.2.0.86", {"start": v(377.02, 143.22) * mm, "end": v(381.64, 143.22) * mm});
            skLineSegment(sketch, "E30.2.0.87", {"start": v(313.52, 147.84) * mm, "end": v(313.52, 143.22) * mm});
            skLineSegment(sketch, "E30.2.0.91", {"start": v(381.65, 135.14) * mm, "end": v(381.65, 130.52) * mm});
            skLineSegment(sketch, "E30.2.0.93", {"start": v(402.43, 135.14) * mm, "end": v(402.43, 130.52) * mm});
            skLineSegment(sketch, "E30.2.0.95", {"start": v(402.42, 143.22) * mm, "end": v(407.04, 143.22) * mm});
            skLineSegment(sketch, "E30.2.0.98", {"start": v(330.84, 147.84) * mm, "end": v(330.84, 143.22) * mm});
            skLineSegment(sketch, "E30.2.0.99", {"start": v(381.64, 147.84) * mm, "end": v(381.64, 143.22) * mm});
            skLineSegment(sketch, "E30.2.0.100", {"start": v(364.33, 135.14) * mm, "end": v(364.33, 130.52) * mm});
            skLineSegment(sketch, "E30.2.0.101", {"start": v(326.23, 130.52) * mm, "end": v(330.85, 130.52) * mm});
            skLineSegment(sketch, "E30.2.0.102", {"start": v(364.32, 147.84) * mm, "end": v(364.32, 143.22) * mm});
            skLineSegment(sketch, "E30.2.0.104", {"start": v(300.82, 143.22) * mm, "end": v(305.44, 143.22) * mm});
            skLineSegment(sketch, "E30.2.0.105", {"start": v(351.62, 143.22) * mm, "end": v(356.24, 143.22) * mm});
            skLineSegment(sketch, "E30.2.0.107", {"start": v(364.33, 130.52) * mm, "end": v(368.95, 130.52) * mm});
            skLineSegment(sketch, "E30.2.0.108", {"start": v(351.63, 130.52) * mm, "end": v(356.25, 130.52) * mm});
            skLineSegment(sketch, "E30.2.0.109", {"start": v(407.05, 135.14) * mm, "end": v(407.05, 130.52) * mm});
            skLineSegment(sketch, "E30.2.0.110", {"start": v(351.62, 147.84) * mm, "end": v(356.24, 147.84) * mm});
            skLineSegment(sketch, "E30.2.0.111", {"start": v(402.42, 147.84) * mm, "end": v(407.04, 147.84) * mm});
            skLineSegment(sketch, "E30.2.0.114", {"start": v(300.82, 147.84) * mm, "end": v(305.44, 147.84) * mm});
            skLineSegment(sketch, "E30.2.0.116", {"start": v(338.93, 135.14) * mm, "end": v(338.93, 130.52) * mm});
            skLineSegment(sketch, "E30.2.0.119", {"start": v(326.22, 147.84) * mm, "end": v(330.84, 147.84) * mm});
            skLineSegment(sketch, "E30.2.0.120", {"start": v(377.02, 147.84) * mm, "end": v(381.64, 147.84) * mm});
            skLineSegment(sketch, "E30.2.0.121", {"start": v(377.03, 130.52) * mm, "end": v(381.65, 130.52) * mm});
            skLineSegment(sketch, "E30.2.0.122", {"start": v(300.83, 130.52) * mm, "end": v(305.45, 130.52) * mm});
            skLineSegment(sketch, "E30.2.0.123", {"start": v(356.25, 135.14) * mm, "end": v(356.25, 130.52) * mm});
            skLineSegment(sketch, "E30.2.0.124", {"start": v(338.92, 147.84) * mm, "end": v(338.92, 143.22) * mm});
            skLineSegment(sketch, "E30.2.0.125", {"start": v(389.72, 147.84) * mm, "end": v(389.72, 143.22) * mm});
            skLineSegment(sketch, "E30.2.0.130", {"start": v(402.43, 130.52) * mm, "end": v(407.05, 130.52) * mm});
            skLineSegment(sketch, "E30.2.0.132", {"start": v(368.94, 147.84) * mm, "end": v(368.94, 143.22) * mm});
            skLineSegment(sketch, "E30.2.0.133", {"start": v(318.14, 147.84) * mm, "end": v(318.14, 143.22) * mm});
            skLineSegment(sketch, "E30.2.0.137", {"start": v(364.32, 143.22) * mm, "end": v(368.94, 143.22) * mm});
            skLineSegment(sketch, "E30.2.0.138", {"start": v(313.52, 143.22) * mm, "end": v(318.14, 143.22) * mm});
            skLineSegment(sketch, "E30.2.0.143", {"start": v(313.53, 135.14) * mm, "end": v(313.53, 130.52) * mm});
            skLineSegment(sketch, "E30.3.0.8", {"start": v(364.35, 109.74) * mm, "end": v(368.97, 109.74) * mm});
            skLineSegment(sketch, "E30.3.0.9", {"start": v(292.77, 109.74) * mm, "end": v(292.77, 105.12) * mm});
            skLineSegment(sketch, "E30.3.0.15", {"start": v(288.14, 122.44) * mm, "end": v(288.14, 117.82) * mm});
            skLineSegment(sketch, "E30.3.0.16", {"start": v(343.57, 109.74) * mm, "end": v(343.57, 105.12) * mm});
            skLineSegment(sketch, "E30.3.0.17", {"start": v(305.47, 109.74) * mm, "end": v(305.47, 105.12) * mm});
            skLineSegment(sketch, "E30.3.0.18", {"start": v(288.15, 109.74) * mm, "end": v(292.77, 109.74) * mm});
            skLineSegment(sketch, "E30.3.0.23", {"start": v(313.54, 122.44) * mm, "end": v(318.16, 122.44) * mm});
            skLineSegment(sketch, "E30.3.0.24", {"start": v(364.34, 122.44) * mm, "end": v(368.96, 122.44) * mm});
            skLineSegment(sketch, "E30.3.0.25", {"start": v(330.87, 109.74) * mm, "end": v(330.87, 105.12) * mm});
            skLineSegment(sketch, "E30.3.0.26", {"start": v(351.65, 109.74) * mm, "end": v(356.27, 109.74) * mm});
            skLineSegment(sketch, "E30.3.0.27", {"start": v(351.65, 109.74) * mm, "end": v(351.65, 105.12) * mm});
            skLineSegment(sketch, "E30.3.0.28", {"start": v(338.94, 117.82) * mm, "end": v(343.56, 117.82) * mm});
            skLineSegment(sketch, "E30.3.0.29", {"start": v(389.74, 117.82) * mm, "end": v(394.36, 117.82) * mm});
            skLineSegment(sketch, "E30.3.0.32", {"start": v(288.14, 117.82) * mm, "end": v(292.76, 117.82) * mm});
            skLineSegment(sketch, "E30.3.0.33", {"start": v(377.05, 109.74) * mm, "end": v(377.05, 105.12) * mm});
            skLineSegment(sketch, "E30.3.0.34", {"start": v(338.95, 109.74) * mm, "end": v(343.57, 109.74) * mm});
            skLineSegment(sketch, "E30.3.0.35", {"start": v(338.95, 105.12) * mm, "end": v(343.57, 105.12) * mm});
            skLineSegment(sketch, "E30.3.0.36", {"start": v(300.85, 109.74) * mm, "end": v(300.85, 105.12) * mm});
            skLineSegment(sketch, "E30.3.0.37", {"start": v(389.75, 109.74) * mm, "end": v(389.75, 105.12) * mm});
            skLineSegment(sketch, "E30.3.0.38", {"start": v(343.56, 122.44) * mm, "end": v(343.56, 117.82) * mm});
            skLineSegment(sketch, "E30.3.0.39", {"start": v(394.36, 122.44) * mm, "end": v(394.36, 117.82) * mm});
            skLineSegment(sketch, "E30.3.0.40", {"start": v(326.25, 109.74) * mm, "end": v(326.25, 105.12) * mm});
            skLineSegment(sketch, "E30.3.0.42", {"start": v(394.37, 109.74) * mm, "end": v(394.37, 105.12) * mm});
            skLineSegment(sketch, "E30.3.0.44", {"start": v(292.76, 122.44) * mm, "end": v(292.76, 117.82) * mm});
            skLineSegment(sketch, "E30.3.0.45", {"start": v(402.44, 122.44) * mm, "end": v(402.44, 117.82) * mm});
            skLineSegment(sketch, "E30.3.0.46", {"start": v(389.75, 105.12) * mm, "end": v(394.37, 105.12) * mm});
            skLineSegment(sketch, "E30.3.0.47", {"start": v(389.75, 109.74) * mm, "end": v(394.37, 109.74) * mm});
            skLineSegment(sketch, "E30.3.0.51", {"start": v(313.55, 105.12) * mm, "end": v(318.17, 105.12) * mm});
            skLineSegment(sketch, "E30.3.0.53", {"start": v(300.84, 122.44) * mm, "end": v(300.84, 117.82) * mm});
            skLineSegment(sketch, "E30.3.0.54", {"start": v(338.94, 122.44) * mm, "end": v(343.56, 122.44) * mm});
            skLineSegment(sketch, "E30.3.0.55", {"start": v(389.74, 122.44) * mm, "end": v(394.36, 122.44) * mm});
            skLineSegment(sketch, "E30.3.0.56", {"start": v(351.64, 122.44) * mm, "end": v(351.64, 117.82) * mm});
            skLineSegment(sketch, "E30.3.0.57", {"start": v(318.17, 109.74) * mm, "end": v(318.17, 105.12) * mm});
            skLineSegment(sketch, "E30.3.0.59", {"start": v(288.14, 122.44) * mm, "end": v(292.76, 122.44) * mm});
            skLineSegment(sketch, "E30.3.0.64", {"start": v(356.26, 122.44) * mm, "end": v(356.26, 117.82) * mm});
            skLineSegment(sketch, "E30.3.0.65", {"start": v(407.06, 122.44) * mm, "end": v(407.06, 117.82) * mm});
            skLineSegment(sketch, "E30.3.0.66", {"start": v(288.15, 105.12) * mm, "end": v(292.77, 105.12) * mm});
            skLineSegment(sketch, "E30.3.0.67", {"start": v(313.55, 109.74) * mm, "end": v(318.17, 109.74) * mm});
            skLineSegment(sketch, "E30.3.0.68", {"start": v(377.05, 109.74) * mm, "end": v(381.67, 109.74) * mm});
            skLineSegment(sketch, "E30.3.0.69", {"start": v(288.15, 109.74) * mm, "end": v(288.15, 105.12) * mm});
            skLineSegment(sketch, "E30.3.0.70", {"start": v(368.97, 109.74) * mm, "end": v(368.97, 105.12) * mm});
            skLineSegment(sketch, "E30.3.0.74", {"start": v(326.24, 122.44) * mm, "end": v(326.24, 117.82) * mm});
            skLineSegment(sketch, "E30.3.0.75", {"start": v(377.04, 122.44) * mm, "end": v(377.04, 117.82) * mm});
            skLineSegment(sketch, "E30.3.0.77", {"start": v(305.46, 122.44) * mm, "end": v(305.46, 117.82) * mm});
            skLineSegment(sketch, "E30.3.0.79", {"start": v(326.25, 109.74) * mm, "end": v(330.87, 109.74) * mm});
            skLineSegment(sketch, "E30.3.0.80", {"start": v(402.45, 109.74) * mm, "end": v(407.07, 109.74) * mm});
            skLineSegment(sketch, "E30.3.0.82", {"start": v(300.85, 109.74) * mm, "end": v(305.47, 109.74) * mm});
            skLineSegment(sketch, "E30.3.0.85", {"start": v(326.24, 117.82) * mm, "end": v(330.86, 117.82) * mm});
            skLineSegment(sketch, "E30.3.0.86", {"start": v(377.04, 117.82) * mm, "end": v(381.66, 117.82) * mm});
            skLineSegment(sketch, "E30.3.0.87", {"start": v(313.54, 122.44) * mm, "end": v(313.54, 117.82) * mm});
            skLineSegment(sketch, "E30.3.0.91", {"start": v(381.67, 109.74) * mm, "end": v(381.67, 105.12) * mm});
            skLineSegment(sketch, "E30.3.0.93", {"start": v(402.45, 109.74) * mm, "end": v(402.45, 105.12) * mm});
            skLineSegment(sketch, "E30.3.0.95", {"start": v(402.44, 117.82) * mm, "end": v(407.06, 117.82) * mm});
            skLineSegment(sketch, "E30.3.0.98", {"start": v(330.86, 122.44) * mm, "end": v(330.86, 117.82) * mm});
            skLineSegment(sketch, "E30.3.0.99", {"start": v(381.66, 122.44) * mm, "end": v(381.66, 117.82) * mm});
            skLineSegment(sketch, "E30.3.0.100", {"start": v(364.35, 109.74) * mm, "end": v(364.35, 105.12) * mm});
            skLineSegment(sketch, "E30.3.0.101", {"start": v(326.25, 105.12) * mm, "end": v(330.87, 105.12) * mm});
            skLineSegment(sketch, "E30.3.0.102", {"start": v(364.34, 122.44) * mm, "end": v(364.34, 117.82) * mm});
            skLineSegment(sketch, "E30.3.0.104", {"start": v(300.84, 117.82) * mm, "end": v(305.46, 117.82) * mm});
            skLineSegment(sketch, "E30.3.0.105", {"start": v(351.64, 117.82) * mm, "end": v(356.26, 117.82) * mm});
            skLineSegment(sketch, "E30.3.0.107", {"start": v(364.35, 105.12) * mm, "end": v(368.97, 105.12) * mm});
            skLineSegment(sketch, "E30.3.0.108", {"start": v(351.65, 105.12) * mm, "end": v(356.27, 105.12) * mm});
            skLineSegment(sketch, "E30.3.0.109", {"start": v(407.07, 109.74) * mm, "end": v(407.07, 105.12) * mm});
            skLineSegment(sketch, "E30.3.0.110", {"start": v(351.64, 122.44) * mm, "end": v(356.26, 122.44) * mm});
            skLineSegment(sketch, "E30.3.0.111", {"start": v(402.44, 122.44) * mm, "end": v(407.06, 122.44) * mm});
            skLineSegment(sketch, "E30.3.0.114", {"start": v(300.84, 122.44) * mm, "end": v(305.46, 122.44) * mm});
            skLineSegment(sketch, "E30.3.0.116", {"start": v(338.95, 109.74) * mm, "end": v(338.95, 105.12) * mm});
            skLineSegment(sketch, "E30.3.0.119", {"start": v(326.24, 122.44) * mm, "end": v(330.86, 122.44) * mm});
            skLineSegment(sketch, "E30.3.0.120", {"start": v(377.04, 122.44) * mm, "end": v(381.66, 122.44) * mm});
            skLineSegment(sketch, "E30.3.0.121", {"start": v(377.05, 105.12) * mm, "end": v(381.67, 105.12) * mm});
            skLineSegment(sketch, "E30.3.0.122", {"start": v(300.85, 105.12) * mm, "end": v(305.47, 105.12) * mm});
            skLineSegment(sketch, "E30.3.0.123", {"start": v(356.27, 109.74) * mm, "end": v(356.27, 105.12) * mm});
            skLineSegment(sketch, "E30.3.0.124", {"start": v(338.94, 122.44) * mm, "end": v(338.94, 117.82) * mm});
            skLineSegment(sketch, "E30.3.0.125", {"start": v(389.74, 122.44) * mm, "end": v(389.74, 117.82) * mm});
            skLineSegment(sketch, "E30.3.0.130", {"start": v(402.45, 105.12) * mm, "end": v(407.07, 105.12) * mm});
            skLineSegment(sketch, "E30.3.0.132", {"start": v(368.96, 122.44) * mm, "end": v(368.96, 117.82) * mm});
            skLineSegment(sketch, "E30.3.0.133", {"start": v(318.16, 122.44) * mm, "end": v(318.16, 117.82) * mm});
            skLineSegment(sketch, "E30.3.0.137", {"start": v(364.34, 117.82) * mm, "end": v(368.96, 117.82) * mm});
            skLineSegment(sketch, "E30.3.0.138", {"start": v(313.54, 117.82) * mm, "end": v(318.16, 117.82) * mm});
            skLineSegment(sketch, "E30.3.0.143", {"start": v(313.55, 109.74) * mm, "end": v(313.55, 105.12) * mm});
            skLineSegment(sketch, "E30.4.0.8", {"start": v(364.37, 84.34) * mm, "end": v(369, 84.34) * mm});
            skLineSegment(sketch, "E30.4.0.9", {"start": v(292.8, 84.34) * mm, "end": v(292.8, 79.72) * mm});
            skLineSegment(sketch, "E30.4.0.15", {"start": v(288.16, 97.04) * mm, "end": v(288.16, 92.42) * mm});
            skLineSegment(sketch, "E30.4.0.16", {"start": v(343.6, 84.34) * mm, "end": v(343.6, 79.72) * mm});
            skLineSegment(sketch, "E30.4.0.17", {"start": v(305.5, 84.34) * mm, "end": v(305.5, 79.72) * mm});
            skLineSegment(sketch, "E30.4.0.18", {"start": v(288.17, 84.34) * mm, "end": v(292.8, 84.34) * mm});
            skLineSegment(sketch, "E30.4.0.23", {"start": v(313.56, 97.04) * mm, "end": v(318.18, 97.04) * mm});
            skLineSegment(sketch, "E30.4.0.24", {"start": v(364.36, 97.04) * mm, "end": v(368.98, 97.04) * mm});
            skLineSegment(sketch, "E30.4.0.25", {"start": v(330.9, 84.34) * mm, "end": v(330.9, 79.72) * mm});
            skLineSegment(sketch, "E30.4.0.26", {"start": v(351.67, 84.34) * mm, "end": v(356.3, 84.34) * mm});
            skLineSegment(sketch, "E30.4.0.27", {"start": v(351.67, 84.34) * mm, "end": v(351.67, 79.72) * mm});
            skLineSegment(sketch, "E30.4.0.28", {"start": v(338.96, 92.42) * mm, "end": v(343.58, 92.42) * mm});
            skLineSegment(sketch, "E30.4.0.29", {"start": v(389.76, 92.42) * mm, "end": v(394.38, 92.42) * mm});
            skLineSegment(sketch, "E30.4.0.32", {"start": v(288.16, 92.42) * mm, "end": v(292.78, 92.42) * mm});
            skLineSegment(sketch, "E30.4.0.33", {"start": v(377.07, 84.34) * mm, "end": v(377.07, 79.72) * mm});
            skLineSegment(sketch, "E30.4.0.34", {"start": v(338.97, 84.34) * mm, "end": v(343.6, 84.34) * mm});
            skLineSegment(sketch, "E30.4.0.35", {"start": v(338.97, 79.72) * mm, "end": v(343.6, 79.72) * mm});
            skLineSegment(sketch, "E30.4.0.36", {"start": v(300.87, 84.34) * mm, "end": v(300.87, 79.72) * mm});
            skLineSegment(sketch, "E30.4.0.37", {"start": v(389.77, 84.34) * mm, "end": v(389.77, 79.72) * mm});
            skLineSegment(sketch, "E30.4.0.38", {"start": v(343.58, 97.04) * mm, "end": v(343.58, 92.42) * mm});
            skLineSegment(sketch, "E30.4.0.39", {"start": v(394.38, 97.04) * mm, "end": v(394.38, 92.42) * mm});
            skLineSegment(sketch, "E30.4.0.40", {"start": v(326.27, 84.34) * mm, "end": v(326.27, 79.72) * mm});
            skLineSegment(sketch, "E30.4.0.42", {"start": v(394.4, 84.34) * mm, "end": v(394.4, 79.72) * mm});
            skLineSegment(sketch, "E30.4.0.44", {"start": v(292.78, 97.04) * mm, "end": v(292.78, 92.42) * mm});
            skLineSegment(sketch, "E30.4.0.45", {"start": v(402.46, 97.04) * mm, "end": v(402.46, 92.42) * mm});
            skLineSegment(sketch, "E30.4.0.46", {"start": v(389.77, 79.72) * mm, "end": v(394.4, 79.72) * mm});
            skLineSegment(sketch, "E30.4.0.47", {"start": v(389.77, 84.34) * mm, "end": v(394.4, 84.34) * mm});
            skLineSegment(sketch, "E30.4.0.51", {"start": v(313.57, 79.72) * mm, "end": v(318.2, 79.72) * mm});
            skLineSegment(sketch, "E30.4.0.53", {"start": v(300.86, 97.04) * mm, "end": v(300.86, 92.42) * mm});
            skLineSegment(sketch, "E30.4.0.54", {"start": v(338.96, 97.04) * mm, "end": v(343.58, 97.04) * mm});
            skLineSegment(sketch, "E30.4.0.55", {"start": v(389.76, 97.04) * mm, "end": v(394.38, 97.04) * mm});
            skLineSegment(sketch, "E30.4.0.56", {"start": v(351.66, 97.04) * mm, "end": v(351.66, 92.42) * mm});
            skLineSegment(sketch, "E30.4.0.57", {"start": v(318.2, 84.34) * mm, "end": v(318.2, 79.72) * mm});
            skLineSegment(sketch, "E30.4.0.59", {"start": v(288.16, 97.04) * mm, "end": v(292.78, 97.04) * mm});
            skLineSegment(sketch, "E30.4.0.64", {"start": v(356.28, 97.04) * mm, "end": v(356.28, 92.42) * mm});
            skLineSegment(sketch, "E30.4.0.65", {"start": v(407.08, 97.04) * mm, "end": v(407.08, 92.42) * mm});
            skLineSegment(sketch, "E30.4.0.66", {"start": v(288.17, 79.72) * mm, "end": v(292.8, 79.72) * mm});
            skLineSegment(sketch, "E30.4.0.67", {"start": v(313.57, 84.34) * mm, "end": v(318.2, 84.34) * mm});
            skLineSegment(sketch, "E30.4.0.68", {"start": v(377.07, 84.34) * mm, "end": v(381.7, 84.34) * mm});
            skLineSegment(sketch, "E30.4.0.69", {"start": v(288.17, 84.34) * mm, "end": v(288.17, 79.72) * mm});
            skLineSegment(sketch, "E30.4.0.70", {"start": v(369, 84.34) * mm, "end": v(369, 79.72) * mm});
            skLineSegment(sketch, "E30.4.0.74", {"start": v(326.26, 97.04) * mm, "end": v(326.26, 92.42) * mm});
            skLineSegment(sketch, "E30.4.0.75", {"start": v(377.06, 97.04) * mm, "end": v(377.06, 92.42) * mm});
            skLineSegment(sketch, "E30.4.0.77", {"start": v(305.48, 97.04) * mm, "end": v(305.48, 92.42) * mm});
            skLineSegment(sketch, "E30.4.0.79", {"start": v(326.27, 84.34) * mm, "end": v(330.9, 84.34) * mm});
            skLineSegment(sketch, "E30.4.0.80", {"start": v(402.47, 84.34) * mm, "end": v(407.1, 84.34) * mm});
            skLineSegment(sketch, "E30.4.0.82", {"start": v(300.87, 84.34) * mm, "end": v(305.5, 84.34) * mm});
            skLineSegment(sketch, "E30.4.0.85", {"start": v(326.26, 92.42) * mm, "end": v(330.88, 92.42) * mm});
            skLineSegment(sketch, "E30.4.0.86", {"start": v(377.06, 92.42) * mm, "end": v(381.68, 92.42) * mm});
            skLineSegment(sketch, "E30.4.0.87", {"start": v(313.56, 97.04) * mm, "end": v(313.56, 92.42) * mm});
            skLineSegment(sketch, "E30.4.0.91", {"start": v(381.7, 84.34) * mm, "end": v(381.7, 79.72) * mm});
            skLineSegment(sketch, "E30.4.0.93", {"start": v(402.47, 84.34) * mm, "end": v(402.47, 79.72) * mm});
            skLineSegment(sketch, "E30.4.0.95", {"start": v(402.46, 92.42) * mm, "end": v(407.08, 92.42) * mm});
            skLineSegment(sketch, "E30.4.0.98", {"start": v(330.88, 97.04) * mm, "end": v(330.88, 92.42) * mm});
            skLineSegment(sketch, "E30.4.0.99", {"start": v(381.68, 97.04) * mm, "end": v(381.68, 92.42) * mm});
            skLineSegment(sketch, "E30.4.0.100", {"start": v(364.37, 84.34) * mm, "end": v(364.37, 79.72) * mm});
            skLineSegment(sketch, "E30.4.0.101", {"start": v(326.27, 79.72) * mm, "end": v(330.9, 79.72) * mm});
            skLineSegment(sketch, "E30.4.0.102", {"start": v(364.36, 97.04) * mm, "end": v(364.36, 92.42) * mm});
            skLineSegment(sketch, "E30.4.0.104", {"start": v(300.86, 92.42) * mm, "end": v(305.48, 92.42) * mm});
            skLineSegment(sketch, "E30.4.0.105", {"start": v(351.66, 92.42) * mm, "end": v(356.28, 92.42) * mm});
            skLineSegment(sketch, "E30.4.0.107", {"start": v(364.37, 79.72) * mm, "end": v(369, 79.72) * mm});
            skLineSegment(sketch, "E30.4.0.108", {"start": v(351.67, 79.72) * mm, "end": v(356.3, 79.72) * mm});
            skLineSegment(sketch, "E30.4.0.109", {"start": v(407.1, 84.34) * mm, "end": v(407.1, 79.72) * mm});
            skLineSegment(sketch, "E30.4.0.110", {"start": v(351.66, 97.04) * mm, "end": v(356.28, 97.04) * mm});
            skLineSegment(sketch, "E30.4.0.111", {"start": v(402.46, 97.04) * mm, "end": v(407.08, 97.04) * mm});
            skLineSegment(sketch, "E30.4.0.114", {"start": v(300.86, 97.04) * mm, "end": v(305.48, 97.04) * mm});
            skLineSegment(sketch, "E30.4.0.116", {"start": v(338.97, 84.34) * mm, "end": v(338.97, 79.72) * mm});
            skLineSegment(sketch, "E30.4.0.119", {"start": v(326.26, 97.04) * mm, "end": v(330.88, 97.04) * mm});
            skLineSegment(sketch, "E30.4.0.120", {"start": v(377.06, 97.04) * mm, "end": v(381.68, 97.04) * mm});
            skLineSegment(sketch, "E30.4.0.121", {"start": v(377.07, 79.72) * mm, "end": v(381.7, 79.72) * mm});
            skLineSegment(sketch, "E30.4.0.122", {"start": v(300.87, 79.72) * mm, "end": v(305.5, 79.72) * mm});
            skLineSegment(sketch, "E30.4.0.123", {"start": v(356.3, 84.34) * mm, "end": v(356.3, 79.72) * mm});
            skLineSegment(sketch, "E30.4.0.124", {"start": v(338.96, 97.04) * mm, "end": v(338.96, 92.42) * mm});
            skLineSegment(sketch, "E30.4.0.125", {"start": v(389.76, 97.04) * mm, "end": v(389.76, 92.42) * mm});
            skLineSegment(sketch, "E30.4.0.130", {"start": v(402.47, 79.72) * mm, "end": v(407.1, 79.72) * mm});
            skLineSegment(sketch, "E30.4.0.133", {"start": v(318.18, 97.04) * mm, "end": v(318.18, 92.42) * mm});
            skLineSegment(sketch, "E30.4.0.137", {"start": v(364.36, 92.42) * mm, "end": v(368.98, 92.42) * mm});
            skLineSegment(sketch, "E30.4.0.138", {"start": v(313.56, 92.42) * mm, "end": v(318.18, 92.42) * mm});
            skLineSegment(sketch, "E30.4.0.143", {"start": v(313.57, 84.34) * mm, "end": v(313.57, 79.72) * mm});
            skLineSegment(sketch, "E30.5.0.8", {"start": v(364.39, 58.94) * mm, "end": v(369, 58.94) * mm});
            skLineSegment(sketch, "E30.5.0.9", {"start": v(292.8, 58.94) * mm, "end": v(292.8, 54.32) * mm});
            skLineSegment(sketch, "E30.5.0.15", {"start": v(288.18, 71.64) * mm, "end": v(288.18, 67.02) * mm});
            skLineSegment(sketch, "E30.5.0.16", {"start": v(343.6, 58.94) * mm, "end": v(343.6, 54.32) * mm});
            skLineSegment(sketch, "E30.5.0.17", {"start": v(305.5, 58.94) * mm, "end": v(305.5, 54.32) * mm});
            skLineSegment(sketch, "E30.5.0.18", {"start": v(288.19, 58.94) * mm, "end": v(292.8, 58.94) * mm});
            skLineSegment(sketch, "E30.5.0.23", {"start": v(313.58, 71.64) * mm, "end": v(318.2, 71.64) * mm});
            skLineSegment(sketch, "E30.5.0.24", {"start": v(364.38, 71.64) * mm, "end": v(369, 71.64) * mm});
            skLineSegment(sketch, "E30.5.0.25", {"start": v(330.9, 58.94) * mm, "end": v(330.9, 54.32) * mm});
            skLineSegment(sketch, "E30.5.0.26", {"start": v(351.69, 58.94) * mm, "end": v(356.3, 58.94) * mm});
            skLineSegment(sketch, "E30.5.0.27", {"start": v(351.69, 58.94) * mm, "end": v(351.69, 54.32) * mm});
            skLineSegment(sketch, "E30.5.0.28", {"start": v(338.98, 67.02) * mm, "end": v(343.6, 67.02) * mm});
            skLineSegment(sketch, "E30.5.0.29", {"start": v(389.78, 67.02) * mm, "end": v(394.4, 67.02) * mm});
            skLineSegment(sketch, "E30.5.0.32", {"start": v(288.18, 67.02) * mm, "end": v(292.8, 67.02) * mm});
            skLineSegment(sketch, "E30.5.0.33", {"start": v(377.09, 58.94) * mm, "end": v(377.09, 54.32) * mm});
            skLineSegment(sketch, "E30.5.0.34", {"start": v(338.99, 58.94) * mm, "end": v(343.6, 58.94) * mm});
            skLineSegment(sketch, "E30.5.0.35", {"start": v(338.99, 54.32) * mm, "end": v(343.6, 54.32) * mm});
            skLineSegment(sketch, "E30.5.0.36", {"start": v(300.89, 58.94) * mm, "end": v(300.89, 54.32) * mm});
            skLineSegment(sketch, "E30.5.0.37", {"start": v(389.79, 58.94) * mm, "end": v(389.79, 54.32) * mm});
            skLineSegment(sketch, "E30.5.0.38", {"start": v(343.6, 71.64) * mm, "end": v(343.6, 67.02) * mm});
            skLineSegment(sketch, "E30.5.0.39", {"start": v(394.4, 71.64) * mm, "end": v(394.4, 67.02) * mm});
            skLineSegment(sketch, "E30.5.0.40", {"start": v(326.29, 58.94) * mm, "end": v(326.29, 54.32) * mm});
            skLineSegment(sketch, "E30.5.0.42", {"start": v(394.4, 58.94) * mm, "end": v(394.4, 54.32) * mm});
            skLineSegment(sketch, "E30.5.0.44", {"start": v(292.8, 71.64) * mm, "end": v(292.8, 67.02) * mm});
            skLineSegment(sketch, "E30.5.0.45", {"start": v(402.48, 71.64) * mm, "end": v(402.48, 67.02) * mm});
            skLineSegment(sketch, "E30.5.0.46", {"start": v(389.79, 54.32) * mm, "end": v(394.4, 54.32) * mm});
            skLineSegment(sketch, "E30.5.0.47", {"start": v(389.79, 58.94) * mm, "end": v(394.4, 58.94) * mm});
            skLineSegment(sketch, "E30.5.0.51", {"start": v(313.59, 54.32) * mm, "end": v(318.2, 54.32) * mm});
            skLineSegment(sketch, "E30.5.0.53", {"start": v(300.88, 71.64) * mm, "end": v(300.88, 67.02) * mm});
            skLineSegment(sketch, "E30.5.0.54", {"start": v(338.98, 71.64) * mm, "end": v(343.6, 71.64) * mm});
            skLineSegment(sketch, "E30.5.0.55", {"start": v(389.78, 71.64) * mm, "end": v(394.4, 71.64) * mm});
            skLineSegment(sketch, "E30.5.0.56", {"start": v(351.68, 71.64) * mm, "end": v(351.68, 67.02) * mm});
            skLineSegment(sketch, "E30.5.0.57", {"start": v(318.2, 58.94) * mm, "end": v(318.2, 54.32) * mm});
            skLineSegment(sketch, "E30.5.0.59", {"start": v(288.18, 71.64) * mm, "end": v(292.8, 71.64) * mm});
            skLineSegment(sketch, "E30.5.0.64", {"start": v(356.3, 71.64) * mm, "end": v(356.3, 67.02) * mm});
            skLineSegment(sketch, "E30.5.0.65", {"start": v(407.1, 71.64) * mm, "end": v(407.1, 67.02) * mm});
            skLineSegment(sketch, "E30.5.0.66", {"start": v(288.19, 54.32) * mm, "end": v(292.8, 54.32) * mm});
            skLineSegment(sketch, "E30.5.0.67", {"start": v(313.59, 58.94) * mm, "end": v(318.2, 58.94) * mm});
            skLineSegment(sketch, "E30.5.0.68", {"start": v(377.09, 58.94) * mm, "end": v(381.7, 58.94) * mm});
            skLineSegment(sketch, "E30.5.0.69", {"start": v(288.19, 58.94) * mm, "end": v(288.19, 54.32) * mm});
            skLineSegment(sketch, "E30.5.0.70", {"start": v(369, 58.94) * mm, "end": v(369, 54.32) * mm});
            skLineSegment(sketch, "E30.5.0.74", {"start": v(326.28, 71.64) * mm, "end": v(326.28, 67.02) * mm});
            skLineSegment(sketch, "E30.5.0.75", {"start": v(377.08, 71.64) * mm, "end": v(377.08, 67.02) * mm});
            skLineSegment(sketch, "E30.5.0.77", {"start": v(305.5, 71.64) * mm, "end": v(305.5, 67.02) * mm});
            skLineSegment(sketch, "E30.5.0.79", {"start": v(326.29, 58.94) * mm, "end": v(330.9, 58.94) * mm});
            skLineSegment(sketch, "E30.5.0.80", {"start": v(402.49, 58.94) * mm, "end": v(407.1, 58.94) * mm});
            skLineSegment(sketch, "E30.5.0.82", {"start": v(300.89, 58.94) * mm, "end": v(305.5, 58.94) * mm});
            skLineSegment(sketch, "E30.5.0.85", {"start": v(326.28, 67.02) * mm, "end": v(330.9, 67.02) * mm});
            skLineSegment(sketch, "E30.5.0.86", {"start": v(377.08, 67.02) * mm, "end": v(381.7, 67.02) * mm});
            skLineSegment(sketch, "E30.5.0.87", {"start": v(313.58, 71.64) * mm, "end": v(313.58, 67.02) * mm});
            skLineSegment(sketch, "E30.5.0.91", {"start": v(381.7, 58.94) * mm, "end": v(381.7, 54.32) * mm});
            skLineSegment(sketch, "E30.5.0.93", {"start": v(402.49, 58.94) * mm, "end": v(402.49, 54.32) * mm});
            skLineSegment(sketch, "E30.5.0.95", {"start": v(402.48, 67.02) * mm, "end": v(407.1, 67.02) * mm});
            skLineSegment(sketch, "E30.5.0.98", {"start": v(330.9, 71.64) * mm, "end": v(330.9, 67.02) * mm});
            skLineSegment(sketch, "E30.5.0.99", {"start": v(381.7, 71.64) * mm, "end": v(381.7, 67.02) * mm});
            skLineSegment(sketch, "E30.5.0.100", {"start": v(364.39, 58.94) * mm, "end": v(364.39, 54.32) * mm});
            skLineSegment(sketch, "E30.5.0.101", {"start": v(326.29, 54.32) * mm, "end": v(330.9, 54.32) * mm});
            skLineSegment(sketch, "E30.5.0.102", {"start": v(364.38, 71.64) * mm, "end": v(364.38, 67.02) * mm});
            skLineSegment(sketch, "E30.5.0.104", {"start": v(300.88, 67.02) * mm, "end": v(305.5, 67.02) * mm});
            skLineSegment(sketch, "E30.5.0.105", {"start": v(351.68, 67.02) * mm, "end": v(356.3, 67.02) * mm});
            skLineSegment(sketch, "E30.5.0.107", {"start": v(364.39, 54.32) * mm, "end": v(369, 54.32) * mm});
            skLineSegment(sketch, "E30.5.0.108", {"start": v(351.69, 54.32) * mm, "end": v(356.3, 54.32) * mm});
            skLineSegment(sketch, "E30.5.0.109", {"start": v(407.1, 58.94) * mm, "end": v(407.1, 54.32) * mm});
            skLineSegment(sketch, "E30.5.0.110", {"start": v(351.68, 71.64) * mm, "end": v(356.3, 71.64) * mm});
            skLineSegment(sketch, "E30.5.0.111", {"start": v(402.48, 71.64) * mm, "end": v(407.1, 71.64) * mm});
            skLineSegment(sketch, "E30.5.0.114", {"start": v(300.88, 71.64) * mm, "end": v(305.5, 71.64) * mm});
            skLineSegment(sketch, "E30.5.0.116", {"start": v(338.99, 58.94) * mm, "end": v(338.99, 54.32) * mm});
            skLineSegment(sketch, "E30.5.0.119", {"start": v(326.28, 71.64) * mm, "end": v(330.9, 71.64) * mm});
            skLineSegment(sketch, "E30.5.0.120", {"start": v(377.08, 71.64) * mm, "end": v(381.7, 71.64) * mm});
            skLineSegment(sketch, "E30.5.0.121", {"start": v(377.09, 54.32) * mm, "end": v(381.7, 54.32) * mm});
            skLineSegment(sketch, "E30.5.0.122", {"start": v(300.89, 54.32) * mm, "end": v(305.5, 54.32) * mm});
            skLineSegment(sketch, "E30.5.0.123", {"start": v(356.3, 58.94) * mm, "end": v(356.3, 54.32) * mm});
            skLineSegment(sketch, "E30.5.0.124", {"start": v(338.98, 71.64) * mm, "end": v(338.98, 67.02) * mm});
            skLineSegment(sketch, "E30.5.0.125", {"start": v(389.78, 71.64) * mm, "end": v(389.78, 67.02) * mm});
            skLineSegment(sketch, "E30.5.0.130", {"start": v(402.49, 54.32) * mm, "end": v(407.1, 54.32) * mm});
            skLineSegment(sketch, "E30.5.0.132", {"start": v(369, 71.64) * mm, "end": v(369, 67.02) * mm});
            skLineSegment(sketch, "E30.5.0.133", {"start": v(318.2, 71.64) * mm, "end": v(318.2, 67.02) * mm});
            skLineSegment(sketch, "E30.5.0.137", {"start": v(364.38, 67.02) * mm, "end": v(369, 67.02) * mm});
            skLineSegment(sketch, "E30.5.0.138", {"start": v(313.58, 67.02) * mm, "end": v(318.2, 67.02) * mm});
            skLineSegment(sketch, "E30.5.0.143", {"start": v(313.59, 58.94) * mm, "end": v(313.59, 54.32) * mm});
            skLineSegment(sketch, "E31", {"start": v(368.98, 97.04) * mm, "end": v(368.98, 92.42) * mm});
            skLineSegment(sketch, "E32", {"start": v(282.32, 52) * mm, "end": v(282.32, 204.4) * mm});
            skSolve(sketch);
        }
        {
            var Q0;
            Q0=qCreatedBy(makeId("Front.planeOp"),FACE);
            var sketch = newSketch(context, id + "F2", { "sketchPlane" : qUnion([Q0])});
            skLineSegment(sketch, "E33", {"start": v(-263.86, 162.85) * mm, "end": v(-149.56, 162.85) * mm});
            skLineSegment(sketch, "E34", {"start": v(-263.86, 162.85) * mm, "end": v(-378.16, 162.85) * mm});
            skLineSegment(sketch, "E35", {"start": v(-378.16, 199.81) * mm, "end": v(-378.16, 162.85) * mm});
            skLineSegment(sketch, "E36", {"start": v(-149.56, 199.81) * mm, "end": v(-149.56, 162.85) * mm});
            skLineSegment(sketch, "E37", {"start": v(-378.16, 162.85) * mm, "end": v(-378.16, 166.9) * mm});
            skLineSegment(sketch, "E38", {"start": v(-378.16, 162.85) * mm, "end": v(-374.12, 162.85) * mm});
            skLineSegment(sketch, "E39.4.0.4", {"start": v(-372.35, 195.23) * mm, "end": v(-367.73, 195.23) * mm});
            skLineSegment(sketch, "E39.4.0.5", {"start": v(-367.74, 195.23) * mm, "end": v(-367.74, 190.6) * mm});
            skLineSegment(sketch, "E39.4.0.6", {"start": v(-372.35, 190.6) * mm, "end": v(-367.73, 190.6) * mm});
            skLineSegment(sketch, "E39.4.0.7", {"start": v(-372.36, 195.23) * mm, "end": v(-372.36, 190.6) * mm});
            skLineSegment(sketch, "E39.5.0.0", {"start": v(-372.35, 182.54) * mm, "end": v(-367.73, 182.54) * mm});
            skLineSegment(sketch, "E39.5.0.1", {"start": v(-372.35, 182.54) * mm, "end": v(-372.35, 177.92) * mm});
            skLineSegment(sketch, "E39.5.0.2", {"start": v(-372.35, 177.92) * mm, "end": v(-367.73, 177.92) * mm});
            skLineSegment(sketch, "E39.5.0.3", {"start": v(-367.73, 182.54) * mm, "end": v(-367.73, 177.92) * mm});
            skLineSegment(sketch, "E39.5.0.4", {"start": v(-372.34, 169.84) * mm, "end": v(-367.72, 169.84) * mm});
            skLineSegment(sketch, "E39.5.0.5", {"start": v(-367.73, 169.84) * mm, "end": v(-367.73, 165.22) * mm});
            skLineSegment(sketch, "E39.5.0.6", {"start": v(-372.34, 165.22) * mm, "end": v(-367.72, 165.22) * mm});
            skLineSegment(sketch, "E39.5.0.7", {"start": v(-372.35, 169.84) * mm, "end": v(-372.35, 165.22) * mm});
            skPoint(sketch, "E40.4.0.1", {"position": v(-370, 192.87) * mm});
            skPoint(sketch, "E40.4.0.2", {"position": v(-357.3, 192.87) * mm});
            skPoint(sketch, "E40.4.0.6", {"position": v(-370.01, 192.88) * mm});
            skLineSegment(sketch, "E40.4.0.8", {"start": v(-194.52, 195.18) * mm, "end": v(-189.9, 195.18) * mm});
            skLineSegment(sketch, "E40.4.0.9", {"start": v(-266.1, 195.18) * mm, "end": v(-266.1, 190.56) * mm});
            skLineSegment(sketch, "E40.4.0.16", {"start": v(-215.3, 195.18) * mm, "end": v(-215.3, 190.56) * mm});
            skLineSegment(sketch, "E40.4.0.17", {"start": v(-253.4, 195.18) * mm, "end": v(-253.4, 190.56) * mm});
            skLineSegment(sketch, "E40.4.0.18", {"start": v(-270.72, 195.18) * mm, "end": v(-266.1, 195.18) * mm});
            skLineSegment(sketch, "E40.4.0.19", {"start": v(-283.42, 195.18) * mm, "end": v(-283.42, 190.56) * mm});
            skLineSegment(sketch, "E40.4.0.20", {"start": v(-283.42, 190.56) * mm, "end": v(-278.8, 190.56) * mm});
            skLineSegment(sketch, "E40.4.0.25", {"start": v(-228, 195.18) * mm, "end": v(-228, 190.56) * mm});
            skLineSegment(sketch, "E40.4.0.26", {"start": v(-207.22, 195.18) * mm, "end": v(-202.6, 195.18) * mm});
            skLineSegment(sketch, "E40.4.0.27", {"start": v(-207.22, 195.18) * mm, "end": v(-207.22, 190.56) * mm});
            skLineSegment(sketch, "E40.4.0.30", {"start": v(-291.5, 195.18) * mm, "end": v(-291.5, 190.56) * mm});
            skLineSegment(sketch, "E40.4.0.33", {"start": v(-181.82, 195.18) * mm, "end": v(-181.82, 190.56) * mm});
            skLineSegment(sketch, "E40.4.0.34", {"start": v(-219.92, 195.18) * mm, "end": v(-215.3, 195.18) * mm});
            skLineSegment(sketch, "E40.4.0.35", {"start": v(-219.92, 190.56) * mm, "end": v(-215.3, 190.56) * mm});
            skLineSegment(sketch, "E40.4.0.36", {"start": v(-258.02, 195.18) * mm, "end": v(-258.02, 190.56) * mm});
            skLineSegment(sketch, "E40.4.0.37", {"start": v(-169.12, 195.18) * mm, "end": v(-169.12, 190.56) * mm});
            skLineSegment(sketch, "E40.4.0.40", {"start": v(-232.62, 195.18) * mm, "end": v(-232.62, 190.56) * mm});
            skLineSegment(sketch, "E40.4.0.41", {"start": v(-334.22, 190.56) * mm, "end": v(-329.6, 190.56) * mm});
            skLineSegment(sketch, "E40.4.0.42", {"start": v(-164.5, 195.18) * mm, "end": v(-164.5, 190.56) * mm});
            skLineSegment(sketch, "E40.4.0.46", {"start": v(-169.12, 190.56) * mm, "end": v(-164.5, 190.56) * mm});
            skLineSegment(sketch, "E40.4.0.47", {"start": v(-169.12, 195.18) * mm, "end": v(-164.5, 195.18) * mm});
            skLineSegment(sketch, "E40.4.0.48", {"start": v(-346.92, 195.18) * mm, "end": v(-342.3, 195.18) * mm});
            skLineSegment(sketch, "E40.4.0.49", {"start": v(-308.82, 195.18) * mm, "end": v(-308.82, 190.56) * mm});
            skLineSegment(sketch, "E40.4.0.50", {"start": v(-342.3, 195.18) * mm, "end": v(-342.3, 190.56) * mm});
            skLineSegment(sketch, "E40.4.0.51", {"start": v(-245.32, 190.56) * mm, "end": v(-240.7, 190.56) * mm});
            skLineSegment(sketch, "E40.4.0.57", {"start": v(-240.7, 195.18) * mm, "end": v(-240.7, 190.56) * mm});
            skLineSegment(sketch, "E40.4.0.61", {"start": v(-321.52, 195.18) * mm, "end": v(-321.52, 190.56) * mm});
            skLineSegment(sketch, "E40.4.0.62", {"start": v(-308.82, 190.56) * mm, "end": v(-304.2, 190.56) * mm});
            skLineSegment(sketch, "E40.4.0.63", {"start": v(-359.62, 190.56) * mm, "end": v(-355, 190.56) * mm});
            skLineSegment(sketch, "E40.4.0.66", {"start": v(-270.72, 190.56) * mm, "end": v(-266.1, 190.56) * mm});
            skLineSegment(sketch, "E40.4.0.67", {"start": v(-245.32, 195.18) * mm, "end": v(-240.7, 195.18) * mm});
            skLineSegment(sketch, "E40.4.0.68", {"start": v(-181.82, 195.18) * mm, "end": v(-177.2, 195.18) * mm});
            skLineSegment(sketch, "E40.4.0.69", {"start": v(-270.72, 195.18) * mm, "end": v(-270.72, 190.56) * mm});
            skLineSegment(sketch, "E40.4.0.70", {"start": v(-189.9, 195.18) * mm, "end": v(-189.9, 190.56) * mm});
            skLineSegment(sketch, "E40.4.0.71", {"start": v(-308.82, 195.18) * mm, "end": v(-304.2, 195.18) * mm});
            skLineSegment(sketch, "E40.4.0.79", {"start": v(-232.62, 195.18) * mm, "end": v(-228, 195.18) * mm});
            skLineSegment(sketch, "E40.4.0.80", {"start": v(-156.42, 195.18) * mm, "end": v(-151.8, 195.18) * mm});
            skLineSegment(sketch, "E40.4.0.81", {"start": v(-334.22, 195.18) * mm, "end": v(-334.22, 190.56) * mm});
            skLineSegment(sketch, "E40.4.0.82", {"start": v(-258.02, 195.18) * mm, "end": v(-253.4, 195.18) * mm});
            skLineSegment(sketch, "E40.4.0.88", {"start": v(-359.62, 195.18) * mm, "end": v(-359.62, 190.56) * mm});
            skLineSegment(sketch, "E40.4.0.89", {"start": v(-329.6, 195.18) * mm, "end": v(-329.6, 190.56) * mm});
            skLineSegment(sketch, "E40.4.0.90", {"start": v(-304.2, 195.18) * mm, "end": v(-304.2, 190.56) * mm});
            skLineSegment(sketch, "E40.4.0.91", {"start": v(-177.2, 195.18) * mm, "end": v(-177.2, 190.56) * mm});
            skLineSegment(sketch, "E40.4.0.92", {"start": v(-321.52, 195.18) * mm, "end": v(-316.9, 195.18) * mm});
            skLineSegment(sketch, "E40.4.0.93", {"start": v(-156.42, 195.18) * mm, "end": v(-156.42, 190.56) * mm});
            skLineSegment(sketch, "E40.4.0.97", {"start": v(-296.12, 195.18) * mm, "end": v(-291.5, 195.18) * mm});
            skLineSegment(sketch, "E40.4.0.100", {"start": v(-194.52, 195.18) * mm, "end": v(-194.52, 190.56) * mm});
            skLineSegment(sketch, "E40.4.0.101", {"start": v(-232.62, 190.56) * mm, "end": v(-228, 190.56) * mm});
            skLineSegment(sketch, "E40.4.0.106", {"start": v(-283.42, 195.18) * mm, "end": v(-278.8, 195.18) * mm});
            skLineSegment(sketch, "E40.4.0.107", {"start": v(-194.52, 190.56) * mm, "end": v(-189.9, 190.56) * mm});
            skLineSegment(sketch, "E40.4.0.108", {"start": v(-207.22, 190.56) * mm, "end": v(-202.6, 190.56) * mm});
            skLineSegment(sketch, "E40.4.0.109", {"start": v(-151.8, 195.18) * mm, "end": v(-151.8, 190.56) * mm});
            skLineSegment(sketch, "E40.4.0.112", {"start": v(-316.9, 195.18) * mm, "end": v(-316.9, 190.56) * mm});
            skLineSegment(sketch, "E40.4.0.115", {"start": v(-278.8, 195.18) * mm, "end": v(-278.8, 190.56) * mm});
            skLineSegment(sketch, "E40.4.0.116", {"start": v(-219.92, 195.18) * mm, "end": v(-219.92, 190.56) * mm});
            skLineSegment(sketch, "E40.4.0.121", {"start": v(-181.82, 190.56) * mm, "end": v(-177.2, 190.56) * mm});
            skLineSegment(sketch, "E40.4.0.122", {"start": v(-258.02, 190.56) * mm, "end": v(-253.4, 190.56) * mm});
            skLineSegment(sketch, "E40.4.0.123", {"start": v(-202.6, 195.18) * mm, "end": v(-202.6, 190.56) * mm});
            skLineSegment(sketch, "E40.4.0.126", {"start": v(-296.12, 190.56) * mm, "end": v(-291.5, 190.56) * mm});
            skLineSegment(sketch, "E40.4.0.127", {"start": v(-296.12, 195.18) * mm, "end": v(-296.12, 190.56) * mm});
            skLineSegment(sketch, "E40.4.0.128", {"start": v(-321.52, 190.56) * mm, "end": v(-316.9, 190.56) * mm});
            skLineSegment(sketch, "E40.4.0.129", {"start": v(-372.32, 182.5) * mm, "end": v(-367.7, 182.5) * mm});
            skLineSegment(sketch, "E40.4.0.130", {"start": v(-156.42, 190.56) * mm, "end": v(-151.8, 190.56) * mm});
            skLineSegment(sketch, "E40.4.0.136", {"start": v(-334.22, 195.18) * mm, "end": v(-329.6, 195.18) * mm});
            skLineSegment(sketch, "E40.4.0.141", {"start": v(-346.92, 190.56) * mm, "end": v(-342.3, 190.56) * mm});
            skLineSegment(sketch, "E40.4.0.142", {"start": v(-346.92, 195.18) * mm, "end": v(-346.92, 190.56) * mm});
            skLineSegment(sketch, "E40.4.0.143", {"start": v(-245.32, 195.18) * mm, "end": v(-245.32, 190.56) * mm});
            skLineSegment(sketch, "E40.4.0.147", {"start": v(-355, 195.18) * mm, "end": v(-355, 190.56) * mm});
            skLineSegment(sketch, "E40.4.0.149", {"start": v(-359.62, 195.18) * mm, "end": v(-355, 195.18) * mm});
            skLineSegment(sketch, "E40.4.0.151", {"start": v(-372.32, 195.18) * mm, "end": v(-367.7, 195.18) * mm});
            skLineSegment(sketch, "E40.4.0.153", {"start": v(-372.32, 195.18) * mm, "end": v(-372.32, 190.56) * mm});
            skLineSegment(sketch, "E40.4.0.154", {"start": v(-372.33, 195.19) * mm, "end": v(-367.7, 195.19) * mm});
            skLineSegment(sketch, "E40.4.0.159", {"start": v(-372.32, 190.56) * mm, "end": v(-367.7, 190.56) * mm});
            skLineSegment(sketch, "E40.4.0.160", {"start": v(-367.7, 195.19) * mm, "end": v(-367.7, 190.56) * mm});
            skLineSegment(sketch, "E40.4.0.161", {"start": v(-372.33, 195.19) * mm, "end": v(-372.33, 190.56) * mm});
            skLineSegment(sketch, "E40.4.0.162", {"start": v(-372.33, 190.56) * mm, "end": v(-367.7, 190.56) * mm});
            skLineSegment(sketch, "E40.4.0.163", {"start": v(-367.7, 195.18) * mm, "end": v(-367.7, 190.56) * mm});
            skPoint(sketch, "E40.5.0.0", {"position": v(-370, 180.18) * mm});
            skPoint(sketch, "E40.5.0.1", {"position": v(-369.99, 167.47) * mm});
            skPoint(sketch, "E40.5.0.2", {"position": v(-357.29, 167.47) * mm});
            skPoint(sketch, "E40.5.0.3", {"position": v(-357.3, 180.18) * mm});
            skPoint(sketch, "E40.5.0.6", {"position": v(-370, 167.48) * mm});
            skLineSegment(sketch, "E40.5.0.7", {"start": v(-378.07, 188.25) * mm, "end": v(-378.07, 184.21) * mm});
            skLineSegment(sketch, "E40.5.0.8", {"start": v(-194.5, 169.78) * mm, "end": v(-189.88, 169.78) * mm});
            skLineSegment(sketch, "E40.5.0.9", {"start": v(-266.08, 169.78) * mm, "end": v(-266.08, 165.16) * mm});
            skLineSegment(sketch, "E40.5.0.14", {"start": v(-321.5, 182.49) * mm, "end": v(-321.5, 177.86) * mm});
            skLineSegment(sketch, "E40.5.0.15", {"start": v(-270.7, 182.49) * mm, "end": v(-270.7, 177.86) * mm});
            skLineSegment(sketch, "E40.5.0.16", {"start": v(-215.28, 169.78) * mm, "end": v(-215.28, 165.16) * mm});
            skLineSegment(sketch, "E40.5.0.17", {"start": v(-253.38, 169.78) * mm, "end": v(-253.38, 165.16) * mm});
            skLineSegment(sketch, "E40.5.0.18", {"start": v(-270.7, 169.78) * mm, "end": v(-266.08, 169.78) * mm});
            skLineSegment(sketch, "E40.5.0.19", {"start": v(-283.4, 169.78) * mm, "end": v(-283.4, 165.16) * mm});
            skLineSegment(sketch, "E40.5.0.20", {"start": v(-283.4, 165.16) * mm, "end": v(-278.78, 165.16) * mm});
            skLineSegment(sketch, "E40.5.0.21", {"start": v(-346.9, 182.49) * mm, "end": v(-342.29, 182.49) * mm});
            skLineSegment(sketch, "E40.5.0.22", {"start": v(-296.1, 182.49) * mm, "end": v(-291.49, 182.49) * mm});
            skLineSegment(sketch, "E40.5.0.23", {"start": v(-245.3, 182.49) * mm, "end": v(-240.69, 182.49) * mm});
            skLineSegment(sketch, "E40.5.0.24", {"start": v(-194.5, 182.49) * mm, "end": v(-189.89, 182.49) * mm});
            skLineSegment(sketch, "E40.5.0.25", {"start": v(-227.98, 169.78) * mm, "end": v(-227.98, 165.16) * mm});
            skLineSegment(sketch, "E40.5.0.26", {"start": v(-207.2, 169.78) * mm, "end": v(-202.58, 169.78) * mm});
            skLineSegment(sketch, "E40.5.0.27", {"start": v(-207.2, 169.78) * mm, "end": v(-207.2, 165.16) * mm});
            skLineSegment(sketch, "E40.5.0.28", {"start": v(-219.9, 177.86) * mm, "end": v(-215.29, 177.86) * mm});
            skLineSegment(sketch, "E40.5.0.29", {"start": v(-169.1, 177.86) * mm, "end": v(-164.49, 177.86) * mm});
            skLineSegment(sketch, "E40.5.0.30", {"start": v(-291.48, 169.78) * mm, "end": v(-291.48, 165.16) * mm});
            skLineSegment(sketch, "E40.5.0.31", {"start": v(-321.5, 177.86) * mm, "end": v(-316.89, 177.86) * mm});
            skLineSegment(sketch, "E40.5.0.32", {"start": v(-270.7, 177.86) * mm, "end": v(-266.09, 177.86) * mm});
            skLineSegment(sketch, "E40.5.0.33", {"start": v(-181.8, 169.78) * mm, "end": v(-181.8, 165.16) * mm});
            skLineSegment(sketch, "E40.5.0.34", {"start": v(-219.9, 169.78) * mm, "end": v(-215.28, 169.78) * mm});
            skLineSegment(sketch, "E40.5.0.35", {"start": v(-219.9, 165.16) * mm, "end": v(-215.28, 165.16) * mm});
            skLineSegment(sketch, "E40.5.0.36", {"start": v(-258, 169.78) * mm, "end": v(-258, 165.16) * mm});
            skLineSegment(sketch, "E40.5.0.37", {"start": v(-169.1, 169.78) * mm, "end": v(-169.1, 165.16) * mm});
            skLineSegment(sketch, "E40.5.0.38", {"start": v(-215.29, 182.49) * mm, "end": v(-215.29, 177.86) * mm});
            skLineSegment(sketch, "E40.5.0.39", {"start": v(-164.49, 182.49) * mm, "end": v(-164.49, 177.86) * mm});
            skLineSegment(sketch, "E40.5.0.40", {"start": v(-232.6, 169.78) * mm, "end": v(-232.6, 165.16) * mm});
            skLineSegment(sketch, "E40.5.0.41", {"start": v(-334.2, 165.16) * mm, "end": v(-329.58, 165.16) * mm});
            skLineSegment(sketch, "E40.5.0.42", {"start": v(-164.48, 169.78) * mm, "end": v(-164.48, 165.16) * mm});
            skLineSegment(sketch, "E40.5.0.43", {"start": v(-316.89, 182.49) * mm, "end": v(-316.89, 177.86) * mm});
            skLineSegment(sketch, "E40.5.0.44", {"start": v(-266.09, 182.49) * mm, "end": v(-266.09, 177.86) * mm});
            skLineSegment(sketch, "E40.5.0.45", {"start": v(-156.4, 182.49) * mm, "end": v(-156.4, 177.86) * mm});
            skLineSegment(sketch, "E40.5.0.46", {"start": v(-169.1, 165.16) * mm, "end": v(-164.48, 165.16) * mm});
            skLineSegment(sketch, "E40.5.0.47", {"start": v(-169.1, 169.78) * mm, "end": v(-164.48, 169.78) * mm});
            skLineSegment(sketch, "E40.5.0.48", {"start": v(-346.9, 169.78) * mm, "end": v(-342.28, 169.78) * mm});
            skLineSegment(sketch, "E40.5.0.49", {"start": v(-308.8, 169.78) * mm, "end": v(-308.8, 165.16) * mm});
            skLineSegment(sketch, "E40.5.0.50", {"start": v(-342.28, 169.78) * mm, "end": v(-342.28, 165.16) * mm});
            skLineSegment(sketch, "E40.5.0.51", {"start": v(-245.3, 165.16) * mm, "end": v(-240.68, 165.16) * mm});
            skLineSegment(sketch, "E40.5.0.52", {"start": v(-308.8, 182.49) * mm, "end": v(-308.8, 177.86) * mm});
            skLineSegment(sketch, "E40.5.0.53", {"start": v(-258, 182.49) * mm, "end": v(-258, 177.86) * mm});
            skLineSegment(sketch, "E40.5.0.54", {"start": v(-219.9, 182.49) * mm, "end": v(-215.29, 182.49) * mm});
            skLineSegment(sketch, "E40.5.0.55", {"start": v(-169.1, 182.49) * mm, "end": v(-164.49, 182.49) * mm});
            skLineSegment(sketch, "E40.5.0.56", {"start": v(-207.2, 182.49) * mm, "end": v(-207.2, 177.86) * mm});
            skLineSegment(sketch, "E40.5.0.57", {"start": v(-240.68, 169.78) * mm, "end": v(-240.68, 165.16) * mm});
            skLineSegment(sketch, "E40.5.0.58", {"start": v(-321.5, 182.49) * mm, "end": v(-316.89, 182.49) * mm});
            skLineSegment(sketch, "E40.5.0.59", {"start": v(-270.7, 182.49) * mm, "end": v(-266.09, 182.49) * mm});
            skLineSegment(sketch, "E40.5.0.60", {"start": v(-346.9, 182.49) * mm, "end": v(-346.9, 177.86) * mm});
            skLineSegment(sketch, "E40.5.0.61", {"start": v(-321.5, 169.78) * mm, "end": v(-321.5, 165.16) * mm});
            skLineSegment(sketch, "E40.5.0.62", {"start": v(-308.8, 165.16) * mm, "end": v(-304.18, 165.16) * mm});
            skLineSegment(sketch, "E40.5.0.63", {"start": v(-359.6, 165.16) * mm, "end": v(-354.98, 165.16) * mm});
            skLineSegment(sketch, "E40.5.0.64", {"start": v(-202.59, 182.49) * mm, "end": v(-202.59, 177.86) * mm});
            skLineSegment(sketch, "E40.5.0.65", {"start": v(-151.79, 182.49) * mm, "end": v(-151.79, 177.86) * mm});
            skLineSegment(sketch, "E40.5.0.66", {"start": v(-270.7, 165.16) * mm, "end": v(-266.08, 165.16) * mm});
            skLineSegment(sketch, "E40.5.0.67", {"start": v(-245.3, 169.78) * mm, "end": v(-240.68, 169.78) * mm});
            skLineSegment(sketch, "E40.5.0.68", {"start": v(-181.8, 169.78) * mm, "end": v(-177.18, 169.78) * mm});
            skLineSegment(sketch, "E40.5.0.69", {"start": v(-270.7, 169.78) * mm, "end": v(-270.7, 165.16) * mm});
            skLineSegment(sketch, "E40.5.0.70", {"start": v(-189.88, 169.78) * mm, "end": v(-189.88, 165.16) * mm});
            skLineSegment(sketch, "E40.5.0.71", {"start": v(-308.8, 169.78) * mm, "end": v(-304.18, 169.78) * mm});
            skLineSegment(sketch, "E40.5.0.72", {"start": v(-334.2, 182.49) * mm, "end": v(-334.2, 177.86) * mm});
            skLineSegment(sketch, "E40.5.0.73", {"start": v(-283.4, 182.49) * mm, "end": v(-283.4, 177.86) * mm});
            skLineSegment(sketch, "E40.5.0.74", {"start": v(-232.6, 182.49) * mm, "end": v(-232.6, 177.86) * mm});
            skLineSegment(sketch, "E40.5.0.75", {"start": v(-181.8, 182.49) * mm, "end": v(-181.8, 177.86) * mm});
            skLineSegment(sketch, "E40.5.0.76", {"start": v(-304.19, 182.49) * mm, "end": v(-304.19, 177.86) * mm});
            skLineSegment(sketch, "E40.5.0.77", {"start": v(-253.39, 182.49) * mm, "end": v(-253.39, 177.86) * mm});
            skLineSegment(sketch, "E40.5.0.78", {"start": v(-296.1, 182.49) * mm, "end": v(-296.1, 177.86) * mm});
            skLineSegment(sketch, "E40.5.0.79", {"start": v(-232.6, 169.78) * mm, "end": v(-227.98, 169.78) * mm});
            skLineSegment(sketch, "E40.5.0.80", {"start": v(-156.4, 169.78) * mm, "end": v(-151.78, 169.78) * mm});
            skLineSegment(sketch, "E40.5.0.81", {"start": v(-334.2, 169.78) * mm, "end": v(-334.2, 165.16) * mm});
            skLineSegment(sketch, "E40.5.0.82", {"start": v(-258, 169.78) * mm, "end": v(-253.38, 169.78) * mm});
            skLineSegment(sketch, "E40.5.0.83", {"start": v(-334.2, 177.86) * mm, "end": v(-329.59, 177.86) * mm});
            skLineSegment(sketch, "E40.5.0.84", {"start": v(-283.4, 177.86) * mm, "end": v(-278.79, 177.86) * mm});
            skLineSegment(sketch, "E40.5.0.85", {"start": v(-232.6, 177.86) * mm, "end": v(-227.99, 177.86) * mm});
            skLineSegment(sketch, "E40.5.0.86", {"start": v(-181.8, 177.86) * mm, "end": v(-177.19, 177.86) * mm});
            skLineSegment(sketch, "E40.5.0.87", {"start": v(-245.3, 182.49) * mm, "end": v(-245.3, 177.86) * mm});
            skLineSegment(sketch, "E40.5.0.88", {"start": v(-359.6, 169.78) * mm, "end": v(-359.6, 165.16) * mm});
            skLineSegment(sketch, "E40.5.0.89", {"start": v(-329.58, 169.78) * mm, "end": v(-329.58, 165.16) * mm});
            skLineSegment(sketch, "E40.5.0.90", {"start": v(-304.18, 169.78) * mm, "end": v(-304.18, 165.16) * mm});
            skLineSegment(sketch, "E40.5.0.91", {"start": v(-177.18, 169.78) * mm, "end": v(-177.18, 165.16) * mm});
            skLineSegment(sketch, "E40.5.0.92", {"start": v(-321.5, 169.78) * mm, "end": v(-316.88, 169.78) * mm});
            skLineSegment(sketch, "E40.5.0.93", {"start": v(-156.4, 169.78) * mm, "end": v(-156.4, 165.16) * mm});
            skLineSegment(sketch, "E40.5.0.94", {"start": v(-329.59, 182.49) * mm, "end": v(-329.59, 177.86) * mm});
            skLineSegment(sketch, "E40.5.0.95", {"start": v(-156.4, 177.86) * mm, "end": v(-151.79, 177.86) * mm});
            skLineSegment(sketch, "E40.5.0.96", {"start": v(-278.79, 182.49) * mm, "end": v(-278.79, 177.86) * mm});
            skLineSegment(sketch, "E40.5.0.97", {"start": v(-296.1, 169.78) * mm, "end": v(-291.48, 169.78) * mm});
            skLineSegment(sketch, "E40.5.0.98", {"start": v(-227.99, 182.49) * mm, "end": v(-227.99, 177.86) * mm});
            skLineSegment(sketch, "E40.5.0.99", {"start": v(-177.19, 182.49) * mm, "end": v(-177.19, 177.86) * mm});
            skLineSegment(sketch, "E40.5.0.100", {"start": v(-194.5, 169.78) * mm, "end": v(-194.5, 165.16) * mm});
            skLineSegment(sketch, "E40.5.0.101", {"start": v(-232.6, 165.16) * mm, "end": v(-227.98, 165.16) * mm});
            skLineSegment(sketch, "E40.5.0.102", {"start": v(-194.5, 182.49) * mm, "end": v(-194.5, 177.86) * mm});
            skLineSegment(sketch, "E40.5.0.103", {"start": v(-308.8, 177.86) * mm, "end": v(-304.19, 177.86) * mm});
            skLineSegment(sketch, "E40.5.0.104", {"start": v(-258, 177.86) * mm, "end": v(-253.39, 177.86) * mm});
            skLineSegment(sketch, "E40.5.0.105", {"start": v(-207.2, 177.86) * mm, "end": v(-202.59, 177.86) * mm});
            skLineSegment(sketch, "E40.5.0.106", {"start": v(-283.4, 169.78) * mm, "end": v(-278.78, 169.78) * mm});
            skLineSegment(sketch, "E40.5.0.107", {"start": v(-194.5, 165.16) * mm, "end": v(-189.88, 165.16) * mm});
            skLineSegment(sketch, "E40.5.0.108", {"start": v(-207.2, 165.16) * mm, "end": v(-202.58, 165.16) * mm});
            skLineSegment(sketch, "E40.5.0.109", {"start": v(-151.78, 169.78) * mm, "end": v(-151.78, 165.16) * mm});
            skLineSegment(sketch, "E40.5.0.110", {"start": v(-207.2, 182.49) * mm, "end": v(-202.59, 182.49) * mm});
            skLineSegment(sketch, "E40.5.0.111", {"start": v(-156.4, 182.49) * mm, "end": v(-151.79, 182.49) * mm});
            skLineSegment(sketch, "E40.5.0.112", {"start": v(-316.88, 169.78) * mm, "end": v(-316.88, 165.16) * mm});
            skLineSegment(sketch, "E40.5.0.113", {"start": v(-308.8, 182.49) * mm, "end": v(-304.19, 182.49) * mm});
            skLineSegment(sketch, "E40.5.0.114", {"start": v(-258, 182.49) * mm, "end": v(-253.39, 182.49) * mm});
            skLineSegment(sketch, "E40.5.0.115", {"start": v(-278.78, 169.78) * mm, "end": v(-278.78, 165.16) * mm});
            skLineSegment(sketch, "E40.5.0.116", {"start": v(-219.9, 169.78) * mm, "end": v(-219.9, 165.16) * mm});
            skLineSegment(sketch, "E40.5.0.117", {"start": v(-334.2, 182.49) * mm, "end": v(-329.59, 182.49) * mm});
            skLineSegment(sketch, "E40.5.0.118", {"start": v(-283.4, 182.49) * mm, "end": v(-278.79, 182.49) * mm});
            skLineSegment(sketch, "E40.5.0.119", {"start": v(-232.6, 182.49) * mm, "end": v(-227.99, 182.49) * mm});
            skLineSegment(sketch, "E40.5.0.120", {"start": v(-181.8, 182.49) * mm, "end": v(-177.19, 182.49) * mm});
            skLineSegment(sketch, "E40.5.0.121", {"start": v(-181.8, 165.16) * mm, "end": v(-177.18, 165.16) * mm});
            skLineSegment(sketch, "E40.5.0.122", {"start": v(-258, 165.16) * mm, "end": v(-253.38, 165.16) * mm});
            skLineSegment(sketch, "E40.5.0.123", {"start": v(-202.58, 169.78) * mm, "end": v(-202.58, 165.16) * mm});
            skLineSegment(sketch, "E40.5.0.124", {"start": v(-219.9, 182.49) * mm, "end": v(-219.9, 177.86) * mm});
            skLineSegment(sketch, "E40.5.0.125", {"start": v(-169.1, 182.49) * mm, "end": v(-169.1, 177.86) * mm});
            skLineSegment(sketch, "E40.5.0.126", {"start": v(-296.1, 165.16) * mm, "end": v(-291.48, 165.16) * mm});
            skLineSegment(sketch, "E40.5.0.127", {"start": v(-296.1, 169.78) * mm, "end": v(-296.1, 165.16) * mm});
            skLineSegment(sketch, "E40.5.0.128", {"start": v(-321.5, 165.16) * mm, "end": v(-316.88, 165.16) * mm});
            skLineSegment(sketch, "E40.5.0.130", {"start": v(-156.4, 165.16) * mm, "end": v(-151.78, 165.16) * mm});
            skLineSegment(sketch, "E40.5.0.132", {"start": v(-189.89, 182.49) * mm, "end": v(-189.89, 177.86) * mm});
            skLineSegment(sketch, "E40.5.0.133", {"start": v(-240.69, 182.49) * mm, "end": v(-240.69, 177.86) * mm});
            skLineSegment(sketch, "E40.5.0.134", {"start": v(-291.49, 182.49) * mm, "end": v(-291.49, 177.86) * mm});
            skLineSegment(sketch, "E40.5.0.135", {"start": v(-342.29, 182.49) * mm, "end": v(-342.29, 177.86) * mm});
            skLineSegment(sketch, "E40.5.0.136", {"start": v(-334.2, 169.78) * mm, "end": v(-329.58, 169.78) * mm});
            skLineSegment(sketch, "E40.5.0.137", {"start": v(-194.5, 177.86) * mm, "end": v(-189.89, 177.86) * mm});
            skLineSegment(sketch, "E40.5.0.138", {"start": v(-245.3, 177.86) * mm, "end": v(-240.69, 177.86) * mm});
            skLineSegment(sketch, "E40.5.0.139", {"start": v(-296.1, 177.86) * mm, "end": v(-291.49, 177.86) * mm});
            skLineSegment(sketch, "E40.5.0.140", {"start": v(-346.9, 177.86) * mm, "end": v(-342.29, 177.86) * mm});
            skLineSegment(sketch, "E40.5.0.141", {"start": v(-346.9, 165.16) * mm, "end": v(-342.28, 165.16) * mm});
            skLineSegment(sketch, "E40.5.0.142", {"start": v(-346.9, 169.78) * mm, "end": v(-346.9, 165.16) * mm});
            skLineSegment(sketch, "E40.5.0.143", {"start": v(-245.3, 169.78) * mm, "end": v(-245.3, 165.16) * mm});
            skLineSegment(sketch, "E40.5.0.144", {"start": v(-354.99, 182.49) * mm, "end": v(-354.99, 177.86) * mm});
            skLineSegment(sketch, "E40.5.0.145", {"start": v(-359.6, 177.86) * mm, "end": v(-354.99, 177.86) * mm});
            skLineSegment(sketch, "E40.5.0.149", {"start": v(-359.6, 169.78) * mm, "end": v(-354.98, 169.78) * mm});
            skLineSegment(sketch, "E40.5.0.150", {"start": v(-359.6, 182.49) * mm, "end": v(-354.99, 182.49) * mm});
            skLineSegment(sketch, "E40.5.0.151", {"start": v(-372.3, 169.78) * mm, "end": v(-367.68, 169.78) * mm});
            skLineSegment(sketch, "E40.5.0.153", {"start": v(-372.3, 169.78) * mm, "end": v(-372.3, 165.16) * mm});
            skLineSegment(sketch, "E40.5.0.154", {"start": v(-372.3, 169.79) * mm, "end": v(-367.69, 169.79) * mm});
            skLineSegment(sketch, "E40.5.0.155", {"start": v(-367.69, 182.49) * mm, "end": v(-367.69, 177.86) * mm});
            skLineSegment(sketch, "E40.5.0.156", {"start": v(-372.3, 182.49) * mm, "end": v(-372.3, 177.86) * mm});
            skLineSegment(sketch, "E40.5.0.157", {"start": v(-372.3, 182.49) * mm, "end": v(-367.69, 182.49) * mm});
            skLineSegment(sketch, "E40.5.0.158", {"start": v(-372.3, 177.86) * mm, "end": v(-367.69, 177.86) * mm});
            skLineSegment(sketch, "E40.5.0.159", {"start": v(-372.3, 165.16) * mm, "end": v(-367.68, 165.16) * mm});
            skLineSegment(sketch, "E40.5.0.160", {"start": v(-367.69, 169.79) * mm, "end": v(-367.69, 165.16) * mm});
            skLineSegment(sketch, "E40.5.0.161", {"start": v(-372.3, 169.79) * mm, "end": v(-372.3, 165.16) * mm});
            skLineSegment(sketch, "E40.5.0.162", {"start": v(-372.3, 165.16) * mm, "end": v(-367.69, 165.16) * mm});
            skLineSegment(sketch, "E40.5.0.163", {"start": v(-367.68, 169.78) * mm, "end": v(-367.68, 165.16) * mm});
            skLineSegment(sketch, "E41", {"start": v(-354.98, 169.78) * mm, "end": v(-354.98, 165.16) * mm});
            skLineSegment(sketch, "E42", {"start": v(-359.6, 177.86) * mm, "end": v(-359.6, 182.49) * mm});
            skLineSegment(sketch, "E43", {"start": v(-149.56, 199.81) * mm, "end": v(-378.16, 199.81) * mm});
            skPoint(sketch, "E44.start.orphan", {"position": v(-121.4, 162.85) * mm});
            skPoint(sketch, "E45.start.orphan", {"position": v(-401.46, 162.85) * mm});
            skSolve(sketch);
        }
        {
            var Q0;
            Q0=qCreatedBy(makeId("Front.planeOp"),FACE);
            var sketch = newSketch(context, id + "F3", { "sketchPlane" : qUnion([Q0])});
            skLineSegment(sketch, "E46", {"start": v(-14.44, 105.45) * mm, "end": v(99.86, 105.45) * mm});
            skLineSegment(sketch, "E47", {"start": v(-14.44, 105.45) * mm, "end": v(-128.74, 105.45) * mm});
            skLineSegment(sketch, "E48", {"start": v(-128.74, 142.4) * mm, "end": v(-128.74, 105.45) * mm});
            skLineSegment(sketch, "E49", {"start": v(99.86, 142.4) * mm, "end": v(99.86, 105.45) * mm});
            skLineSegment(sketch, "E50", {"start": v(-128.74, 105.45) * mm, "end": v(-128.74, 109.48) * mm});
            skLineSegment(sketch, "E51", {"start": v(-128.74, 105.45) * mm, "end": v(-124.7, 105.45) * mm});
            skLineSegment(sketch, "E52.4.0.4", {"start": v(-122.93, 137.82) * mm, "end": v(-118.3, 137.82) * mm});
            skLineSegment(sketch, "E52.4.0.5", {"start": v(-118.32, 137.82) * mm, "end": v(-118.32, 133.2) * mm});
            skLineSegment(sketch, "E52.4.0.6", {"start": v(-122.93, 133.2) * mm, "end": v(-118.3, 133.2) * mm});
            skLineSegment(sketch, "E52.4.0.7", {"start": v(-122.94, 137.82) * mm, "end": v(-122.94, 133.2) * mm});
            skLineSegment(sketch, "E52.5.0.0", {"start": v(-122.93, 125.13) * mm, "end": v(-118.3, 125.13) * mm});
            skLineSegment(sketch, "E52.5.0.1", {"start": v(-122.93, 125.13) * mm, "end": v(-122.93, 120.51) * mm});
            skLineSegment(sketch, "E52.5.0.2", {"start": v(-122.93, 120.51) * mm, "end": v(-118.3, 120.51) * mm});
            skLineSegment(sketch, "E52.5.0.3", {"start": v(-118.3, 125.13) * mm, "end": v(-118.3, 120.51) * mm});
            skLineSegment(sketch, "E52.5.0.4", {"start": v(-122.92, 112.43) * mm, "end": v(-118.3, 112.43) * mm});
            skLineSegment(sketch, "E52.5.0.5", {"start": v(-118.3, 112.43) * mm, "end": v(-118.3, 107.81) * mm});
            skLineSegment(sketch, "E52.5.0.6", {"start": v(-122.92, 107.8) * mm, "end": v(-118.3, 107.8) * mm});
            skLineSegment(sketch, "E52.5.0.7", {"start": v(-122.93, 112.43) * mm, "end": v(-122.93, 107.81) * mm});
            skPoint(sketch, "E53.4.0.1", {"position": v(-120.59, 135.47) * mm});
            skPoint(sketch, "E53.4.0.2", {"position": v(-107.89, 135.47) * mm});
            skPoint(sketch, "E53.4.0.6", {"position": v(-120.6, 135.47) * mm});
            skLineSegment(sketch, "E53.4.0.8", {"start": v(54.9, 137.78) * mm, "end": v(59.53, 137.78) * mm});
            skLineSegment(sketch, "E53.4.0.9", {"start": v(-16.67, 137.78) * mm, "end": v(-16.67, 133.15) * mm});
            skLineSegment(sketch, "E53.4.0.16", {"start": v(34.13, 137.78) * mm, "end": v(34.13, 133.15) * mm});
            skLineSegment(sketch, "E53.4.0.17", {"start": v(-3.97, 137.78) * mm, "end": v(-3.97, 133.15) * mm});
            skLineSegment(sketch, "E53.4.0.18", {"start": v(-21.3, 137.78) * mm, "end": v(-16.67, 137.78) * mm});
            skLineSegment(sketch, "E53.4.0.19", {"start": v(-34, 137.78) * mm, "end": v(-34, 133.15) * mm});
            skLineSegment(sketch, "E53.4.0.20", {"start": v(-34, 133.15) * mm, "end": v(-29.37, 133.15) * mm});
            skLineSegment(sketch, "E53.4.0.25", {"start": v(21.43, 137.78) * mm, "end": v(21.43, 133.15) * mm});
            skLineSegment(sketch, "E53.4.0.26", {"start": v(42.2, 137.78) * mm, "end": v(46.83, 137.78) * mm});
            skLineSegment(sketch, "E53.4.0.27", {"start": v(42.2, 137.78) * mm, "end": v(42.2, 133.15) * mm});
            skLineSegment(sketch, "E53.4.0.30", {"start": v(-42.07, 137.78) * mm, "end": v(-42.07, 133.15) * mm});
            skLineSegment(sketch, "E53.4.0.33", {"start": v(67.6, 137.78) * mm, "end": v(67.6, 133.15) * mm});
            skLineSegment(sketch, "E53.4.0.34", {"start": v(29.5, 137.78) * mm, "end": v(34.13, 137.78) * mm});
            skLineSegment(sketch, "E53.4.0.35", {"start": v(29.5, 133.15) * mm, "end": v(34.13, 133.15) * mm});
            skLineSegment(sketch, "E53.4.0.36", {"start": v(-8.6, 137.78) * mm, "end": v(-8.6, 133.15) * mm});
            skLineSegment(sketch, "E53.4.0.37", {"start": v(80.3, 137.78) * mm, "end": v(80.3, 133.15) * mm});
            skLineSegment(sketch, "E53.4.0.40", {"start": v(16.8, 137.78) * mm, "end": v(16.8, 133.15) * mm});
            skLineSegment(sketch, "E53.4.0.41", {"start": v(-84.8, 133.15) * mm, "end": v(-80.17, 133.15) * mm});
            skLineSegment(sketch, "E53.4.0.42", {"start": v(84.93, 137.78) * mm, "end": v(84.93, 133.15) * mm});
            skLineSegment(sketch, "E53.4.0.46", {"start": v(80.3, 133.15) * mm, "end": v(84.93, 133.15) * mm});
            skLineSegment(sketch, "E53.4.0.47", {"start": v(80.3, 137.78) * mm, "end": v(84.93, 137.78) * mm});
            skLineSegment(sketch, "E53.4.0.48", {"start": v(-97.5, 137.78) * mm, "end": v(-92.87, 137.78) * mm});
            skLineSegment(sketch, "E53.4.0.49", {"start": v(-59.4, 137.78) * mm, "end": v(-59.4, 133.15) * mm});
            skLineSegment(sketch, "E53.4.0.50", {"start": v(-92.87, 137.78) * mm, "end": v(-92.87, 133.15) * mm});
            skLineSegment(sketch, "E53.4.0.51", {"start": v(4.1, 133.15) * mm, "end": v(8.73, 133.15) * mm});
            skLineSegment(sketch, "E53.4.0.57", {"start": v(8.73, 137.78) * mm, "end": v(8.73, 133.15) * mm});
            skLineSegment(sketch, "E53.4.0.61", {"start": v(-72.1, 137.78) * mm, "end": v(-72.1, 133.15) * mm});
            skLineSegment(sketch, "E53.4.0.62", {"start": v(-59.4, 133.15) * mm, "end": v(-54.77, 133.15) * mm});
            skLineSegment(sketch, "E53.4.0.63", {"start": v(-110.2, 133.15) * mm, "end": v(-105.57, 133.15) * mm});
            skLineSegment(sketch, "E53.4.0.66", {"start": v(-21.3, 133.15) * mm, "end": v(-16.67, 133.15) * mm});
            skLineSegment(sketch, "E53.4.0.67", {"start": v(4.1, 137.78) * mm, "end": v(8.73, 137.78) * mm});
            skLineSegment(sketch, "E53.4.0.68", {"start": v(67.6, 137.78) * mm, "end": v(72.23, 137.78) * mm});
            skLineSegment(sketch, "E53.4.0.69", {"start": v(-21.3, 137.78) * mm, "end": v(-21.3, 133.15) * mm});
            skLineSegment(sketch, "E53.4.0.70", {"start": v(59.53, 137.78) * mm, "end": v(59.53, 133.15) * mm});
            skLineSegment(sketch, "E53.4.0.71", {"start": v(-59.4, 137.78) * mm, "end": v(-54.77, 137.78) * mm});
            skLineSegment(sketch, "E53.4.0.79", {"start": v(16.8, 137.78) * mm, "end": v(21.43, 137.78) * mm});
            skLineSegment(sketch, "E53.4.0.80", {"start": v(93, 137.78) * mm, "end": v(97.63, 137.78) * mm});
            skLineSegment(sketch, "E53.4.0.81", {"start": v(-84.8, 137.78) * mm, "end": v(-84.8, 133.15) * mm});
            skLineSegment(sketch, "E53.4.0.82", {"start": v(-8.6, 137.78) * mm, "end": v(-3.97, 137.78) * mm});
            skLineSegment(sketch, "E53.4.0.88", {"start": v(-110.2, 137.78) * mm, "end": v(-110.2, 133.15) * mm});
            skLineSegment(sketch, "E53.4.0.89", {"start": v(-80.17, 137.78) * mm, "end": v(-80.17, 133.15) * mm});
            skLineSegment(sketch, "E53.4.0.90", {"start": v(-54.77, 137.78) * mm, "end": v(-54.77, 133.15) * mm});
            skLineSegment(sketch, "E53.4.0.91", {"start": v(72.23, 137.78) * mm, "end": v(72.23, 133.15) * mm});
            skLineSegment(sketch, "E53.4.0.92", {"start": v(-72.1, 137.78) * mm, "end": v(-67.47, 137.78) * mm});
            skLineSegment(sketch, "E53.4.0.93", {"start": v(93, 137.78) * mm, "end": v(93, 133.15) * mm});
            skLineSegment(sketch, "E53.4.0.97", {"start": v(-46.7, 137.78) * mm, "end": v(-42.07, 137.78) * mm});
            skLineSegment(sketch, "E53.4.0.100", {"start": v(54.9, 137.78) * mm, "end": v(54.9, 133.15) * mm});
            skLineSegment(sketch, "E53.4.0.101", {"start": v(16.8, 133.15) * mm, "end": v(21.43, 133.15) * mm});
            skLineSegment(sketch, "E53.4.0.106", {"start": v(-34, 137.78) * mm, "end": v(-29.37, 137.78) * mm});
            skLineSegment(sketch, "E53.4.0.107", {"start": v(54.9, 133.15) * mm, "end": v(59.53, 133.15) * mm});
            skLineSegment(sketch, "E53.4.0.108", {"start": v(42.2, 133.15) * mm, "end": v(46.83, 133.15) * mm});
            skLineSegment(sketch, "E53.4.0.109", {"start": v(97.63, 137.78) * mm, "end": v(97.63, 133.15) * mm});
            skLineSegment(sketch, "E53.4.0.112", {"start": v(-67.47, 137.78) * mm, "end": v(-67.47, 133.15) * mm});
            skLineSegment(sketch, "E53.4.0.115", {"start": v(-29.37, 137.78) * mm, "end": v(-29.37, 133.15) * mm});
            skLineSegment(sketch, "E53.4.0.116", {"start": v(29.5, 137.78) * mm, "end": v(29.5, 133.15) * mm});
            skLineSegment(sketch, "E53.4.0.121", {"start": v(67.6, 133.15) * mm, "end": v(72.23, 133.15) * mm});
            skLineSegment(sketch, "E53.4.0.122", {"start": v(-8.6, 133.15) * mm, "end": v(-3.97, 133.15) * mm});
            skLineSegment(sketch, "E53.4.0.123", {"start": v(46.83, 137.78) * mm, "end": v(46.83, 133.15) * mm});
            skLineSegment(sketch, "E53.4.0.126", {"start": v(-46.7, 133.15) * mm, "end": v(-42.07, 133.15) * mm});
            skLineSegment(sketch, "E53.4.0.127", {"start": v(-46.7, 137.78) * mm, "end": v(-46.7, 133.15) * mm});
            skLineSegment(sketch, "E53.4.0.128", {"start": v(-72.1, 133.15) * mm, "end": v(-67.47, 133.15) * mm});
            skLineSegment(sketch, "E53.4.0.129", {"start": v(-122.9, 125.1) * mm, "end": v(-118.27, 125.1) * mm});
            skLineSegment(sketch, "E53.4.0.130", {"start": v(93, 133.15) * mm, "end": v(97.63, 133.15) * mm});
            skLineSegment(sketch, "E53.4.0.136", {"start": v(-84.8, 137.78) * mm, "end": v(-80.17, 137.78) * mm});
            skLineSegment(sketch, "E53.4.0.141", {"start": v(-97.5, 133.15) * mm, "end": v(-92.87, 133.15) * mm});
            skLineSegment(sketch, "E53.4.0.142", {"start": v(-97.5, 137.78) * mm, "end": v(-97.5, 133.15) * mm});
            skLineSegment(sketch, "E53.4.0.143", {"start": v(4.1, 137.78) * mm, "end": v(4.1, 133.15) * mm});
            skLineSegment(sketch, "E53.4.0.147", {"start": v(-105.57, 137.78) * mm, "end": v(-105.57, 133.15) * mm});
            skLineSegment(sketch, "E53.4.0.149", {"start": v(-110.2, 137.78) * mm, "end": v(-105.57, 137.78) * mm});
            skLineSegment(sketch, "E53.4.0.151", {"start": v(-122.9, 137.78) * mm, "end": v(-118.27, 137.78) * mm});
            skLineSegment(sketch, "E53.4.0.153", {"start": v(-122.9, 137.78) * mm, "end": v(-122.9, 133.15) * mm});
            skLineSegment(sketch, "E53.4.0.154", {"start": v(-122.9, 137.78) * mm, "end": v(-118.28, 137.78) * mm});
            skLineSegment(sketch, "E53.4.0.159", {"start": v(-122.9, 133.15) * mm, "end": v(-118.27, 133.15) * mm});
            skLineSegment(sketch, "E53.4.0.160", {"start": v(-118.28, 137.78) * mm, "end": v(-118.28, 133.16) * mm});
            skLineSegment(sketch, "E53.4.0.161", {"start": v(-122.9, 137.78) * mm, "end": v(-122.9, 133.16) * mm});
            skLineSegment(sketch, "E53.4.0.162", {"start": v(-122.9, 133.16) * mm, "end": v(-118.28, 133.16) * mm});
            skLineSegment(sketch, "E53.4.0.163", {"start": v(-118.27, 137.78) * mm, "end": v(-118.27, 133.15) * mm});
            skPoint(sketch, "E53.5.0.0", {"position": v(-120.58, 122.77) * mm});
            skPoint(sketch, "E53.5.0.1", {"position": v(-120.57, 110.07) * mm});
            skPoint(sketch, "E53.5.0.2", {"position": v(-107.87, 110.07) * mm});
            skPoint(sketch, "E53.5.0.3", {"position": v(-107.88, 122.77) * mm});
            skPoint(sketch, "E53.5.0.6", {"position": v(-120.58, 110.07) * mm});
            skLineSegment(sketch, "E53.5.0.7", {"start": v(-128.65, 130.85) * mm, "end": v(-128.65, 126.8) * mm});
            skLineSegment(sketch, "E53.5.0.8", {"start": v(54.92, 112.38) * mm, "end": v(59.54, 112.38) * mm});
            skLineSegment(sketch, "E53.5.0.9", {"start": v(-16.66, 112.38) * mm, "end": v(-16.66, 107.75) * mm});
            skLineSegment(sketch, "E53.5.0.14", {"start": v(-72.09, 125.08) * mm, "end": v(-72.09, 120.46) * mm});
            skLineSegment(sketch, "E53.5.0.15", {"start": v(-21.29, 125.08) * mm, "end": v(-21.29, 120.46) * mm});
            skLineSegment(sketch, "E53.5.0.16", {"start": v(34.14, 112.38) * mm, "end": v(34.14, 107.75) * mm});
            skLineSegment(sketch, "E53.5.0.17", {"start": v(-3.96, 112.38) * mm, "end": v(-3.96, 107.75) * mm});
            skLineSegment(sketch, "E53.5.0.18", {"start": v(-21.28, 112.38) * mm, "end": v(-16.66, 112.38) * mm});
            skLineSegment(sketch, "E53.5.0.19", {"start": v(-33.98, 112.38) * mm, "end": v(-33.98, 107.75) * mm});
            skLineSegment(sketch, "E53.5.0.20", {"start": v(-33.98, 107.75) * mm, "end": v(-29.36, 107.75) * mm});
            skLineSegment(sketch, "E53.5.0.21", {"start": v(-97.49, 125.08) * mm, "end": v(-92.87, 125.08) * mm});
            skLineSegment(sketch, "E53.5.0.22", {"start": v(-46.69, 125.08) * mm, "end": v(-42.07, 125.08) * mm});
            skLineSegment(sketch, "E53.5.0.23", {"start": v(4.11, 125.08) * mm, "end": v(8.73, 125.08) * mm});
            skLineSegment(sketch, "E53.5.0.24", {"start": v(54.91, 125.08) * mm, "end": v(59.53, 125.08) * mm});
            skLineSegment(sketch, "E53.5.0.25", {"start": v(21.44, 112.38) * mm, "end": v(21.44, 107.75) * mm});
            skLineSegment(sketch, "E53.5.0.26", {"start": v(42.22, 112.38) * mm, "end": v(46.84, 112.38) * mm});
            skLineSegment(sketch, "E53.5.0.27", {"start": v(42.22, 112.38) * mm, "end": v(42.22, 107.75) * mm});
            skLineSegment(sketch, "E53.5.0.28", {"start": v(29.51, 120.46) * mm, "end": v(34.13, 120.46) * mm});
            skLineSegment(sketch, "E53.5.0.29", {"start": v(80.31, 120.46) * mm, "end": v(84.93, 120.46) * mm});
            skLineSegment(sketch, "E53.5.0.30", {"start": v(-42.06, 112.38) * mm, "end": v(-42.06, 107.75) * mm});
            skLineSegment(sketch, "E53.5.0.31", {"start": v(-72.09, 120.46) * mm, "end": v(-67.47, 120.46) * mm});
            skLineSegment(sketch, "E53.5.0.32", {"start": v(-21.29, 120.46) * mm, "end": v(-16.67, 120.46) * mm});
            skLineSegment(sketch, "E53.5.0.33", {"start": v(67.62, 112.38) * mm, "end": v(67.62, 107.75) * mm});
            skLineSegment(sketch, "E53.5.0.34", {"start": v(29.52, 112.38) * mm, "end": v(34.14, 112.38) * mm});
            skLineSegment(sketch, "E53.5.0.35", {"start": v(29.52, 107.75) * mm, "end": v(34.14, 107.75) * mm});
            skLineSegment(sketch, "E53.5.0.36", {"start": v(-8.58, 112.38) * mm, "end": v(-8.58, 107.75) * mm});
            skLineSegment(sketch, "E53.5.0.37", {"start": v(80.32, 112.38) * mm, "end": v(80.32, 107.75) * mm});
            skLineSegment(sketch, "E53.5.0.38", {"start": v(34.13, 125.08) * mm, "end": v(34.13, 120.46) * mm});
            skLineSegment(sketch, "E53.5.0.39", {"start": v(84.93, 125.08) * mm, "end": v(84.93, 120.46) * mm});
            skLineSegment(sketch, "E53.5.0.40", {"start": v(16.82, 112.38) * mm, "end": v(16.82, 107.75) * mm});
            skLineSegment(sketch, "E53.5.0.41", {"start": v(-84.78, 107.75) * mm, "end": v(-80.16, 107.75) * mm});
            skLineSegment(sketch, "E53.5.0.42", {"start": v(84.94, 112.38) * mm, "end": v(84.94, 107.75) * mm});
            skLineSegment(sketch, "E53.5.0.43", {"start": v(-67.47, 125.08) * mm, "end": v(-67.47, 120.46) * mm});
            skLineSegment(sketch, "E53.5.0.44", {"start": v(-16.67, 125.08) * mm, "end": v(-16.67, 120.46) * mm});
            skLineSegment(sketch, "E53.5.0.45", {"start": v(93.01, 125.08) * mm, "end": v(93.01, 120.46) * mm});
            skLineSegment(sketch, "E53.5.0.46", {"start": v(80.32, 107.75) * mm, "end": v(84.94, 107.75) * mm});
            skLineSegment(sketch, "E53.5.0.47", {"start": v(80.32, 112.38) * mm, "end": v(84.94, 112.38) * mm});
            skLineSegment(sketch, "E53.5.0.48", {"start": v(-97.48, 112.38) * mm, "end": v(-92.86, 112.38) * mm});
            skLineSegment(sketch, "E53.5.0.49", {"start": v(-59.38, 112.38) * mm, "end": v(-59.38, 107.75) * mm});
            skLineSegment(sketch, "E53.5.0.50", {"start": v(-92.86, 112.38) * mm, "end": v(-92.86, 107.75) * mm});
            skLineSegment(sketch, "E53.5.0.51", {"start": v(4.12, 107.75) * mm, "end": v(8.74, 107.75) * mm});
            skLineSegment(sketch, "E53.5.0.52", {"start": v(-59.39, 125.08) * mm, "end": v(-59.39, 120.46) * mm});
            skLineSegment(sketch, "E53.5.0.53", {"start": v(-8.59, 125.08) * mm, "end": v(-8.59, 120.46) * mm});
            skLineSegment(sketch, "E53.5.0.54", {"start": v(29.51, 125.08) * mm, "end": v(34.13, 125.08) * mm});
            skLineSegment(sketch, "E53.5.0.55", {"start": v(80.31, 125.08) * mm, "end": v(84.93, 125.08) * mm});
            skLineSegment(sketch, "E53.5.0.56", {"start": v(42.21, 125.08) * mm, "end": v(42.21, 120.46) * mm});
            skLineSegment(sketch, "E53.5.0.57", {"start": v(8.74, 112.38) * mm, "end": v(8.74, 107.75) * mm});
            skLineSegment(sketch, "E53.5.0.58", {"start": v(-72.09, 125.08) * mm, "end": v(-67.47, 125.08) * mm});
            skLineSegment(sketch, "E53.5.0.59", {"start": v(-21.29, 125.08) * mm, "end": v(-16.67, 125.08) * mm});
            skLineSegment(sketch, "E53.5.0.60", {"start": v(-97.49, 125.08) * mm, "end": v(-97.49, 120.46) * mm});
            skLineSegment(sketch, "E53.5.0.61", {"start": v(-72.08, 112.38) * mm, "end": v(-72.08, 107.75) * mm});
            skLineSegment(sketch, "E53.5.0.62", {"start": v(-59.38, 107.75) * mm, "end": v(-54.76, 107.75) * mm});
            skLineSegment(sketch, "E53.5.0.63", {"start": v(-110.18, 107.75) * mm, "end": v(-105.56, 107.75) * mm});
            skLineSegment(sketch, "E53.5.0.64", {"start": v(46.83, 125.08) * mm, "end": v(46.83, 120.46) * mm});
            skLineSegment(sketch, "E53.5.0.65", {"start": v(97.63, 125.08) * mm, "end": v(97.63, 120.46) * mm});
            skLineSegment(sketch, "E53.5.0.66", {"start": v(-21.28, 107.75) * mm, "end": v(-16.66, 107.75) * mm});
            skLineSegment(sketch, "E53.5.0.67", {"start": v(4.12, 112.38) * mm, "end": v(8.74, 112.38) * mm});
            skLineSegment(sketch, "E53.5.0.68", {"start": v(67.62, 112.38) * mm, "end": v(72.24, 112.38) * mm});
            skLineSegment(sketch, "E53.5.0.69", {"start": v(-21.28, 112.38) * mm, "end": v(-21.28, 107.75) * mm});
            skLineSegment(sketch, "E53.5.0.70", {"start": v(59.54, 112.38) * mm, "end": v(59.54, 107.75) * mm});
            skLineSegment(sketch, "E53.5.0.71", {"start": v(-59.38, 112.38) * mm, "end": v(-54.76, 112.38) * mm});
            skLineSegment(sketch, "E53.5.0.72", {"start": v(-84.79, 125.08) * mm, "end": v(-84.79, 120.46) * mm});
            skLineSegment(sketch, "E53.5.0.73", {"start": v(-33.99, 125.08) * mm, "end": v(-33.99, 120.46) * mm});
            skLineSegment(sketch, "E53.5.0.74", {"start": v(16.81, 125.08) * mm, "end": v(16.81, 120.46) * mm});
            skLineSegment(sketch, "E53.5.0.75", {"start": v(67.61, 125.08) * mm, "end": v(67.61, 120.46) * mm});
            skLineSegment(sketch, "E53.5.0.76", {"start": v(-54.77, 125.08) * mm, "end": v(-54.77, 120.46) * mm});
            skLineSegment(sketch, "E53.5.0.77", {"start": v(-3.97, 125.08) * mm, "end": v(-3.97, 120.46) * mm});
            skLineSegment(sketch, "E53.5.0.78", {"start": v(-46.69, 125.08) * mm, "end": v(-46.69, 120.46) * mm});
            skLineSegment(sketch, "E53.5.0.79", {"start": v(16.82, 112.38) * mm, "end": v(21.44, 112.38) * mm});
            skLineSegment(sketch, "E53.5.0.80", {"start": v(93.02, 112.38) * mm, "end": v(97.64, 112.38) * mm});
            skLineSegment(sketch, "E53.5.0.81", {"start": v(-84.78, 112.38) * mm, "end": v(-84.78, 107.75) * mm});
            skLineSegment(sketch, "E53.5.0.82", {"start": v(-8.58, 112.38) * mm, "end": v(-3.96, 112.38) * mm});
            skLineSegment(sketch, "E53.5.0.83", {"start": v(-84.79, 120.46) * mm, "end": v(-80.17, 120.46) * mm});
            skLineSegment(sketch, "E53.5.0.84", {"start": v(-33.99, 120.46) * mm, "end": v(-29.37, 120.46) * mm});
            skLineSegment(sketch, "E53.5.0.85", {"start": v(16.81, 120.46) * mm, "end": v(21.43, 120.46) * mm});
            skLineSegment(sketch, "E53.5.0.86", {"start": v(67.61, 120.46) * mm, "end": v(72.23, 120.46) * mm});
            skLineSegment(sketch, "E53.5.0.87", {"start": v(4.11, 125.08) * mm, "end": v(4.11, 120.46) * mm});
            skLineSegment(sketch, "E53.5.0.88", {"start": v(-110.18, 112.38) * mm, "end": v(-110.18, 107.75) * mm});
            skLineSegment(sketch, "E53.5.0.89", {"start": v(-80.16, 112.38) * mm, "end": v(-80.16, 107.75) * mm});
            skLineSegment(sketch, "E53.5.0.90", {"start": v(-54.76, 112.38) * mm, "end": v(-54.76, 107.75) * mm});
            skLineSegment(sketch, "E53.5.0.91", {"start": v(72.24, 112.38) * mm, "end": v(72.24, 107.75) * mm});
            skLineSegment(sketch, "E53.5.0.92", {"start": v(-72.08, 112.38) * mm, "end": v(-67.46, 112.38) * mm});
            skLineSegment(sketch, "E53.5.0.93", {"start": v(93.02, 112.38) * mm, "end": v(93.02, 107.75) * mm});
            skLineSegment(sketch, "E53.5.0.94", {"start": v(-80.17, 125.08) * mm, "end": v(-80.17, 120.46) * mm});
            skLineSegment(sketch, "E53.5.0.95", {"start": v(93.01, 120.46) * mm, "end": v(97.63, 120.46) * mm});
            skLineSegment(sketch, "E53.5.0.96", {"start": v(-29.37, 125.08) * mm, "end": v(-29.37, 120.46) * mm});
            skLineSegment(sketch, "E53.5.0.97", {"start": v(-46.68, 112.38) * mm, "end": v(-42.06, 112.38) * mm});
            skLineSegment(sketch, "E53.5.0.98", {"start": v(21.43, 125.08) * mm, "end": v(21.43, 120.46) * mm});
            skLineSegment(sketch, "E53.5.0.99", {"start": v(72.23, 125.08) * mm, "end": v(72.23, 120.46) * mm});
            skLineSegment(sketch, "E53.5.0.100", {"start": v(54.92, 112.38) * mm, "end": v(54.92, 107.75) * mm});
            skLineSegment(sketch, "E53.5.0.101", {"start": v(16.82, 107.75) * mm, "end": v(21.44, 107.75) * mm});
            skLineSegment(sketch, "E53.5.0.102", {"start": v(54.91, 125.08) * mm, "end": v(54.91, 120.46) * mm});
            skLineSegment(sketch, "E53.5.0.103", {"start": v(-59.39, 120.46) * mm, "end": v(-54.77, 120.46) * mm});
            skLineSegment(sketch, "E53.5.0.104", {"start": v(-8.59, 120.46) * mm, "end": v(-3.97, 120.46) * mm});
            skLineSegment(sketch, "E53.5.0.105", {"start": v(42.21, 120.46) * mm, "end": v(46.83, 120.46) * mm});
            skLineSegment(sketch, "E53.5.0.106", {"start": v(-33.98, 112.38) * mm, "end": v(-29.36, 112.38) * mm});
            skLineSegment(sketch, "E53.5.0.107", {"start": v(54.92, 107.75) * mm, "end": v(59.54, 107.75) * mm});
            skLineSegment(sketch, "E53.5.0.108", {"start": v(42.22, 107.75) * mm, "end": v(46.84, 107.75) * mm});
            skLineSegment(sketch, "E53.5.0.109", {"start": v(97.64, 112.38) * mm, "end": v(97.64, 107.75) * mm});
            skLineSegment(sketch, "E53.5.0.110", {"start": v(42.21, 125.08) * mm, "end": v(46.83, 125.08) * mm});
            skLineSegment(sketch, "E53.5.0.111", {"start": v(93.01, 125.08) * mm, "end": v(97.63, 125.08) * mm});
            skLineSegment(sketch, "E53.5.0.112", {"start": v(-67.46, 112.38) * mm, "end": v(-67.46, 107.75) * mm});
            skLineSegment(sketch, "E53.5.0.113", {"start": v(-59.39, 125.08) * mm, "end": v(-54.77, 125.08) * mm});
            skLineSegment(sketch, "E53.5.0.114", {"start": v(-8.59, 125.08) * mm, "end": v(-3.97, 125.08) * mm});
            skLineSegment(sketch, "E53.5.0.115", {"start": v(-29.36, 112.38) * mm, "end": v(-29.36, 107.75) * mm});
            skLineSegment(sketch, "E53.5.0.116", {"start": v(29.52, 112.38) * mm, "end": v(29.52, 107.75) * mm});
            skLineSegment(sketch, "E53.5.0.117", {"start": v(-84.79, 125.08) * mm, "end": v(-80.17, 125.08) * mm});
            skLineSegment(sketch, "E53.5.0.118", {"start": v(-33.99, 125.08) * mm, "end": v(-29.37, 125.08) * mm});
            skLineSegment(sketch, "E53.5.0.119", {"start": v(16.81, 125.08) * mm, "end": v(21.43, 125.08) * mm});
            skLineSegment(sketch, "E53.5.0.120", {"start": v(67.61, 125.08) * mm, "end": v(72.23, 125.08) * mm});
            skLineSegment(sketch, "E53.5.0.121", {"start": v(67.62, 107.75) * mm, "end": v(72.24, 107.75) * mm});
            skLineSegment(sketch, "E53.5.0.122", {"start": v(-8.58, 107.75) * mm, "end": v(-3.96, 107.75) * mm});
            skLineSegment(sketch, "E53.5.0.123", {"start": v(46.84, 112.38) * mm, "end": v(46.84, 107.75) * mm});
            skLineSegment(sketch, "E53.5.0.124", {"start": v(29.51, 125.08) * mm, "end": v(29.51, 120.46) * mm});
            skLineSegment(sketch, "E53.5.0.125", {"start": v(80.31, 125.08) * mm, "end": v(80.31, 120.46) * mm});
            skLineSegment(sketch, "E53.5.0.126", {"start": v(-46.68, 107.75) * mm, "end": v(-42.06, 107.75) * mm});
            skLineSegment(sketch, "E53.5.0.127", {"start": v(-46.68, 112.38) * mm, "end": v(-46.68, 107.75) * mm});
            skLineSegment(sketch, "E53.5.0.128", {"start": v(-72.08, 107.75) * mm, "end": v(-67.46, 107.75) * mm});
            skLineSegment(sketch, "E53.5.0.130", {"start": v(93.02, 107.75) * mm, "end": v(97.64, 107.75) * mm});
            skLineSegment(sketch, "E53.5.0.132", {"start": v(59.53, 125.08) * mm, "end": v(59.53, 120.46) * mm});
            skLineSegment(sketch, "E53.5.0.133", {"start": v(8.73, 125.08) * mm, "end": v(8.73, 120.46) * mm});
            skLineSegment(sketch, "E53.5.0.134", {"start": v(-42.07, 125.08) * mm, "end": v(-42.07, 120.46) * mm});
            skLineSegment(sketch, "E53.5.0.135", {"start": v(-92.87, 125.08) * mm, "end": v(-92.87, 120.46) * mm});
            skLineSegment(sketch, "E53.5.0.136", {"start": v(-84.78, 112.38) * mm, "end": v(-80.16, 112.38) * mm});
            skLineSegment(sketch, "E53.5.0.137", {"start": v(54.91, 120.46) * mm, "end": v(59.53, 120.46) * mm});
            skLineSegment(sketch, "E53.5.0.138", {"start": v(4.11, 120.46) * mm, "end": v(8.73, 120.46) * mm});
            skLineSegment(sketch, "E53.5.0.139", {"start": v(-46.69, 120.46) * mm, "end": v(-42.07, 120.46) * mm});
            skLineSegment(sketch, "E53.5.0.140", {"start": v(-97.49, 120.46) * mm, "end": v(-92.87, 120.46) * mm});
            skLineSegment(sketch, "E53.5.0.141", {"start": v(-97.48, 107.75) * mm, "end": v(-92.86, 107.75) * mm});
            skLineSegment(sketch, "E53.5.0.142", {"start": v(-97.48, 112.38) * mm, "end": v(-97.48, 107.75) * mm});
            skLineSegment(sketch, "E53.5.0.143", {"start": v(4.12, 112.38) * mm, "end": v(4.12, 107.75) * mm});
            skLineSegment(sketch, "E53.5.0.144", {"start": v(-105.57, 125.08) * mm, "end": v(-105.57, 120.46) * mm});
            skLineSegment(sketch, "E53.5.0.145", {"start": v(-110.19, 120.46) * mm, "end": v(-105.57, 120.46) * mm});
            skLineSegment(sketch, "E53.5.0.149", {"start": v(-110.18, 112.38) * mm, "end": v(-105.56, 112.38) * mm});
            skLineSegment(sketch, "E53.5.0.150", {"start": v(-110.19, 125.08) * mm, "end": v(-105.57, 125.08) * mm});
            skLineSegment(sketch, "E53.5.0.151", {"start": v(-122.88, 112.38) * mm, "end": v(-118.26, 112.38) * mm});
            skLineSegment(sketch, "E53.5.0.153", {"start": v(-122.88, 112.38) * mm, "end": v(-122.88, 107.75) * mm});
            skLineSegment(sketch, "E53.5.0.154", {"start": v(-122.89, 112.38) * mm, "end": v(-118.27, 112.38) * mm});
            skLineSegment(sketch, "E53.5.0.155", {"start": v(-118.27, 125.08) * mm, "end": v(-118.27, 120.46) * mm});
            skLineSegment(sketch, "E53.5.0.156", {"start": v(-122.89, 125.08) * mm, "end": v(-122.89, 120.46) * mm});
            skLineSegment(sketch, "E53.5.0.157", {"start": v(-122.89, 125.08) * mm, "end": v(-118.27, 125.08) * mm});
            skLineSegment(sketch, "E53.5.0.158", {"start": v(-122.89, 120.46) * mm, "end": v(-118.27, 120.46) * mm});
            skLineSegment(sketch, "E53.5.0.159", {"start": v(-122.88, 107.75) * mm, "end": v(-118.26, 107.75) * mm});
            skLineSegment(sketch, "E53.5.0.160", {"start": v(-118.27, 112.38) * mm, "end": v(-118.27, 107.76) * mm});
            skLineSegment(sketch, "E53.5.0.161", {"start": v(-122.89, 112.38) * mm, "end": v(-122.89, 107.76) * mm});
            skLineSegment(sketch, "E53.5.0.162", {"start": v(-122.89, 107.76) * mm, "end": v(-118.27, 107.76) * mm});
            skLineSegment(sketch, "E53.5.0.163", {"start": v(-118.26, 112.38) * mm, "end": v(-118.26, 107.75) * mm});
            skLineSegment(sketch, "E54", {"start": v(-105.56, 112.38) * mm, "end": v(-105.56, 107.75) * mm});
            skLineSegment(sketch, "E55", {"start": v(-110.19, 120.46) * mm, "end": v(-110.19, 125.08) * mm});
            skLineSegment(sketch, "E56", {"start": v(99.86, 142.4) * mm, "end": v(-128.74, 142.4) * mm});
            skPoint(sketch, "E57.start.orphan", {"position": v(128.03, 105.45) * mm});
            skPoint(sketch, "E58.start.orphan", {"position": v(-152.04, 105.45) * mm});
            skSolve(sketch);
        }
        {
            var Q0;
            Q0 = qSketchRegion(id + "F0", true);
            extrude(context, id + "F4", {"entities" : qUnion([Q0]), "depth" : 3.17 * mm});
        }
        {
            var Q0;
            Q0 = qSketchRegion(id + "F1", true);
            extrude(context, id + "F5", {"entities" : qUnion([Q0]), "depth" : 3.17 * mm});
        }
        {
            var Q0;
            Q0 = qSketchRegion(id + "F2", true);
            extrude(context, id + "F6", {"entities" : qUnion([Q0]), "depth" : 3.17 * mm});
        }
        {
            var Q0;
            Q0 = qSketchRegion(id + "F3", true);
            extrude(context, id + "F7", {"entities" : qUnion([Q0]), "depth" : 3.17 * mm});
        }
    });
